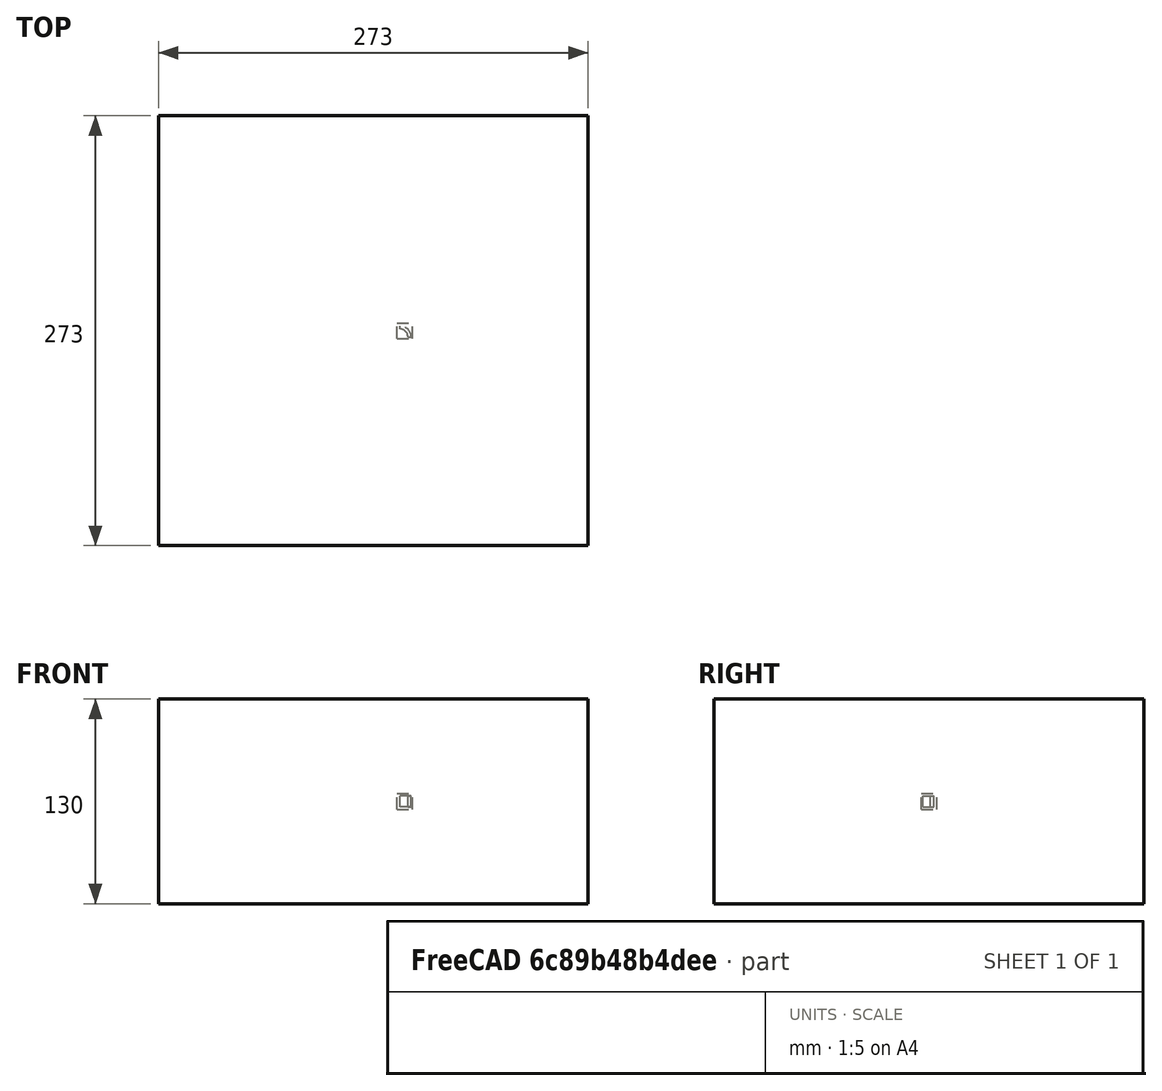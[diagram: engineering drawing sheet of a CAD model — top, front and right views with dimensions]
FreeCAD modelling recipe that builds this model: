
FCSTD DOCUMENT  (FreeCAD 0.20RUnknown)
Label: array-of-array-b
License: All rights reserved
LicenseURL: http://en.wikipedia.org/wiki/All_rights_reserved
objects: App::DocumentObjectGroupPython×1251, Part::FeaturePython×5, App::Part×5
note: 3 computed .brp shape members not serialized (recipe doc carries the construction recipe); baked Part::Feature solids carry a one-line shape summary decoded from their .brp

FEATURE [App::DocumentObjectGroupPython] HALFPI  # scripted group (container) (typed FeaturePython)
  name = HALFPI
  value = pi/2.
FEATURE [App::DocumentObjectGroupPython] PI  # scripted group (container) (typed FeaturePython)
  name = PI
  value = 1.*pi
FEATURE [App::DocumentObjectGroupPython] TWOPI  # scripted group (container) (typed FeaturePython)
  name = TWOPI
  value = 2.*pi
FEATURE [App::DocumentObjectGroupPython] Constants  # scripted group (container) (typed FeaturePython)
  Group = -> [HALFPI,PI,TWOPI]
FEATURE [App::DocumentObjectGroupPython] Variables  # scripted group (container) (typed FeaturePython)
FEATURE [App::DocumentObjectGroupPython] Quantities  # scripted group (container) (typed FeaturePython)
FEATURE [App::DocumentObjectGroupPython] Isotopes  # scripted group (container) (typed FeaturePython)
FEATURE [App::DocumentObjectGroupPython] Elements  # scripted group (container) (typed FeaturePython)
FEATURE [App::DocumentObjectGroupPython] Matrix  # scripted group (container) (typed FeaturePython)
FEATURE [App::DocumentObjectGroupPython] Surfaces  # scripted group (container) (typed FeaturePython)
FEATURE [App::DocumentObjectGroupPython] Opticals  # scripted group (container) (typed FeaturePython)
  Group = -> [Matrix,Surfaces]
FEATURE [App::DocumentObjectGroupPython] G4Isotopes  # scripted group (container) (typed FeaturePython)
FEATURE [App::DocumentObjectGroupPython] H_element  # scripted group (container) (typed FeaturePython)
  Z = 1
  atom_value = 1.008
  formula = H
  name = H_element
FEATURE [App::DocumentObjectGroupPython] He_element  # scripted group (container) (typed FeaturePython)
  Z = 2
  atom_value = 4.0026
  formula = He
  name = He_element
FEATURE [App::DocumentObjectGroupPython] Li_element  # scripted group (container) (typed FeaturePython)
  Z = 3
  atom_value = 6.94
  formula = Li
  name = Li_element
FEATURE [App::DocumentObjectGroupPython] Be_element  # scripted group (container) (typed FeaturePython)
  Z = 4
  atom_value = 9.01218
  formula = Be
  name = Be_element
FEATURE [App::DocumentObjectGroupPython] B_element  # scripted group (container) (typed FeaturePython)
  Z = 5
  atom_value = 10.81
  formula = B
  name = B_element
FEATURE [App::DocumentObjectGroupPython] C_element  # scripted group (container) (typed FeaturePython)
  Z = 6
  atom_value = 12.011
  formula = C
  name = C_element
FEATURE [App::DocumentObjectGroupPython] N_element  # scripted group (container) (typed FeaturePython)
  Z = 7
  atom_value = 14.007
  formula = N
  name = N_element
FEATURE [App::DocumentObjectGroupPython] O_element  # scripted group (container) (typed FeaturePython)
  Z = 8
  atom_value = 15.999
  formula = O
  name = O_element
FEATURE [App::DocumentObjectGroupPython] F_element  # scripted group (container) (typed FeaturePython)
  Z = 9
  atom_value = 18.9984
  formula = F
  name = F_element
FEATURE [App::DocumentObjectGroupPython] Ne_element  # scripted group (container) (typed FeaturePython)
  Z = 10
  atom_value = 20.1797
  formula = Ne
  name = Ne_element
FEATURE [App::DocumentObjectGroupPython] Na_element  # scripted group (container) (typed FeaturePython)
  Z = 11
  atom_value = 22.9898
  formula = Na
  name = Na_element
FEATURE [App::DocumentObjectGroupPython] Mg_element  # scripted group (container) (typed FeaturePython)
  Z = 12
  atom_value = 24.305
  formula = Mg
  name = Mg_element
FEATURE [App::DocumentObjectGroupPython] Al_element  # scripted group (container) (typed FeaturePython)
  Z = 13
  atom_value = 26.9815
  formula = Al
  name = Al_element
FEATURE [App::DocumentObjectGroupPython] Si_element  # scripted group (container) (typed FeaturePython)
  Z = 14
  atom_value = 28.085
  formula = Si
  name = Si_element
FEATURE [App::DocumentObjectGroupPython] P_element  # scripted group (container) (typed FeaturePython)
  Z = 15
  atom_value = 30.9738
  formula = P
  name = P_element
FEATURE [App::DocumentObjectGroupPython] S_element  # scripted group (container) (typed FeaturePython)
  Z = 16
  atom_value = 32.06
  formula = S
  name = S_element
FEATURE [App::DocumentObjectGroupPython] Cl_element  # scripted group (container) (typed FeaturePython)
  Z = 17
  atom_value = 35.45
  formula = Cl
  name = Cl_element
FEATURE [App::DocumentObjectGroupPython] Ar_element  # scripted group (container) (typed FeaturePython)
  Z = 18
  atom_value = 39.95
  formula = Ar
  name = Ar_element
FEATURE [App::DocumentObjectGroupPython] K_element  # scripted group (container) (typed FeaturePython)
  Z = 19
  atom_value = 39.0983
  formula = K
  name = K_element
FEATURE [App::DocumentObjectGroupPython] Ca_element  # scripted group (container) (typed FeaturePython)
  Z = 20
  atom_value = 40.078
  formula = Ca
  name = Ca_element
FEATURE [App::DocumentObjectGroupPython] Sc_element  # scripted group (container) (typed FeaturePython)
  Z = 21
  atom_value = 44.9559
  formula = Sc
  name = Sc_element
FEATURE [App::DocumentObjectGroupPython] Ti_element  # scripted group (container) (typed FeaturePython)
  Z = 22
  atom_value = 47.867
  formula = Ti
  name = Ti_element
FEATURE [App::DocumentObjectGroupPython] V_element  # scripted group (container) (typed FeaturePython)
  Z = 23
  atom_value = 50.9415
  formula = V
  name = V_element
FEATURE [App::DocumentObjectGroupPython] Cr_element  # scripted group (container) (typed FeaturePython)
  Z = 24
  atom_value = 51.9961
  formula = Cr
  name = Cr_element
FEATURE [App::DocumentObjectGroupPython] Mn_element  # scripted group (container) (typed FeaturePython)
  Z = 25
  atom_value = 54.938
  formula = Mn
  name = Mn_element
FEATURE [App::DocumentObjectGroupPython] Fe_element  # scripted group (container) (typed FeaturePython)
  Z = 26
  atom_value = 55.845
  formula = Fe
  name = Fe_element
FEATURE [App::DocumentObjectGroupPython] Co_element  # scripted group (container) (typed FeaturePython)
  Z = 27
  atom_value = 58.9332
  formula = Co
  name = Co_element
FEATURE [App::DocumentObjectGroupPython] Ni_element  # scripted group (container) (typed FeaturePython)
  Z = 28
  atom_value = 58.6934
  formula = Ni
  name = Ni_element
FEATURE [App::DocumentObjectGroupPython] Cu_element  # scripted group (container) (typed FeaturePython)
  Z = 29
  atom_value = 63.546
  formula = Cu
  name = Cu_element
FEATURE [App::DocumentObjectGroupPython] Zn_element  # scripted group (container) (typed FeaturePython)
  Z = 30
  atom_value = 65.38
  formula = Zn
  name = Zn_element
FEATURE [App::DocumentObjectGroupPython] Ga_element  # scripted group (container) (typed FeaturePython)
  Z = 31
  atom_value = 69.723
  formula = Ga
  name = Ga_element
FEATURE [App::DocumentObjectGroupPython] Ge_element  # scripted group (container) (typed FeaturePython)
  Z = 32
  atom_value = 72.63
  formula = Ge
  name = Ge_element
FEATURE [App::DocumentObjectGroupPython] As_element  # scripted group (container) (typed FeaturePython)
  Z = 33
  atom_value = 74.9216
  formula = As
  name = As_element
FEATURE [App::DocumentObjectGroupPython] Se_element  # scripted group (container) (typed FeaturePython)
  Z = 34
  atom_value = 78.971
  formula = Se
  name = Se_element
FEATURE [App::DocumentObjectGroupPython] Br_element  # scripted group (container) (typed FeaturePython)
  Z = 35
  atom_value = 79.904
  formula = Br
  name = Br_element
FEATURE [App::DocumentObjectGroupPython] Kr_element  # scripted group (container) (typed FeaturePython)
  Z = 36
  atom_value = 83.798
  formula = Kr
  name = Kr_element
FEATURE [App::DocumentObjectGroupPython] Rb_element  # scripted group (container) (typed FeaturePython)
  Z = 37
  atom_value = 85.4678
  formula = Rb
  name = Rb_element
FEATURE [App::DocumentObjectGroupPython] Sr_element  # scripted group (container) (typed FeaturePython)
  Z = 38
  atom_value = 87.62
  formula = Sr
  name = Sr_element
FEATURE [App::DocumentObjectGroupPython] Y_element  # scripted group (container) (typed FeaturePython)
  Z = 39
  atom_value = 88.9058
  formula = Y
  name = Y_element
FEATURE [App::DocumentObjectGroupPython] Zr_element  # scripted group (container) (typed FeaturePython)
  Z = 40
  atom_value = 91.224
  formula = Zr
  name = Zr_element
FEATURE [App::DocumentObjectGroupPython] Nb_element  # scripted group (container) (typed FeaturePython)
  Z = 41
  atom_value = 92.9064
  formula = Nb
  name = Nb_element
FEATURE [App::DocumentObjectGroupPython] Mo_element  # scripted group (container) (typed FeaturePython)
  Z = 42
  atom_value = 95.95
  formula = Mo
  name = Mo_element
FEATURE [App::DocumentObjectGroupPython] Tc_element  # scripted group (container) (typed FeaturePython)
  Z = 43
  atom_value = 97
  formula = Tc
  name = Tc_element
FEATURE [App::DocumentObjectGroupPython] Ru_element  # scripted group (container) (typed FeaturePython)
  Z = 44
  atom_value = 101.07
  formula = Ru
  name = Ru_element
FEATURE [App::DocumentObjectGroupPython] Rh_element  # scripted group (container) (typed FeaturePython)
  Z = 45
  atom_value = 102.905
  formula = Rh
  name = Rh_element
FEATURE [App::DocumentObjectGroupPython] Pd_element  # scripted group (container) (typed FeaturePython)
  Z = 46
  atom_value = 106.42
  formula = Pd
  name = Pd_element
FEATURE [App::DocumentObjectGroupPython] Ag_element  # scripted group (container) (typed FeaturePython)
  Z = 47
  atom_value = 107.868
  formula = Ag
  name = Ag_element
FEATURE [App::DocumentObjectGroupPython] Cd_element  # scripted group (container) (typed FeaturePython)
  Z = 48
  atom_value = 112.414
  formula = Cd
  name = Cd_element
FEATURE [App::DocumentObjectGroupPython] In_element  # scripted group (container) (typed FeaturePython)
  Z = 49
  atom_value = 114.818
  formula = In
  name = In_element
FEATURE [App::DocumentObjectGroupPython] Sn_element  # scripted group (container) (typed FeaturePython)
  Z = 50
  atom_value = 118.71
  formula = Sn
  name = Sn_element
FEATURE [App::DocumentObjectGroupPython] Sb_element  # scripted group (container) (typed FeaturePython)
  Z = 51
  atom_value = 121.76
  formula = Sb
  name = Sb_element
FEATURE [App::DocumentObjectGroupPython] Te_element  # scripted group (container) (typed FeaturePython)
  Z = 52
  atom_value = 127.6
  formula = Te
  name = Te_element
FEATURE [App::DocumentObjectGroupPython] I_element  # scripted group (container) (typed FeaturePython)
  Z = 53
  atom_value = 126.904
  formula = I
  name = I_element
FEATURE [App::DocumentObjectGroupPython] Xe_element  # scripted group (container) (typed FeaturePython)
  Z = 54
  atom_value = 131.293
  formula = Xe
  name = Xe_element
FEATURE [App::DocumentObjectGroupPython] Cs_element  # scripted group (container) (typed FeaturePython)
  Z = 55
  atom_value = 132.905
  formula = Cs
  name = Cs_element
FEATURE [App::DocumentObjectGroupPython] Ba_element  # scripted group (container) (typed FeaturePython)
  Z = 56
  atom_value = 137.327
  formula = Ba
  name = Ba_element
FEATURE [App::DocumentObjectGroupPython] La_element  # scripted group (container) (typed FeaturePython)
  Z = 57
  atom_value = 138.905
  formula = La
  name = La_element
FEATURE [App::DocumentObjectGroupPython] Ce_element  # scripted group (container) (typed FeaturePython)
  Z = 58
  atom_value = 140.116
  formula = Ce
  name = Ce_element
FEATURE [App::DocumentObjectGroupPython] Pr_element  # scripted group (container) (typed FeaturePython)
  Z = 59
  atom_value = 140.908
  formula = Pr
  name = Pr_element
FEATURE [App::DocumentObjectGroupPython] Nd_element  # scripted group (container) (typed FeaturePython)
  Z = 60
  atom_value = 144.242
  formula = Nd
  name = Nd_element
FEATURE [App::DocumentObjectGroupPython] Pm_element  # scripted group (container) (typed FeaturePython)
  Z = 61
  atom_value = 145
  formula = Pm
  name = Pm_element
FEATURE [App::DocumentObjectGroupPython] Sm_element  # scripted group (container) (typed FeaturePython)
  Z = 62
  atom_value = 150.36
  formula = Sm
  name = Sm_element
FEATURE [App::DocumentObjectGroupPython] Eu_element  # scripted group (container) (typed FeaturePython)
  Z = 63
  atom_value = 151.964
  formula = Eu
  name = Eu_element
FEATURE [App::DocumentObjectGroupPython] Gd_element  # scripted group (container) (typed FeaturePython)
  Z = 64
  atom_value = 157.25
  formula = Gd
  name = Gd_element
FEATURE [App::DocumentObjectGroupPython] Tb_element  # scripted group (container) (typed FeaturePython)
  Z = 65
  atom_value = 158.925
  formula = Tb
  name = Tb_element
FEATURE [App::DocumentObjectGroupPython] Dy_element  # scripted group (container) (typed FeaturePython)
  Z = 66
  atom_value = 162.5
  formula = Dy
  name = Dy_element
FEATURE [App::DocumentObjectGroupPython] Ho_element  # scripted group (container) (typed FeaturePython)
  Z = 67
  atom_value = 164.93
  formula = Ho
  name = Ho_element
FEATURE [App::DocumentObjectGroupPython] Er_element  # scripted group (container) (typed FeaturePython)
  Z = 68
  atom_value = 167.259
  formula = Er
  name = Er_element
FEATURE [App::DocumentObjectGroupPython] Tm_element  # scripted group (container) (typed FeaturePython)
  Z = 69
  atom_value = 168.934
  formula = Tm
  name = Tm_element
FEATURE [App::DocumentObjectGroupPython] Yb_element  # scripted group (container) (typed FeaturePython)
  Z = 70
  atom_value = 173.045
  formula = Yb
  name = Yb_element
FEATURE [App::DocumentObjectGroupPython] Lu_element  # scripted group (container) (typed FeaturePython)
  Z = 71
  atom_value = 174.967
  formula = Lu
  name = Lu_element
FEATURE [App::DocumentObjectGroupPython] Hf_element  # scripted group (container) (typed FeaturePython)
  Z = 72
  atom_value = 178.49
  formula = Hf
  name = Hf_element
FEATURE [App::DocumentObjectGroupPython] Ta_element  # scripted group (container) (typed FeaturePython)
  Z = 73
  atom_value = 180.948
  formula = Ta
  name = Ta_element
FEATURE [App::DocumentObjectGroupPython] W_element  # scripted group (container) (typed FeaturePython)
  Z = 74
  atom_value = 183.84
  formula = W
  name = W_element
FEATURE [App::DocumentObjectGroupPython] Re_element  # scripted group (container) (typed FeaturePython)
  Z = 75
  atom_value = 186.207
  formula = Re
  name = Re_element
FEATURE [App::DocumentObjectGroupPython] Os_element  # scripted group (container) (typed FeaturePython)
  Z = 76
  atom_value = 190.23
  formula = Os
  name = Os_element
FEATURE [App::DocumentObjectGroupPython] Ir_element  # scripted group (container) (typed FeaturePython)
  Z = 77
  atom_value = 192.217
  formula = Ir
  name = Ir_element
FEATURE [App::DocumentObjectGroupPython] Pt_element  # scripted group (container) (typed FeaturePython)
  Z = 78
  atom_value = 195.084
  formula = Pt
  name = Pt_element
FEATURE [App::DocumentObjectGroupPython] Au_element  # scripted group (container) (typed FeaturePython)
  Z = 79
  atom_value = 196.967
  formula = Au
  name = Au_element
FEATURE [App::DocumentObjectGroupPython] Hg_element  # scripted group (container) (typed FeaturePython)
  Z = 80
  atom_value = 200.592
  formula = Hg
  name = Hg_element
FEATURE [App::DocumentObjectGroupPython] Tl_element  # scripted group (container) (typed FeaturePython)
  Z = 81
  atom_value = 204.38
  formula = Tl
  name = Tl_element
FEATURE [App::DocumentObjectGroupPython] Pb_element  # scripted group (container) (typed FeaturePython)
  Z = 82
  atom_value = 207.2
  formula = Pb
  name = Pb_element
FEATURE [App::DocumentObjectGroupPython] Bi_element  # scripted group (container) (typed FeaturePython)
  Z = 83
  atom_value = 208.98
  formula = Bi
  name = Bi_element
FEATURE [App::DocumentObjectGroupPython] Po_element  # scripted group (container) (typed FeaturePython)
  Z = 84
  atom_value = 209
  formula = Po
  name = Po_element
FEATURE [App::DocumentObjectGroupPython] At_element  # scripted group (container) (typed FeaturePython)
  Z = 85
  atom_value = 210
  formula = At
  name = At_element
FEATURE [App::DocumentObjectGroupPython] Rn_element  # scripted group (container) (typed FeaturePython)
  Z = 86
  atom_value = 222
  formula = Rn
  name = Rn_element
FEATURE [App::DocumentObjectGroupPython] Fr_element  # scripted group (container) (typed FeaturePython)
  Z = 87
  atom_value = 223
  formula = Fr
  name = Fr_element
FEATURE [App::DocumentObjectGroupPython] Ra_element  # scripted group (container) (typed FeaturePython)
  Z = 88
  atom_value = 226
  formula = Ra
  name = Ra_element
FEATURE [App::DocumentObjectGroupPython] Ac_element  # scripted group (container) (typed FeaturePython)
  Z = 89
  atom_value = 227
  formula = Ac
  name = Ac_element
FEATURE [App::DocumentObjectGroupPython] Th_element  # scripted group (container) (typed FeaturePython)
  Z = 90
  atom_value = 232.038
  formula = Th
  name = Th_element
FEATURE [App::DocumentObjectGroupPython] Pa_element  # scripted group (container) (typed FeaturePython)
  Z = 91
  atom_value = 231.036
  formula = Pa
  name = Pa_element
FEATURE [App::DocumentObjectGroupPython] U_element  # scripted group (container) (typed FeaturePython)
  Z = 92
  atom_value = 238.029
  formula = U
  name = U_element
FEATURE [App::DocumentObjectGroupPython] Np_element  # scripted group (container) (typed FeaturePython)
  Z = 93
  atom_value = 237
  formula = Np
  name = Np_element
FEATURE [App::DocumentObjectGroupPython] Pu_element  # scripted group (container) (typed FeaturePython)
  Z = 94
  atom_value = 244
  formula = Pu
  name = Pu_element
FEATURE [App::DocumentObjectGroupPython] Am_element  # scripted group (container) (typed FeaturePython)
  Z = 95
  atom_value = 243
  formula = Am
  name = Am_element
FEATURE [App::DocumentObjectGroupPython] Cm_element  # scripted group (container) (typed FeaturePython)
  Z = 96
  atom_value = 247
  formula = Cm
  name = Cm_element
FEATURE [App::DocumentObjectGroupPython] Bk_element  # scripted group (container) (typed FeaturePython)
  Z = 97
  atom_value = 247
  formula = Bk
  name = Bk_element
FEATURE [App::DocumentObjectGroupPython] Cf_element  # scripted group (container) (typed FeaturePython)
  Z = 98
  atom_value = 251
  formula = Cf
  name = Cf_element
FEATURE [App::DocumentObjectGroupPython] G4Elements  # scripted group (container) (typed FeaturePython)
  Group = -> [H_element,He_element,Li_element,Be_element,B_element,C_element,N_element,O_element,F_element,Ne_element,Na_element,Mg_element,Al_element,Si_element,P_element,S_element,Cl_element,Ar_element,K_element,Ca_element,Sc_element,Ti_element,V_element,Cr_element,Mn_element,Fe_element,Co_element,Ni_element,Cu_element,Zn_element,Ga_element,Ge_element,As_element,Se_element,Br_element,Kr_element,Rb_element,+61 more]
FEATURE [App::DocumentObjectGroupPython] H_element001  label="H_element : 0.101"  # scripted group (container) (typed FeaturePython)
  n = 0.101327
FEATURE [App::DocumentObjectGroupPython] C_element001  label="C_element : 0.775"  # scripted group (container) (typed FeaturePython)
  n = 0.7755
FEATURE [App::DocumentObjectGroupPython] N_element001  label="N_element : 0.035"  # scripted group (container) (typed FeaturePython)
  n = 0.035057
FEATURE [App::DocumentObjectGroupPython] O_element001  label="O_element : 0.052"  # scripted group (container) (typed FeaturePython)
  n = 0.0523159
FEATURE [App::DocumentObjectGroupPython] F_element001  label="F_element : 0.017"  # scripted group (container) (typed FeaturePython)
  n = 0.017422
FEATURE [App::DocumentObjectGroupPython] Ca_element001  label="Ca_element : 0.018"  # scripted group (container) (typed FeaturePython)
  n = 0.018378
FEATURE [App::DocumentObjectGroupPython] G4_A_150_TISSUE  label="G4_A-150_TISSUE"  # scripted group (container) (typed FeaturePython)
  Dunit = g/cm3
  Dvalue = 1.127
  Group = -> [H_element001,C_element001,N_element001,O_element001,F_element001,Ca_element001]
  conduct = 2
  density = 1
  expand = 3
  formula = G4_A-150_TISSUE
  name = G4_A-150_TISSUE
  specific = 4
FEATURE [App::DocumentObjectGroupPython] C_element002  label="C_element : 3"  # scripted group (container) (typed FeaturePython)
  n = 3
  ref = C_element
FEATURE [App::DocumentObjectGroupPython] H_element002  label="H_element : 6"  # scripted group (container) (typed FeaturePython)
  n = 6
  ref = H_element
FEATURE [App::DocumentObjectGroupPython] O_element002  label="O_element : 1"  # scripted group (container) (typed FeaturePython)
  n = 1
  ref = O_element
FEATURE [App::DocumentObjectGroupPython] G4_ACETONE  # scripted group (container) (typed FeaturePython)
  Dunit = g/cm3
  Dvalue = 0.7899
  Group = -> [C_element002,H_element002,O_element002]
  conduct = 2
  density = 1
  expand = 3
  formula = G4_ACETONE
  name = G4_ACETONE
  specific = 4
FEATURE [App::DocumentObjectGroupPython] C_element003  label="C_element : 2"  # scripted group (container) (typed FeaturePython)
  n = 2
  ref = C_element
FEATURE [App::DocumentObjectGroupPython] H_element003  label="H_element : 2"  # scripted group (container) (typed FeaturePython)
  n = 2
  ref = H_element
FEATURE [App::DocumentObjectGroupPython] G4_ACETYLENE  # scripted group (container) (typed FeaturePython)
  Dunit = g/cm3
  Dvalue = 0.0010967
  Group = -> [C_element003,H_element003]
  conduct = 2
  density = 1
  expand = 3
  formula = G4_ACETYLENE
  name = G4_ACETYLENE
  specific = 4
FEATURE [App::DocumentObjectGroupPython] C_element004  label="C_element : 5"  # scripted group (container) (typed FeaturePython)
  n = 5
  ref = C_element
FEATURE [App::DocumentObjectGroupPython] H_element004  label="H_element : 5"  # scripted group (container) (typed FeaturePython)
  n = 5
  ref = H_element
FEATURE [App::DocumentObjectGroupPython] N_element002  label="N_element : 5"  # scripted group (container) (typed FeaturePython)
  n = 5
  ref = N_element
FEATURE [App::DocumentObjectGroupPython] G4_ADENINE  # scripted group (container) (typed FeaturePython)
  Dunit = g/cm3
  Dvalue = 1.6
  Group = -> [C_element004,H_element004,N_element002]
  conduct = 2
  density = 1
  expand = 3
  formula = G4_ADENINE
  name = G4_ADENINE
  specific = 4
FEATURE [App::DocumentObjectGroupPython] H_element005  label="H_element : 0.114"  # scripted group (container) (typed FeaturePython)
  n = 0.114
FEATURE [App::DocumentObjectGroupPython] C_element005  label="C_element : 0.598"  # scripted group (container) (typed FeaturePython)
  n = 0.598
FEATURE [App::DocumentObjectGroupPython] N_element003  label="N_element : 0.007"  # scripted group (container) (typed FeaturePython)
  n = 0.007
FEATURE [App::DocumentObjectGroupPython] O_element003  label="O_element : 0.278"  # scripted group (container) (typed FeaturePython)
  n = 0.278
FEATURE [App::DocumentObjectGroupPython] Na_element001  label="Na_element : 0.001"  # scripted group (container) (typed FeaturePython)
  n = 0.001
FEATURE [App::DocumentObjectGroupPython] S_element001  label="S_element : 0.001"  # scripted group (container) (typed FeaturePython)
  n = 0.001
FEATURE [App::DocumentObjectGroupPython] Cl_element001  label="Cl_element : 0.001"  # scripted group (container) (typed FeaturePython)
  n = 0.001
FEATURE [App::DocumentObjectGroupPython] G4_ADIPOSE_TISSUE_ICRP  # scripted group (container) (typed FeaturePython)
  Dunit = g/cm3
  Dvalue = 0.95
  Group = -> [H_element005,C_element005,N_element003,O_element003,Na_element001,S_element001,Cl_element001]
  conduct = 2
  density = 1
  expand = 3
  formula = G4_ADIPOSE_TISSUE_ICRP
  name = G4_ADIPOSE_TISSUE_ICRP
  specific = 4
FEATURE [App::DocumentObjectGroupPython] C_element006  label="C_element : 0.000"  # scripted group (container) (typed FeaturePython)
  n = 0.000124
FEATURE [App::DocumentObjectGroupPython] N_element004  label="N_element : 0.755"  # scripted group (container) (typed FeaturePython)
  n = 0.755268
FEATURE [App::DocumentObjectGroupPython] O_element004  label="O_element : 0.232"  # scripted group (container) (typed FeaturePython)
  n = 0.231781
FEATURE [App::DocumentObjectGroupPython] Ar_element001  label="Ar_element : 0.013"  # scripted group (container) (typed FeaturePython)
  n = 0.012827
FEATURE [App::DocumentObjectGroupPython] G4_AIR  # scripted group (container) (typed FeaturePython)
  Dunit = g/cm3
  Dvalue = 0.00120479
  Group = -> [C_element006,N_element004,O_element004,Ar_element001]
  conduct = 2
  density = 1
  expand = 3
  formula = G4_AIR
  name = G4_AIR
  specific = 4
FEATURE [App::DocumentObjectGroupPython] C_element007  label="C_element : 006"  # scripted group (container) (typed FeaturePython)
  n = 3
  ref = C_element
FEATURE [App::DocumentObjectGroupPython] H_element006  label="H_element : 7"  # scripted group (container) (typed FeaturePython)
  n = 7
  ref = H_element
FEATURE [App::DocumentObjectGroupPython] N_element005  label="N_element : 1"  # scripted group (container) (typed FeaturePython)
  n = 1
  ref = N_element
FEATURE [App::DocumentObjectGroupPython] O_element005  label="O_element : 2"  # scripted group (container) (typed FeaturePython)
  n = 2
  ref = O_element
FEATURE [App::DocumentObjectGroupPython] G4_ALANINE  # scripted group (container) (typed FeaturePython)
  Dunit = g/cm3
  Dvalue = 1.42
  Group = -> [C_element007,H_element006,N_element005,O_element005]
  conduct = 2
  density = 1
  expand = 3
  formula = G4_ALANINE
  name = G4_ALANINE
  specific = 4
FEATURE [App::DocumentObjectGroupPython] Al_element001  label="Al_element : 2"  # scripted group (container) (typed FeaturePython)
  n = 2
  ref = Al_element
FEATURE [App::DocumentObjectGroupPython] O_element006  label="O_element : 3"  # scripted group (container) (typed FeaturePython)
  n = 3
  ref = O_element
FEATURE [App::DocumentObjectGroupPython] G4_ALUMINUM_OXIDE  # scripted group (container) (typed FeaturePython)
  Dunit = g/cm3
  Dvalue = 3.97
  Group = -> [Al_element001,O_element006]
  conduct = 2
  density = 1
  expand = 3
  formula = G4_ALUMINUM_OXIDE
  name = G4_ALUMINUM_OXIDE
  specific = 4
FEATURE [App::DocumentObjectGroupPython] H_element007  label="H_element : 0.106"  # scripted group (container) (typed FeaturePython)
  n = 0.10593
FEATURE [App::DocumentObjectGroupPython] C_element008  label="C_element : 0.789"  # scripted group (container) (typed FeaturePython)
  n = 0.788974
FEATURE [App::DocumentObjectGroupPython] O_element007  label="O_element : 0.105"  # scripted group (container) (typed FeaturePython)
  n = 0.105096
FEATURE [App::DocumentObjectGroupPython] G4_AMBER  # scripted group (container) (typed FeaturePython)
  Dunit = g/cm3
  Dvalue = 1.1
  Group = -> [H_element007,C_element008,O_element007]
  conduct = 2
  density = 1
  expand = 3
  formula = G4_AMBER
  name = G4_AMBER
  specific = 4
FEATURE [App::DocumentObjectGroupPython] N_element006  label="N_element : 006"  # scripted group (container) (typed FeaturePython)
  n = 1
  ref = N_element
FEATURE [App::DocumentObjectGroupPython] H_element008  label="H_element : 3"  # scripted group (container) (typed FeaturePython)
  n = 3
  ref = H_element
FEATURE [App::DocumentObjectGroupPython] G4_AMMONIA  # scripted group (container) (typed FeaturePython)
  Dunit = g/cm3
  Dvalue = 0.000826019
  Group = -> [N_element006,H_element008]
  conduct = 2
  density = 1
  expand = 3
  formula = G4_AMMONIA
  name = G4_AMMONIA
  specific = 4
FEATURE [App::DocumentObjectGroupPython] C_element009  label="C_element : 6"  # scripted group (container) (typed FeaturePython)
  n = 6
  ref = C_element
FEATURE [App::DocumentObjectGroupPython] H_element009  label="H_element : 008"  # scripted group (container) (typed FeaturePython)
  n = 7
  ref = H_element
FEATURE [App::DocumentObjectGroupPython] N_element007  label="N_element : 007"  # scripted group (container) (typed FeaturePython)
  n = 1
  ref = N_element
FEATURE [App::DocumentObjectGroupPython] G4_ANILINE  # scripted group (container) (typed FeaturePython)
  Dunit = g/cm3
  Dvalue = 1.0235
  Group = -> [C_element009,H_element009,N_element007]
  conduct = 2
  density = 1
  expand = 3
  formula = G4_ANILINE
  name = G4_ANILINE
  specific = 4
FEATURE [App::DocumentObjectGroupPython] C_element010  label="C_element : 14"  # scripted group (container) (typed FeaturePython)
  n = 14
  ref = C_element
FEATURE [App::DocumentObjectGroupPython] H_element010  label="H_element : 10"  # scripted group (container) (typed FeaturePython)
  n = 10
  ref = H_element
FEATURE [App::DocumentObjectGroupPython] G4_ANTHRACENE  # scripted group (container) (typed FeaturePython)
  Dunit = g/cm3
  Dvalue = 1.283
  Group = -> [C_element010,H_element010]
  conduct = 2
  density = 1
  expand = 3
  formula = G4_ANTHRACENE
  name = G4_ANTHRACENE
  specific = 4
FEATURE [App::DocumentObjectGroupPython] H_element011  label="H_element : 0.065"  # scripted group (container) (typed FeaturePython)
  n = 0.0654709
FEATURE [App::DocumentObjectGroupPython] C_element011  label="C_element : 0.537"  # scripted group (container) (typed FeaturePython)
  n = 0.536944
FEATURE [App::DocumentObjectGroupPython] N_element008  label="N_element : 0.021"  # scripted group (container) (typed FeaturePython)
  n = 0.0215
FEATURE [App::DocumentObjectGroupPython] O_element008  label="O_element : 0.032"  # scripted group (container) (typed FeaturePython)
  n = 0.032085
FEATURE [App::DocumentObjectGroupPython] F_element002  label="F_element : 0.167"  # scripted group (container) (typed FeaturePython)
  n = 0.167411
FEATURE [App::DocumentObjectGroupPython] Ca_element002  label="Ca_element : 0.177"  # scripted group (container) (typed FeaturePython)
  n = 0.176589
FEATURE [App::DocumentObjectGroupPython] G4_B_100_BONE  label="G4_B-100_BONE"  # scripted group (container) (typed FeaturePython)
  Dunit = g/cm3
  Dvalue = 1.45
  Group = -> [H_element011,C_element011,N_element008,O_element008,F_element002,Ca_element002]
  conduct = 2
  density = 1
  expand = 3
  formula = G4_B-100_BONE
  name = G4_B-100_BONE
  specific = 4
FEATURE [App::DocumentObjectGroupPython] H_element012  label="H_element : 0.057"  # scripted group (container) (typed FeaturePython)
  n = 0.057441
FEATURE [App::DocumentObjectGroupPython] C_element012  label="C_element : 0.790"  # scripted group (container) (typed FeaturePython)
  n = 0.774591
FEATURE [App::DocumentObjectGroupPython] O_element009  label="O_element : 0.168"  # scripted group (container) (typed FeaturePython)
  n = 0.167968
FEATURE [App::DocumentObjectGroupPython] G4_BAKELITE  # scripted group (container) (typed FeaturePython)
  Dunit = g/cm3
  Dvalue = 1.25
  Group = -> [H_element012,C_element012,O_element009]
  conduct = 2
  density = 1
  expand = 3
  formula = G4_BAKELITE
  name = G4_BAKELITE
  specific = 4
FEATURE [App::DocumentObjectGroupPython] Ba_element001  label="Ba_element : 1"  # scripted group (container) (typed FeaturePython)
  n = 1
  ref = Ba_element
FEATURE [App::DocumentObjectGroupPython] F_element003  label="F_element : 2"  # scripted group (container) (typed FeaturePython)
  n = 2
  ref = F_element
FEATURE [App::DocumentObjectGroupPython] G4_BARIUM_FLUORIDE  # scripted group (container) (typed FeaturePython)
  Dunit = g/cm3
  Dvalue = 4.89
  Group = -> [Ba_element001,F_element003]
  conduct = 2
  density = 1
  expand = 3
  formula = G4_BARIUM_FLUORIDE
  name = G4_BARIUM_FLUORIDE
  specific = 4
FEATURE [App::DocumentObjectGroupPython] Ba_element002  label="Ba_element : 002"  # scripted group (container) (typed FeaturePython)
  n = 1
  ref = Ba_element
FEATURE [App::DocumentObjectGroupPython] S_element002  label="S_element : 1"  # scripted group (container) (typed FeaturePython)
  n = 1
  ref = S_element
FEATURE [App::DocumentObjectGroupPython] O_element010  label="O_element : 4"  # scripted group (container) (typed FeaturePython)
  n = 4
  ref = O_element
FEATURE [App::DocumentObjectGroupPython] G4_BARIUM_SULFATE  # scripted group (container) (typed FeaturePython)
  Dunit = g/cm3
  Dvalue = 4.5
  Group = -> [Ba_element002,S_element002,O_element010]
  conduct = 2
  density = 1
  expand = 3
  formula = G4_BARIUM_SULFATE
  name = G4_BARIUM_SULFATE
  specific = 4
FEATURE [App::DocumentObjectGroupPython] C_element013  label="C_element : 007"  # scripted group (container) (typed FeaturePython)
  n = 6
  ref = C_element
FEATURE [App::DocumentObjectGroupPython] H_element013  label="H_element : 009"  # scripted group (container) (typed FeaturePython)
  n = 6
  ref = H_element
FEATURE [App::DocumentObjectGroupPython] G4_BENZENE  # scripted group (container) (typed FeaturePython)
  Dunit = g/cm3
  Dvalue = 0.87865
  Group = -> [C_element013,H_element013]
  conduct = 2
  density = 1
  expand = 3
  formula = G4_BENZENE
  name = G4_BENZENE
  specific = 4
FEATURE [App::DocumentObjectGroupPython] Be_element001  label="Be_element : 1"  # scripted group (container) (typed FeaturePython)
  n = 1
  ref = Be_element
FEATURE [App::DocumentObjectGroupPython] O_element011  label="O_element : 005"  # scripted group (container) (typed FeaturePython)
  n = 1
  ref = O_element
FEATURE [App::DocumentObjectGroupPython] G4_BERYLLIUM_OXIDE  # scripted group (container) (typed FeaturePython)
  Dunit = g/cm3
  Dvalue = 3.01
  Group = -> [Be_element001,O_element011]
  conduct = 2
  density = 1
  expand = 3
  formula = G4_BERYLLIUM_OXIDE
  name = G4_BERYLLIUM_OXIDE
  specific = 4
FEATURE [App::DocumentObjectGroupPython] Bi_element001  label="Bi_element : 4"  # scripted group (container) (typed FeaturePython)
  n = 4
  ref = Bi_element
FEATURE [App::DocumentObjectGroupPython] Ge_element001  label="Ge_element : 3"  # scripted group (container) (typed FeaturePython)
  n = 3
  ref = Ge_element
FEATURE [App::DocumentObjectGroupPython] O_element012  label="O_element : 12"  # scripted group (container) (typed FeaturePython)
  n = 12
  ref = O_element
FEATURE [App::DocumentObjectGroupPython] G4_BGO  # scripted group (container) (typed FeaturePython)
  Dunit = g/cm3
  Dvalue = 7.13
  Group = -> [Bi_element001,Ge_element001,O_element012]
  conduct = 2
  density = 1
  expand = 3
  formula = G4_BGO
  name = G4_BGO
  specific = 4
FEATURE [App::DocumentObjectGroupPython] H_element014  label="H_element : 0.102"  # scripted group (container) (typed FeaturePython)
  n = 0.102
FEATURE [App::DocumentObjectGroupPython] C_element014  label="C_element : 0.110"  # scripted group (container) (typed FeaturePython)
  n = 0.11
FEATURE [App::DocumentObjectGroupPython] N_element009  label="N_element : 0.033"  # scripted group (container) (typed FeaturePython)
  n = 0.033
FEATURE [App::DocumentObjectGroupPython] O_element013  label="O_element : 0.745"  # scripted group (container) (typed FeaturePython)
  n = 0.745
FEATURE [App::DocumentObjectGroupPython] Na_element002  label="Na_element : 0.002"  # scripted group (container) (typed FeaturePython)
  n = 0.001
FEATURE [App::DocumentObjectGroupPython] P_element001  label="P_element : 0.001"  # scripted group (container) (typed FeaturePython)
  n = 0.001
FEATURE [App::DocumentObjectGroupPython] S_element003  label="S_element : 0.002"  # scripted group (container) (typed FeaturePython)
  n = 0.002
FEATURE [App::DocumentObjectGroupPython] Cl_element002  label="Cl_element : 0.003"  # scripted group (container) (typed FeaturePython)
  n = 0.003
FEATURE [App::DocumentObjectGroupPython] K_element001  label="K_element : 0.002"  # scripted group (container) (typed FeaturePython)
  n = 0.002
FEATURE [App::DocumentObjectGroupPython] Fe_element001  label="Fe_element : 0.001"  # scripted group (container) (typed FeaturePython)
  n = 0.001
FEATURE [App::DocumentObjectGroupPython] G4_BLOOD_ICRP  # scripted group (container) (typed FeaturePython)
  Dunit = g/cm3
  Dvalue = 1.06
  Group = -> [H_element014,C_element014,N_element009,O_element013,Na_element002,P_element001,S_element003,Cl_element002,K_element001,Fe_element001]
  conduct = 2
  density = 1
  expand = 3
  formula = G4_BLOOD_ICRP
  name = G4_BLOOD_ICRP
  specific = 4
FEATURE [App::DocumentObjectGroupPython] H_element015  label="H_element : 0.064"  # scripted group (container) (typed FeaturePython)
  n = 0.064
FEATURE [App::DocumentObjectGroupPython] C_element015  label="C_element : 0.278"  # scripted group (container) (typed FeaturePython)
  n = 0.278
FEATURE [App::DocumentObjectGroupPython] N_element010  label="N_element : 0.027"  # scripted group (container) (typed FeaturePython)
  n = 0.027
FEATURE [App::DocumentObjectGroupPython] O_element014  label="O_element : 0.410"  # scripted group (container) (typed FeaturePython)
  n = 0.41
FEATURE [App::DocumentObjectGroupPython] Mg_element001  label="Mg_element : 0.002"  # scripted group (container) (typed FeaturePython)
  n = 0.002
FEATURE [App::DocumentObjectGroupPython] P_element002  label="P_element : 0.070"  # scripted group (container) (typed FeaturePython)
  n = 0.07
FEATURE [App::DocumentObjectGroupPython] S_element004  label="S_element : 0.003"  # scripted group (container) (typed FeaturePython)
  n = 0.002
FEATURE [App::DocumentObjectGroupPython] Ca_element003  label="Ca_element : 0.147"  # scripted group (container) (typed FeaturePython)
  n = 0.147
FEATURE [App::DocumentObjectGroupPython] G4_BONE_COMPACT_ICRU  # scripted group (container) (typed FeaturePython)
  Dunit = g/cm3
  Dvalue = 1.85
  Group = -> [H_element015,C_element015,N_element010,O_element014,Mg_element001,P_element002,S_element004,Ca_element003]
  conduct = 2
  density = 1
  expand = 3
  formula = G4_BONE_COMPACT_ICRU
  name = G4_BONE_COMPACT_ICRU
  specific = 4
FEATURE [App::DocumentObjectGroupPython] H_element016  label="H_element : 0.034"  # scripted group (container) (typed FeaturePython)
  n = 0.034
FEATURE [App::DocumentObjectGroupPython] C_element016  label="C_element : 0.155"  # scripted group (container) (typed FeaturePython)
  n = 0.155
FEATURE [App::DocumentObjectGroupPython] N_element011  label="N_element : 0.042"  # scripted group (container) (typed FeaturePython)
  n = 0.042
FEATURE [App::DocumentObjectGroupPython] O_element015  label="O_element : 0.435"  # scripted group (container) (typed FeaturePython)
  n = 0.435
FEATURE [App::DocumentObjectGroupPython] Na_element003  label="Na_element : 0.003"  # scripted group (container) (typed FeaturePython)
  n = 0.001
FEATURE [App::DocumentObjectGroupPython] Mg_element002  label="Mg_element : 0.003"  # scripted group (container) (typed FeaturePython)
  n = 0.002
FEATURE [App::DocumentObjectGroupPython] P_element003  label="P_element : 0.103"  # scripted group (container) (typed FeaturePython)
  n = 0.103
FEATURE [App::DocumentObjectGroupPython] S_element005  label="S_element : 0.004"  # scripted group (container) (typed FeaturePython)
  n = 0.003
FEATURE [App::DocumentObjectGroupPython] Ca_element004  label="Ca_element : 0.225"  # scripted group (container) (typed FeaturePython)
  n = 0.225
FEATURE [App::DocumentObjectGroupPython] G4_BONE_CORTICAL_ICRP  # scripted group (container) (typed FeaturePython)
  Dunit = g/cm3
  Dvalue = 1.92
  Group = -> [H_element016,C_element016,N_element011,O_element015,Na_element003,Mg_element002,P_element003,S_element005,Ca_element004]
  conduct = 2
  density = 1
  expand = 3
  formula = G4_BONE_CORTICAL_ICRP
  name = G4_BONE_CORTICAL_ICRP
  specific = 4
FEATURE [App::DocumentObjectGroupPython] B_element001  label="B_element : 4"  # scripted group (container) (typed FeaturePython)
  n = 4
  ref = B_element
FEATURE [App::DocumentObjectGroupPython] C_element017  label="C_element : 1"  # scripted group (container) (typed FeaturePython)
  n = 1
  ref = C_element
FEATURE [App::DocumentObjectGroupPython] G4_BORON_CARBIDE  # scripted group (container) (typed FeaturePython)
  Dunit = g/cm3
  Dvalue = 2.52
  Group = -> [B_element001,C_element017]
  conduct = 2
  density = 1
  expand = 3
  formula = G4_BORON_CARBIDE
  name = G4_BORON_CARBIDE
  specific = 4
FEATURE [App::DocumentObjectGroupPython] B_element002  label="B_element : 2"  # scripted group (container) (typed FeaturePython)
  n = 2
  ref = B_element
FEATURE [App::DocumentObjectGroupPython] O_element016  label="O_element : 006"  # scripted group (container) (typed FeaturePython)
  n = 3
  ref = O_element
FEATURE [App::DocumentObjectGroupPython] G4_BORON_OXIDE  # scripted group (container) (typed FeaturePython)
  Dunit = g/cm3
  Dvalue = 1.812
  Group = -> [B_element002,O_element016]
  conduct = 2
  density = 1
  expand = 3
  formula = G4_BORON_OXIDE
  name = G4_BORON_OXIDE
  specific = 4
FEATURE [App::DocumentObjectGroupPython] H_element017  label="H_element : 0.107"  # scripted group (container) (typed FeaturePython)
  n = 0.107
FEATURE [App::DocumentObjectGroupPython] C_element018  label="C_element : 0.145"  # scripted group (container) (typed FeaturePython)
  n = 0.145
FEATURE [App::DocumentObjectGroupPython] N_element012  label="N_element : 0.022"  # scripted group (container) (typed FeaturePython)
  n = 0.022
FEATURE [App::DocumentObjectGroupPython] O_element017  label="O_element : 0.712"  # scripted group (container) (typed FeaturePython)
  n = 0.712
FEATURE [App::DocumentObjectGroupPython] Na_element004  label="Na_element : 0.004"  # scripted group (container) (typed FeaturePython)
  n = 0.002
FEATURE [App::DocumentObjectGroupPython] P_element004  label="P_element : 0.004"  # scripted group (container) (typed FeaturePython)
  n = 0.004
FEATURE [App::DocumentObjectGroupPython] S_element006  label="S_element : 0.005"  # scripted group (container) (typed FeaturePython)
  n = 0.002
FEATURE [App::DocumentObjectGroupPython] Cl_element003  label="Cl_element : 0.004"  # scripted group (container) (typed FeaturePython)
  n = 0.003
FEATURE [App::DocumentObjectGroupPython] K_element002  label="K_element : 0.003"  # scripted group (container) (typed FeaturePython)
  n = 0.003
FEATURE [App::DocumentObjectGroupPython] G4_BRAIN_ICRP  # scripted group (container) (typed FeaturePython)
  Dunit = g/cm3
  Dvalue = 1.04
  Group = -> [H_element017,C_element018,N_element012,O_element017,Na_element004,P_element004,S_element006,Cl_element003,K_element002]
  conduct = 2
  density = 1
  expand = 3
  formula = G4_BRAIN_ICRP
  name = G4_BRAIN_ICRP
  specific = 4
FEATURE [App::DocumentObjectGroupPython] C_element019  label="C_element : 4"  # scripted group (container) (typed FeaturePython)
  n = 4
  ref = C_element
FEATURE [App::DocumentObjectGroupPython] H_element018  label="H_element : 010"  # scripted group (container) (typed FeaturePython)
  n = 10
  ref = H_element
FEATURE [App::DocumentObjectGroupPython] G4_BUTANE  # scripted group (container) (typed FeaturePython)
  Dunit = g/cm3
  Dvalue = 0.00249343
  Group = -> [C_element019,H_element018]
  conduct = 2
  density = 1
  expand = 3
  formula = G4_BUTANE
  name = G4_BUTANE
  specific = 4
FEATURE [App::DocumentObjectGroupPython] C_element020  label="C_element : 008"  # scripted group (container) (typed FeaturePython)
  n = 4
  ref = C_element
FEATURE [App::DocumentObjectGroupPython] H_element019  label="H_element : 011"  # scripted group (container) (typed FeaturePython)
  n = 10
  ref = H_element
FEATURE [App::DocumentObjectGroupPython] O_element018  label="O_element : 007"  # scripted group (container) (typed FeaturePython)
  n = 1
  ref = O_element
FEATURE [App::DocumentObjectGroupPython] G4_N_BUTYL_ALCOHOL  label="G4_N-BUTYL_ALCOHOL"  # scripted group (container) (typed FeaturePython)
  Dunit = g/cm3
  Dvalue = 0.8098
  Group = -> [C_element020,H_element019,O_element018]
  conduct = 2
  density = 1
  expand = 3
  formula = G4_N-BUTYL_ALCOHOL
  name = G4_N-BUTYL_ALCOHOL
  specific = 4
FEATURE [App::DocumentObjectGroupPython] H_element020  label="H_element : 0.025"  # scripted group (container) (typed FeaturePython)
  n = 0.02468
FEATURE [App::DocumentObjectGroupPython] C_element021  label="C_element : 0.502"  # scripted group (container) (typed FeaturePython)
  n = 0.501611
FEATURE [App::DocumentObjectGroupPython] O_element019  label="O_element : 0.005"  # scripted group (container) (typed FeaturePython)
  n = 0.004527
FEATURE [App::DocumentObjectGroupPython] F_element004  label="F_element : 0.465"  # scripted group (container) (typed FeaturePython)
  n = 0.465209
FEATURE [App::DocumentObjectGroupPython] Si_element001  label="Si_element : 0.004"  # scripted group (container) (typed FeaturePython)
  n = 0.003973
FEATURE [App::DocumentObjectGroupPython] G4_C_552  label="G4_C-552"  # scripted group (container) (typed FeaturePython)
  Dunit = g/cm3
  Dvalue = 1.76
  Group = -> [H_element020,C_element021,O_element019,F_element004,Si_element001]
  conduct = 2
  density = 1
  expand = 3
  formula = G4_C-552
  name = G4_C-552
  specific = 4
FEATURE [App::DocumentObjectGroupPython] Cd_element001  label="Cd_element : 1"  # scripted group (container) (typed FeaturePython)
  n = 1
  ref = Cd_element
FEATURE [App::DocumentObjectGroupPython] Te_element001  label="Te_element : 1"  # scripted group (container) (typed FeaturePython)
  n = 1
  ref = Te_element
FEATURE [App::DocumentObjectGroupPython] G4_CADMIUM_TELLURIDE  # scripted group (container) (typed FeaturePython)
  Dunit = g/cm3
  Dvalue = 6.2
  Group = -> [Cd_element001,Te_element001]
  conduct = 2
  density = 1
  expand = 3
  formula = G4_CADMIUM_TELLURIDE
  name = G4_CADMIUM_TELLURIDE
  specific = 4
FEATURE [App::DocumentObjectGroupPython] Cd_element002  label="Cd_element : 002"  # scripted group (container) (typed FeaturePython)
  n = 1
  ref = Cd_element
FEATURE [App::DocumentObjectGroupPython] W_element001  label="W_element : 1"  # scripted group (container) (typed FeaturePython)
  n = 1
  ref = W_element
FEATURE [App::DocumentObjectGroupPython] O_element020  label="O_element : 008"  # scripted group (container) (typed FeaturePython)
  n = 4
  ref = O_element
FEATURE [App::DocumentObjectGroupPython] G4_CADMIUM_TUNGSTATE  # scripted group (container) (typed FeaturePython)
  Dunit = g/cm3
  Dvalue = 7.9
  Group = -> [Cd_element002,W_element001,O_element020]
  conduct = 2
  density = 1
  expand = 3
  formula = G4_CADMIUM_TUNGSTATE
  name = G4_CADMIUM_TUNGSTATE
  specific = 4
FEATURE [App::DocumentObjectGroupPython] Ca_element005  label="Ca_element : 1"  # scripted group (container) (typed FeaturePython)
  n = 1
  ref = Ca_element
FEATURE [App::DocumentObjectGroupPython] C_element022  label="C_element : 009"  # scripted group (container) (typed FeaturePython)
  n = 1
  ref = C_element
FEATURE [App::DocumentObjectGroupPython] O_element021  label="O_element : 009"  # scripted group (container) (typed FeaturePython)
  n = 3
  ref = O_element
FEATURE [App::DocumentObjectGroupPython] G4_CALCIUM_CARBONATE  # scripted group (container) (typed FeaturePython)
  Dunit = g/cm3
  Dvalue = 2.8
  Group = -> [Ca_element005,C_element022,O_element021]
  conduct = 2
  density = 1
  expand = 3
  formula = G4_CALCIUM_CARBONATE
  name = G4_CALCIUM_CARBONATE
  specific = 4
FEATURE [App::DocumentObjectGroupPython] Ca_element006  label="Ca_element : 002"  # scripted group (container) (typed FeaturePython)
  n = 1
  ref = Ca_element
FEATURE [App::DocumentObjectGroupPython] F_element005  label="F_element : 003"  # scripted group (container) (typed FeaturePython)
  n = 2
  ref = F_element
FEATURE [App::DocumentObjectGroupPython] G4_CALCIUM_FLUORIDE  # scripted group (container) (typed FeaturePython)
  Dunit = g/cm3
  Dvalue = 3.18
  Group = -> [Ca_element006,F_element005]
  conduct = 2
  density = 1
  expand = 3
  formula = G4_CALCIUM_FLUORIDE
  name = G4_CALCIUM_FLUORIDE
  specific = 4
FEATURE [App::DocumentObjectGroupPython] Ca_element007  label="Ca_element : 003"  # scripted group (container) (typed FeaturePython)
  n = 1
  ref = Ca_element
FEATURE [App::DocumentObjectGroupPython] O_element022  label="O_element : 010"  # scripted group (container) (typed FeaturePython)
  n = 1
  ref = O_element
FEATURE [App::DocumentObjectGroupPython] G4_CALCIUM_OXIDE  # scripted group (container) (typed FeaturePython)
  Dunit = g/cm3
  Dvalue = 3.3
  Group = -> [Ca_element007,O_element022]
  conduct = 2
  density = 1
  expand = 3
  formula = G4_CALCIUM_OXIDE
  name = G4_CALCIUM_OXIDE
  specific = 4
FEATURE [App::DocumentObjectGroupPython] Ca_element008  label="Ca_element : 004"  # scripted group (container) (typed FeaturePython)
  n = 1
  ref = Ca_element
FEATURE [App::DocumentObjectGroupPython] S_element007  label="S_element : 002"  # scripted group (container) (typed FeaturePython)
  n = 1
  ref = S_element
FEATURE [App::DocumentObjectGroupPython] O_element023  label="O_element : 011"  # scripted group (container) (typed FeaturePython)
  n = 4
  ref = O_element
FEATURE [App::DocumentObjectGroupPython] G4_CALCIUM_SULFATE  # scripted group (container) (typed FeaturePython)
  Dunit = g/cm3
  Dvalue = 2.96
  Group = -> [Ca_element008,S_element007,O_element023]
  conduct = 2
  density = 1
  expand = 3
  formula = G4_CALCIUM_SULFATE
  name = G4_CALCIUM_SULFATE
  specific = 4
FEATURE [App::DocumentObjectGroupPython] Ca_element009  label="Ca_element : 005"  # scripted group (container) (typed FeaturePython)
  n = 1
  ref = Ca_element
FEATURE [App::DocumentObjectGroupPython] W_element002  label="W_element : 002"  # scripted group (container) (typed FeaturePython)
  n = 1
  ref = W_element
FEATURE [App::DocumentObjectGroupPython] O_element024  label="O_element : 012"  # scripted group (container) (typed FeaturePython)
  n = 4
  ref = O_element
FEATURE [App::DocumentObjectGroupPython] G4_CALCIUM_TUNGSTATE  # scripted group (container) (typed FeaturePython)
  Dunit = g/cm3
  Dvalue = 6.062
  Group = -> [Ca_element009,W_element002,O_element024]
  conduct = 2
  density = 1
  expand = 3
  formula = G4_CALCIUM_TUNGSTATE
  name = G4_CALCIUM_TUNGSTATE
  specific = 4
FEATURE [App::DocumentObjectGroupPython] C_element023  label="C_element : 010"  # scripted group (container) (typed FeaturePython)
  n = 1
  ref = C_element
FEATURE [App::DocumentObjectGroupPython] O_element025  label="O_element : 013"  # scripted group (container) (typed FeaturePython)
  n = 2
  ref = O_element
FEATURE [App::DocumentObjectGroupPython] G4_CARBON_DIOXIDE  # scripted group (container) (typed FeaturePython)
  Dunit = g/cm3
  Dvalue = 0.00184212
  Group = -> [C_element023,O_element025]
  conduct = 2
  density = 1
  expand = 3
  formula = G4_CARBON_DIOXIDE
  name = G4_CARBON_DIOXIDE
  specific = 4
FEATURE [App::DocumentObjectGroupPython] C_element024  label="C_element : 011"  # scripted group (container) (typed FeaturePython)
  n = 1
  ref = C_element
FEATURE [App::DocumentObjectGroupPython] Cl_element004  label="Cl_element : 4"  # scripted group (container) (typed FeaturePython)
  n = 4
  ref = Cl_element
FEATURE [App::DocumentObjectGroupPython] G4_CARBON_TETRACHLORIDE  # scripted group (container) (typed FeaturePython)
  Dunit = g/cm3
  Dvalue = 1.594
  Group = -> [C_element024,Cl_element004]
  conduct = 2
  density = 1
  expand = 3
  formula = G4_CARBON_TETRACHLORIDE
  name = G4_CARBON_TETRACHLORIDE
  specific = 4
FEATURE [App::DocumentObjectGroupPython] C_element025  label="C_element : 012"  # scripted group (container) (typed FeaturePython)
  n = 6
  ref = C_element
FEATURE [App::DocumentObjectGroupPython] H_element021  label="H_element : 012"  # scripted group (container) (typed FeaturePython)
  n = 10
  ref = H_element
FEATURE [App::DocumentObjectGroupPython] O_element026  label="O_element : 5"  # scripted group (container) (typed FeaturePython)
  n = 5
  ref = O_element
FEATURE [App::DocumentObjectGroupPython] G4_CELLULOSE_CELLOPHANE  # scripted group (container) (typed FeaturePython)
  Dunit = g/cm3
  Dvalue = 1.42
  Group = -> [C_element025,H_element021,O_element026]
  conduct = 2
  density = 1
  expand = 3
  formula = G4_CELLULOSE_CELLOPHANE
  name = G4_CELLULOSE_CELLOPHANE
  specific = 4
FEATURE [App::DocumentObjectGroupPython] H_element022  label="H_element : 0.067"  # scripted group (container) (typed FeaturePython)
  n = 0.067125
FEATURE [App::DocumentObjectGroupPython] C_element026  label="C_element : 0.545"  # scripted group (container) (typed FeaturePython)
  n = 0.545403
FEATURE [App::DocumentObjectGroupPython] O_element027  label="O_element : 0.387"  # scripted group (container) (typed FeaturePython)
  n = 0.387472
FEATURE [App::DocumentObjectGroupPython] G4_CELLULOSE_BUTYRATE  # scripted group (container) (typed FeaturePython)
  Dunit = g/cm3
  Dvalue = 1.2
  Group = -> [H_element022,C_element026,O_element027]
  conduct = 2
  density = 1
  expand = 3
  formula = G4_CELLULOSE_BUTYRATE
  name = G4_CELLULOSE_BUTYRATE
  specific = 4
FEATURE [App::DocumentObjectGroupPython] H_element023  label="H_element : 0.029"  # scripted group (container) (typed FeaturePython)
  n = 0.029216
FEATURE [App::DocumentObjectGroupPython] C_element027  label="C_element : 0.271"  # scripted group (container) (typed FeaturePython)
  n = 0.271296
FEATURE [App::DocumentObjectGroupPython] N_element013  label="N_element : 0.121"  # scripted group (container) (typed FeaturePython)
  n = 0.121276
FEATURE [App::DocumentObjectGroupPython] O_element028  label="O_element : 0.578"  # scripted group (container) (typed FeaturePython)
  n = 0.578212
FEATURE [App::DocumentObjectGroupPython] G4_CELLULOSE_NITRATE  # scripted group (container) (typed FeaturePython)
  Dunit = g/cm3
  Dvalue = 1.49
  Group = -> [H_element023,C_element027,N_element013,O_element028]
  conduct = 2
  density = 1
  expand = 3
  formula = G4_CELLULOSE_NITRATE
  name = G4_CELLULOSE_NITRATE
  specific = 4
FEATURE [App::DocumentObjectGroupPython] H_element024  label="H_element : 0.108"  # scripted group (container) (typed FeaturePython)
  n = 0.107596
FEATURE [App::DocumentObjectGroupPython] N_element014  label="N_element : 0.001"  # scripted group (container) (typed FeaturePython)
  n = 0.0008
FEATURE [App::DocumentObjectGroupPython] O_element029  label="O_element : 0.875"  # scripted group (container) (typed FeaturePython)
  n = 0.874976
FEATURE [App::DocumentObjectGroupPython] S_element008  label="S_element : 0.015"  # scripted group (container) (typed FeaturePython)
  n = 0.014627
FEATURE [App::DocumentObjectGroupPython] Ce_element001  label="Ce_element : 0.002"  # scripted group (container) (typed FeaturePython)
  n = 0.002001
FEATURE [App::DocumentObjectGroupPython] G4_CERIC_SULFATE  # scripted group (container) (typed FeaturePython)
  Dunit = g/cm3
  Dvalue = 1.03
  Group = -> [H_element024,N_element014,O_element029,S_element008,Ce_element001]
  conduct = 2
  density = 1
  expand = 3
  formula = G4_CERIC_SULFATE
  name = G4_CERIC_SULFATE
  specific = 4
FEATURE [App::DocumentObjectGroupPython] Cs_element001  label="Cs_element : 1"  # scripted group (container) (typed FeaturePython)
  n = 1
  ref = Cs_element
FEATURE [App::DocumentObjectGroupPython] F_element006  label="F_element : 1"  # scripted group (container) (typed FeaturePython)
  n = 1
  ref = F_element
FEATURE [App::DocumentObjectGroupPython] G4_CESIUM_FLUORIDE  # scripted group (container) (typed FeaturePython)
  Dunit = g/cm3
  Dvalue = 4.115
  Group = -> [Cs_element001,F_element006]
  conduct = 2
  density = 1
  expand = 3
  formula = G4_CESIUM_FLUORIDE
  name = G4_CESIUM_FLUORIDE
  specific = 4
FEATURE [App::DocumentObjectGroupPython] Cs_element002  label="Cs_element : 002"  # scripted group (container) (typed FeaturePython)
  n = 1
  ref = Cs_element
FEATURE [App::DocumentObjectGroupPython] I_element001  label="I_element : 1"  # scripted group (container) (typed FeaturePython)
  n = 1
  ref = I_element
FEATURE [App::DocumentObjectGroupPython] G4_CESIUM_IODIDE  # scripted group (container) (typed FeaturePython)
  Dunit = g/cm3
  Dvalue = 4.51
  Group = -> [Cs_element002,I_element001]
  conduct = 2
  density = 1
  expand = 3
  formula = G4_CESIUM_IODIDE
  name = G4_CESIUM_IODIDE
  specific = 4
FEATURE [App::DocumentObjectGroupPython] C_element028  label="C_element : 013"  # scripted group (container) (typed FeaturePython)
  n = 6
  ref = C_element
FEATURE [App::DocumentObjectGroupPython] H_element025  label="H_element : 013"  # scripted group (container) (typed FeaturePython)
  n = 5
  ref = H_element
FEATURE [App::DocumentObjectGroupPython] Cl_element005  label="Cl_element : 1"  # scripted group (container) (typed FeaturePython)
  n = 1
  ref = Cl_element
FEATURE [App::DocumentObjectGroupPython] G4_CHLOROBENZENE  # scripted group (container) (typed FeaturePython)
  Dunit = g/cm3
  Dvalue = 1.1058
  Group = -> [C_element028,H_element025,Cl_element005]
  conduct = 2
  density = 1
  expand = 3
  formula = G4_CHLOROBENZENE
  name = G4_CHLOROBENZENE
  specific = 4
FEATURE [App::DocumentObjectGroupPython] C_element029  label="C_element : 014"  # scripted group (container) (typed FeaturePython)
  n = 1
  ref = C_element
FEATURE [App::DocumentObjectGroupPython] H_element026  label="H_element : 1"  # scripted group (container) (typed FeaturePython)
  n = 1
  ref = H_element
FEATURE [App::DocumentObjectGroupPython] Cl_element006  label="Cl_element : 3"  # scripted group (container) (typed FeaturePython)
  n = 3
  ref = Cl_element
FEATURE [App::DocumentObjectGroupPython] G4_CHLOROFORM  # scripted group (container) (typed FeaturePython)
  Dunit = g/cm3
  Dvalue = 1.4832
  Group = -> [C_element029,H_element026,Cl_element006]
  conduct = 2
  density = 1
  expand = 3
  formula = G4_CHLOROFORM
  name = G4_CHLOROFORM
  specific = 4
FEATURE [App::DocumentObjectGroupPython] H_element027  label="H_element : 0.010"  # scripted group (container) (typed FeaturePython)
  n = 0.01
FEATURE [App::DocumentObjectGroupPython] C_element030  label="C_element : 0.001"  # scripted group (container) (typed FeaturePython)
  n = 0.001
FEATURE [App::DocumentObjectGroupPython] O_element030  label="O_element : 0.529"  # scripted group (container) (typed FeaturePython)
  n = 0.529107
FEATURE [App::DocumentObjectGroupPython] Na_element005  label="Na_element : 0.016"  # scripted group (container) (typed FeaturePython)
  n = 0.016
FEATURE [App::DocumentObjectGroupPython] Mg_element003  label="Mg_element : 0.004"  # scripted group (container) (typed FeaturePython)
  n = 0.002
FEATURE [App::DocumentObjectGroupPython] Al_element002  label="Al_element : 0.034"  # scripted group (container) (typed FeaturePython)
  n = 0.033872
FEATURE [App::DocumentObjectGroupPython] Si_element002  label="Si_element : 0.337"  # scripted group (container) (typed FeaturePython)
  n = 0.337021
FEATURE [App::DocumentObjectGroupPython] K_element003  label="K_element : 0.013"  # scripted group (container) (typed FeaturePython)
  n = 0.013
FEATURE [App::DocumentObjectGroupPython] Ca_element010  label="Ca_element : 0.044"  # scripted group (container) (typed FeaturePython)
  n = 0.044
FEATURE [App::DocumentObjectGroupPython] Fe_element002  label="Fe_element : 0.014"  # scripted group (container) (typed FeaturePython)
  n = 0.014
FEATURE [App::DocumentObjectGroupPython] G4_CONCRETE  # scripted group (container) (typed FeaturePython)
  Dunit = g/cm3
  Dvalue = 2.3
  Group = -> [H_element027,C_element030,O_element030,Na_element005,Mg_element003,Al_element002,Si_element002,K_element003,Ca_element010,Fe_element002]
  conduct = 2
  density = 1
  expand = 3
  formula = G4_CONCRETE
  name = G4_CONCRETE
  specific = 4
FEATURE [App::DocumentObjectGroupPython] C_element031  label="C_element : 015"  # scripted group (container) (typed FeaturePython)
  n = 6
  ref = C_element
FEATURE [App::DocumentObjectGroupPython] H_element028  label="H_element : 12"  # scripted group (container) (typed FeaturePython)
  n = 12
  ref = H_element
FEATURE [App::DocumentObjectGroupPython] G4_CYCLOHEXANE  # scripted group (container) (typed FeaturePython)
  Dunit = g/cm3
  Dvalue = 0.779
  Group = -> [C_element031,H_element028]
  conduct = 2
  density = 1
  expand = 3
  formula = G4_CYCLOHEXANE
  name = G4_CYCLOHEXANE
  specific = 4
FEATURE [App::DocumentObjectGroupPython] C_element032  label="C_element : 016"  # scripted group (container) (typed FeaturePython)
  n = 6
  ref = C_element
FEATURE [App::DocumentObjectGroupPython] H_element029  label="H_element : 4"  # scripted group (container) (typed FeaturePython)
  n = 4
  ref = H_element
FEATURE [App::DocumentObjectGroupPython] Cl_element007  label="Cl_element : 2"  # scripted group (container) (typed FeaturePython)
  n = 2
  ref = Cl_element
FEATURE [App::DocumentObjectGroupPython] G4_1_2_DICHLOROBENZENE  label="G4_1.2-DICHLOROBENZENE"  # scripted group (container) (typed FeaturePython)
  Dunit = g/cm3
  Dvalue = 1.3048
  Group = -> [C_element032,H_element029,Cl_element007]
  conduct = 2
  density = 1
  expand = 3
  formula = G4_1.2-DICHLOROBENZENE
  name = G4_1.2-DICHLOROBENZENE
  specific = 4
FEATURE [App::DocumentObjectGroupPython] C_element033  label="C_element : 017"  # scripted group (container) (typed FeaturePython)
  n = 4
  ref = C_element
FEATURE [App::DocumentObjectGroupPython] H_element030  label="H_element : 8"  # scripted group (container) (typed FeaturePython)
  n = 8
  ref = H_element
FEATURE [App::DocumentObjectGroupPython] O_element031  label="O_element : 014"  # scripted group (container) (typed FeaturePython)
  n = 1
  ref = O_element
FEATURE [App::DocumentObjectGroupPython] Cl_element008  label="Cl_element : 005"  # scripted group (container) (typed FeaturePython)
  n = 2
  ref = Cl_element
FEATURE [App::DocumentObjectGroupPython] G4_DICHLORODIETHYL_ETHER  # scripted group (container) (typed FeaturePython)
  Dunit = g/cm3
  Dvalue = 1.2199
  Group = -> [C_element033,H_element030,O_element031,Cl_element008]
  conduct = 2
  density = 1
  expand = 3
  formula = G4_DICHLORODIETHYL_ETHER
  name = G4_DICHLORODIETHYL_ETHER
  specific = 4
FEATURE [App::DocumentObjectGroupPython] C_element034  label="C_element : 018"  # scripted group (container) (typed FeaturePython)
  n = 2
  ref = C_element
FEATURE [App::DocumentObjectGroupPython] H_element031  label="H_element : 014"  # scripted group (container) (typed FeaturePython)
  n = 4
  ref = H_element
FEATURE [App::DocumentObjectGroupPython] Cl_element009  label="Cl_element : 006"  # scripted group (container) (typed FeaturePython)
  n = 2
  ref = Cl_element
FEATURE [App::DocumentObjectGroupPython] G4_1_2_DICHLOROETHANE  label="G4_1.2-DICHLOROETHANE"  # scripted group (container) (typed FeaturePython)
  Dunit = g/cm3
  Dvalue = 1.2351
  Group = -> [C_element034,H_element031,Cl_element009]
  conduct = 2
  density = 1
  expand = 3
  formula = G4_1.2-DICHLOROETHANE
  name = G4_1.2-DICHLOROETHANE
  specific = 4
FEATURE [App::DocumentObjectGroupPython] C_element035  label="C_element : 019"  # scripted group (container) (typed FeaturePython)
  n = 4
  ref = C_element
FEATURE [App::DocumentObjectGroupPython] H_element032  label="H_element : 015"  # scripted group (container) (typed FeaturePython)
  n = 10
  ref = H_element
FEATURE [App::DocumentObjectGroupPython] O_element032  label="O_element : 015"  # scripted group (container) (typed FeaturePython)
  n = 1
  ref = O_element
FEATURE [App::DocumentObjectGroupPython] G4_DIETHYL_ETHER  # scripted group (container) (typed FeaturePython)
  Dunit = g/cm3
  Dvalue = 0.71378
  Group = -> [C_element035,H_element032,O_element032]
  conduct = 2
  density = 1
  expand = 3
  formula = G4_DIETHYL_ETHER
  name = G4_DIETHYL_ETHER
  specific = 4
FEATURE [App::DocumentObjectGroupPython] C_element036  label="C_element : 020"  # scripted group (container) (typed FeaturePython)
  n = 3
  ref = C_element
FEATURE [App::DocumentObjectGroupPython] H_element033  label="H_element : 016"  # scripted group (container) (typed FeaturePython)
  n = 7
  ref = H_element
FEATURE [App::DocumentObjectGroupPython] N_element015  label="N_element : 008"  # scripted group (container) (typed FeaturePython)
  n = 1
  ref = N_element
FEATURE [App::DocumentObjectGroupPython] O_element033  label="O_element : 016"  # scripted group (container) (typed FeaturePython)
  n = 1
  ref = O_element
FEATURE [App::DocumentObjectGroupPython] G4_N_N_DIMETHYL_FORMAMIDE  label="G4_N.N-DIMETHYL_FORMAMIDE"  # scripted group (container) (typed FeaturePython)
  Dunit = g/cm3
  Dvalue = 0.9487
  Group = -> [C_element036,H_element033,N_element015,O_element033]
  conduct = 2
  density = 1
  expand = 3
  formula = G4_N.N-DIMETHYL_FORMAMIDE
  name = G4_N.N-DIMETHYL_FORMAMIDE
  specific = 4
FEATURE [App::DocumentObjectGroupPython] C_element037  label="C_element : 021"  # scripted group (container) (typed FeaturePython)
  n = 2
  ref = C_element
FEATURE [App::DocumentObjectGroupPython] H_element034  label="H_element : 017"  # scripted group (container) (typed FeaturePython)
  n = 6
  ref = H_element
FEATURE [App::DocumentObjectGroupPython] O_element034  label="O_element : 017"  # scripted group (container) (typed FeaturePython)
  n = 1
  ref = O_element
FEATURE [App::DocumentObjectGroupPython] S_element009  label="S_element : 003"  # scripted group (container) (typed FeaturePython)
  n = 1
  ref = S_element
FEATURE [App::DocumentObjectGroupPython] G4_DIMETHYL_SULFOXIDE  # scripted group (container) (typed FeaturePython)
  Dunit = g/cm3
  Dvalue = 1.1014
  Group = -> [C_element037,H_element034,O_element034,S_element009]
  conduct = 2
  density = 1
  expand = 3
  formula = G4_DIMETHYL_SULFOXIDE
  name = G4_DIMETHYL_SULFOXIDE
  specific = 4
FEATURE [App::DocumentObjectGroupPython] C_element038  label="C_element : 022"  # scripted group (container) (typed FeaturePython)
  n = 2
  ref = C_element
FEATURE [App::DocumentObjectGroupPython] H_element035  label="H_element : 018"  # scripted group (container) (typed FeaturePython)
  n = 6
  ref = H_element
FEATURE [App::DocumentObjectGroupPython] G4_ETHANE  # scripted group (container) (typed FeaturePython)
  Dunit = g/cm3
  Dvalue = 0.00125324
  Group = -> [C_element038,H_element035]
  conduct = 2
  density = 1
  expand = 3
  formula = G4_ETHANE
  name = G4_ETHANE
  specific = 4
FEATURE [App::DocumentObjectGroupPython] C_element039  label="C_element : 023"  # scripted group (container) (typed FeaturePython)
  n = 2
  ref = C_element
FEATURE [App::DocumentObjectGroupPython] H_element036  label="H_element : 019"  # scripted group (container) (typed FeaturePython)
  n = 6
  ref = H_element
FEATURE [App::DocumentObjectGroupPython] O_element035  label="O_element : 018"  # scripted group (container) (typed FeaturePython)
  n = 1
  ref = O_element
FEATURE [App::DocumentObjectGroupPython] G4_ETHYL_ALCOHOL  # scripted group (container) (typed FeaturePython)
  Dunit = g/cm3
  Dvalue = 0.7893
  Group = -> [C_element039,H_element036,O_element035]
  conduct = 2
  density = 1
  expand = 3
  formula = G4_ETHYL_ALCOHOL
  name = G4_ETHYL_ALCOHOL
  specific = 4
FEATURE [App::DocumentObjectGroupPython] H_element037  label="H_element : 0.090"  # scripted group (container) (typed FeaturePython)
  n = 0.090027
FEATURE [App::DocumentObjectGroupPython] C_element040  label="C_element : 0.585"  # scripted group (container) (typed FeaturePython)
  n = 0.585182
FEATURE [App::DocumentObjectGroupPython] O_element036  label="O_element : 0.325"  # scripted group (container) (typed FeaturePython)
  n = 0.324791
FEATURE [App::DocumentObjectGroupPython] G4_ETHYL_CELLULOSE  # scripted group (container) (typed FeaturePython)
  Dunit = g/cm3
  Dvalue = 1.13
  Group = -> [H_element037,C_element040,O_element036]
  conduct = 2
  density = 1
  expand = 3
  formula = G4_ETHYL_CELLULOSE
  name = G4_ETHYL_CELLULOSE
  specific = 4
FEATURE [App::DocumentObjectGroupPython] C_element041  label="C_element : 024"  # scripted group (container) (typed FeaturePython)
  n = 2
  ref = C_element
FEATURE [App::DocumentObjectGroupPython] H_element038  label="H_element : 020"  # scripted group (container) (typed FeaturePython)
  n = 4
  ref = H_element
FEATURE [App::DocumentObjectGroupPython] G4_ETHYLENE  # scripted group (container) (typed FeaturePython)
  Dunit = g/cm3
  Dvalue = 0.00117497
  Group = -> [C_element041,H_element038]
  conduct = 2
  density = 1
  expand = 3
  formula = G4_ETHYLENE
  name = G4_ETHYLENE
  specific = 4
FEATURE [App::DocumentObjectGroupPython] H_element039  label="H_element : 0.096"  # scripted group (container) (typed FeaturePython)
  n = 0.096
FEATURE [App::DocumentObjectGroupPython] C_element042  label="C_element : 0.195"  # scripted group (container) (typed FeaturePython)
  n = 0.195
FEATURE [App::DocumentObjectGroupPython] N_element016  label="N_element : 0.057"  # scripted group (container) (typed FeaturePython)
  n = 0.057
FEATURE [App::DocumentObjectGroupPython] O_element037  label="O_element : 0.646"  # scripted group (container) (typed FeaturePython)
  n = 0.646
FEATURE [App::DocumentObjectGroupPython] Na_element006  label="Na_element : 0.017"  # scripted group (container) (typed FeaturePython)
  n = 0.001
FEATURE [App::DocumentObjectGroupPython] P_element005  label="P_element : 0.104"  # scripted group (container) (typed FeaturePython)
  n = 0.001
FEATURE [App::DocumentObjectGroupPython] S_element010  label="S_element : 0.016"  # scripted group (container) (typed FeaturePython)
  n = 0.003
FEATURE [App::DocumentObjectGroupPython] Cl_element010  label="Cl_element : 0.005"  # scripted group (container) (typed FeaturePython)
  n = 0.001
FEATURE [App::DocumentObjectGroupPython] G4_EYE_LENS_ICRP  # scripted group (container) (typed FeaturePython)
  Dunit = g/cm3
  Dvalue = 1.07
  Group = -> [H_element039,C_element042,N_element016,O_element037,Na_element006,P_element005,S_element010,Cl_element010]
  conduct = 2
  density = 1
  expand = 3
  formula = G4_EYE_LENS_ICRP
  name = G4_EYE_LENS_ICRP
  specific = 4
FEATURE [App::DocumentObjectGroupPython] Fe_element003  label="Fe_element : 2"  # scripted group (container) (typed FeaturePython)
  n = 2
  ref = Fe_element
FEATURE [App::DocumentObjectGroupPython] O_element038  label="O_element : 019"  # scripted group (container) (typed FeaturePython)
  n = 3
  ref = O_element
FEATURE [App::DocumentObjectGroupPython] G4_FERRIC_OXIDE  # scripted group (container) (typed FeaturePython)
  Dunit = g/cm3
  Dvalue = 5.2
  Group = -> [Fe_element003,O_element038]
  conduct = 2
  density = 1
  expand = 3
  formula = G4_FERRIC_OXIDE
  name = G4_FERRIC_OXIDE
  specific = 4
FEATURE [App::DocumentObjectGroupPython] Fe_element004  label="Fe_element : 1"  # scripted group (container) (typed FeaturePython)
  n = 1
  ref = Fe_element
FEATURE [App::DocumentObjectGroupPython] B_element003  label="B_element : 1"  # scripted group (container) (typed FeaturePython)
  n = 1
  ref = B_element
FEATURE [App::DocumentObjectGroupPython] G4_FERROBORIDE  # scripted group (container) (typed FeaturePython)
  Dunit = g/cm3
  Dvalue = 7.15
  Group = -> [Fe_element004,B_element003]
  conduct = 2
  density = 1
  expand = 3
  formula = G4_FERROBORIDE
  name = G4_FERROBORIDE
  specific = 4
FEATURE [App::DocumentObjectGroupPython] Fe_element005  label="Fe_element : 003"  # scripted group (container) (typed FeaturePython)
  n = 1
  ref = Fe_element
FEATURE [App::DocumentObjectGroupPython] O_element039  label="O_element : 020"  # scripted group (container) (typed FeaturePython)
  n = 1
  ref = O_element
FEATURE [App::DocumentObjectGroupPython] G4_FERROUS_OXIDE  # scripted group (container) (typed FeaturePython)
  Dunit = g/cm3
  Dvalue = 5.7
  Group = -> [Fe_element005,O_element039]
  conduct = 2
  density = 1
  expand = 3
  formula = G4_FERROUS_OXIDE
  name = G4_FERROUS_OXIDE
  specific = 4
FEATURE [App::DocumentObjectGroupPython] H_element040  label="H_element : 0.115"  # scripted group (container) (typed FeaturePython)
  n = 0.108259
FEATURE [App::DocumentObjectGroupPython] N_element017  label="N_element : 0.000"  # scripted group (container) (typed FeaturePython)
  n = 2.7e-05
FEATURE [App::DocumentObjectGroupPython] O_element040  label="O_element : 0.879"  # scripted group (container) (typed FeaturePython)
  n = 0.878636
FEATURE [App::DocumentObjectGroupPython] Na_element007  label="Na_element : 0.000"  # scripted group (container) (typed FeaturePython)
  n = 2.2e-05
FEATURE [App::DocumentObjectGroupPython] S_element011  label="S_element : 0.013"  # scripted group (container) (typed FeaturePython)
  n = 0.012968
FEATURE [App::DocumentObjectGroupPython] Cl_element011  label="Cl_element : 0.000"  # scripted group (container) (typed FeaturePython)
  n = 3.4e-05
FEATURE [App::DocumentObjectGroupPython] Fe_element006  label="Fe_element : 0.000"  # scripted group (container) (typed FeaturePython)
  n = 5.4e-05
FEATURE [App::DocumentObjectGroupPython] G4_FERROUS_SULFATE  # scripted group (container) (typed FeaturePython)
  Dunit = g/cm3
  Dvalue = 1.024
  Group = -> [H_element040,N_element017,O_element040,Na_element007,S_element011,Cl_element011,Fe_element006]
  conduct = 2
  density = 1
  expand = 3
  formula = G4_FERROUS_SULFATE
  name = G4_FERROUS_SULFATE
  specific = 4
FEATURE [App::DocumentObjectGroupPython] C_element043  label="C_element : 0.099"  # scripted group (container) (typed FeaturePython)
  n = 0.099335
FEATURE [App::DocumentObjectGroupPython] F_element007  label="F_element : 0.314"  # scripted group (container) (typed FeaturePython)
  n = 0.314247
FEATURE [App::DocumentObjectGroupPython] Cl_element012  label="Cl_element : 0.586"  # scripted group (container) (typed FeaturePython)
  n = 0.586418
FEATURE [App::DocumentObjectGroupPython] G4_FREON_12  label="G4_FREON-12"  # scripted group (container) (typed FeaturePython)
  Dunit = g/cm3
  Dvalue = 1.12
  Group = -> [C_element043,F_element007,Cl_element012]
  conduct = 2
  density = 1
  expand = 3
  formula = G4_FREON-12
  name = G4_FREON-12
  specific = 4
FEATURE [App::DocumentObjectGroupPython] C_element044  label="C_element : 0.057"  # scripted group (container) (typed FeaturePython)
  n = 0.057245
FEATURE [App::DocumentObjectGroupPython] F_element008  label="F_element : 0.181"  # scripted group (container) (typed FeaturePython)
  n = 0.181096
FEATURE [App::DocumentObjectGroupPython] Br_element001  label="Br_element : 0.762"  # scripted group (container) (typed FeaturePython)
  n = 0.761659
FEATURE [App::DocumentObjectGroupPython] G4_FREON_12B2  label="G4_FREON-12B2"  # scripted group (container) (typed FeaturePython)
  Dunit = g/cm3
  Dvalue = 1.8
  Group = -> [C_element044,F_element008,Br_element001]
  conduct = 2
  density = 1
  expand = 3
  formula = G4_FREON-12B2
  name = G4_FREON-12B2
  specific = 4
FEATURE [App::DocumentObjectGroupPython] C_element045  label="C_element : 0.115"  # scripted group (container) (typed FeaturePython)
  n = 0.114983
FEATURE [App::DocumentObjectGroupPython] F_element009  label="F_element : 0.546"  # scripted group (container) (typed FeaturePython)
  n = 0.545621
FEATURE [App::DocumentObjectGroupPython] Cl_element013  label="Cl_element : 0.339"  # scripted group (container) (typed FeaturePython)
  n = 0.339396
FEATURE [App::DocumentObjectGroupPython] G4_FREON_13  label="G4_FREON-13"  # scripted group (container) (typed FeaturePython)
  Dunit = g/cm3
  Dvalue = 0.95
  Group = -> [C_element045,F_element009,Cl_element013]
  conduct = 2
  density = 1
  expand = 3
  formula = G4_FREON-13
  name = G4_FREON-13
  specific = 4
FEATURE [App::DocumentObjectGroupPython] C_element046  label="C_element : 025"  # scripted group (container) (typed FeaturePython)
  n = 1
  ref = C_element
FEATURE [App::DocumentObjectGroupPython] F_element010  label="F_element : 3"  # scripted group (container) (typed FeaturePython)
  n = 3
  ref = F_element
FEATURE [App::DocumentObjectGroupPython] Br_element002  label="Br_element : 1"  # scripted group (container) (typed FeaturePython)
  n = 1
  ref = Br_element
FEATURE [App::DocumentObjectGroupPython] G4_FREON_13B1  label="G4_FREON-13B1"  # scripted group (container) (typed FeaturePython)
  Dunit = g/cm3
  Dvalue = 1.5
  Group = -> [C_element046,F_element010,Br_element002]
  conduct = 2
  density = 1
  expand = 3
  formula = G4_FREON-13B1
  name = G4_FREON-13B1
  specific = 4
FEATURE [App::DocumentObjectGroupPython] C_element047  label="C_element : 0.061"  # scripted group (container) (typed FeaturePython)
  n = 0.061309
FEATURE [App::DocumentObjectGroupPython] F_element011  label="F_element : 0.291"  # scripted group (container) (typed FeaturePython)
  n = 0.290924
FEATURE [App::DocumentObjectGroupPython] I_element002  label="I_element : 0.648"  # scripted group (container) (typed FeaturePython)
  n = 0.647767
FEATURE [App::DocumentObjectGroupPython] G4_FREON_13I1  label="G4_FREON-13I1"  # scripted group (container) (typed FeaturePython)
  Dunit = g/cm3
  Dvalue = 1.8
  Group = -> [C_element047,F_element011,I_element002]
  conduct = 2
  density = 1
  expand = 3
  formula = G4_FREON-13I1
  name = G4_FREON-13I1
  specific = 4
FEATURE [App::DocumentObjectGroupPython] Gd_element001  label="Gd_element : 2"  # scripted group (container) (typed FeaturePython)
  n = 2
  ref = Gd_element
FEATURE [App::DocumentObjectGroupPython] O_element041  label="O_element : 021"  # scripted group (container) (typed FeaturePython)
  n = 2
  ref = O_element
FEATURE [App::DocumentObjectGroupPython] S_element012  label="S_element : 004"  # scripted group (container) (typed FeaturePython)
  n = 1
  ref = S_element
FEATURE [App::DocumentObjectGroupPython] G4_GADOLINIUM_OXYSULFIDE  # scripted group (container) (typed FeaturePython)
  Dunit = g/cm3
  Dvalue = 7.44
  Group = -> [Gd_element001,O_element041,S_element012]
  conduct = 2
  density = 1
  expand = 3
  formula = G4_GADOLINIUM_OXYSULFIDE
  name = G4_GADOLINIUM_OXYSULFIDE
  specific = 4
FEATURE [App::DocumentObjectGroupPython] Ga_element001  label="Ga_element : 1"  # scripted group (container) (typed FeaturePython)
  n = 1
  ref = Ga_element
FEATURE [App::DocumentObjectGroupPython] As_element001  label="As_element : 1"  # scripted group (container) (typed FeaturePython)
  n = 1
  ref = As_element
FEATURE [App::DocumentObjectGroupPython] G4_GALLIUM_ARSENIDE  # scripted group (container) (typed FeaturePython)
  Dunit = g/cm3
  Dvalue = 5.31
  Group = -> [Ga_element001,As_element001]
  conduct = 2
  density = 1
  expand = 3
  formula = G4_GALLIUM_ARSENIDE
  name = G4_GALLIUM_ARSENIDE
  specific = 4
FEATURE [App::DocumentObjectGroupPython] H_element041  label="H_element : 0.081"  # scripted group (container) (typed FeaturePython)
  n = 0.08118
FEATURE [App::DocumentObjectGroupPython] C_element048  label="C_element : 0.416"  # scripted group (container) (typed FeaturePython)
  n = 0.41606
FEATURE [App::DocumentObjectGroupPython] N_element018  label="N_element : 0.111"  # scripted group (container) (typed FeaturePython)
  n = 0.11124
FEATURE [App::DocumentObjectGroupPython] O_element042  label="O_element : 0.381"  # scripted group (container) (typed FeaturePython)
  n = 0.38064
FEATURE [App::DocumentObjectGroupPython] S_element013  label="S_element : 0.011"  # scripted group (container) (typed FeaturePython)
  n = 0.01088
FEATURE [App::DocumentObjectGroupPython] G4_GEL_PHOTO_EMULSION  # scripted group (container) (typed FeaturePython)
  Dunit = g/cm3
  Dvalue = 1.2914
  Group = -> [H_element041,C_element048,N_element018,O_element042,S_element013]
  conduct = 2
  density = 1
  expand = 3
  formula = G4_GEL_PHOTO_EMULSION
  name = G4_GEL_PHOTO_EMULSION
  specific = 4
FEATURE [App::DocumentObjectGroupPython] B_element004  label="B_element : 0.040"  # scripted group (container) (typed FeaturePython)
  n = 0.0400639
FEATURE [App::DocumentObjectGroupPython] O_element043  label="O_element : 0.540"  # scripted group (container) (typed FeaturePython)
  n = 0.539561
FEATURE [App::DocumentObjectGroupPython] Na_element008  label="Na_element : 0.028"  # scripted group (container) (typed FeaturePython)
  n = 0.0281909
FEATURE [App::DocumentObjectGroupPython] Al_element003  label="Al_element : 0.012"  # scripted group (container) (typed FeaturePython)
  n = 0.011644
FEATURE [App::DocumentObjectGroupPython] Si_element003  label="Si_element : 0.377"  # scripted group (container) (typed FeaturePython)
  n = 0.377219
FEATURE [App::DocumentObjectGroupPython] K_element004  label="K_element : 0.014"  # scripted group (container) (typed FeaturePython)
  n = 0.00332099
FEATURE [App::DocumentObjectGroupPython] G4_Pyrex_Glass  # scripted group (container) (typed FeaturePython)
  Dunit = g/cm3
  Dvalue = 2.23
  Group = -> [B_element004,O_element043,Na_element008,Al_element003,Si_element003,K_element004]
  conduct = 2
  density = 1
  expand = 3
  formula = G4_Pyrex_Glass
  name = G4_Pyrex_Glass
  specific = 4
FEATURE [App::DocumentObjectGroupPython] O_element044  label="O_element : 0.156"  # scripted group (container) (typed FeaturePython)
  n = 0.156453
FEATURE [App::DocumentObjectGroupPython] Si_element004  label="Si_element : 0.081"  # scripted group (container) (typed FeaturePython)
  n = 0.080866
FEATURE [App::DocumentObjectGroupPython] Ti_element001  label="Ti_element : 0.008"  # scripted group (container) (typed FeaturePython)
  n = 0.008092
FEATURE [App::DocumentObjectGroupPython] As_element002  label="As_element : 0.003"  # scripted group (container) (typed FeaturePython)
  n = 0.002651
FEATURE [App::DocumentObjectGroupPython] Pb_element001  label="Pb_element : 0.752"  # scripted group (container) (typed FeaturePython)
  n = 0.751938
FEATURE [App::DocumentObjectGroupPython] G4_GLASS_LEAD  # scripted group (container) (typed FeaturePython)
  Dunit = g/cm3
  Dvalue = 6.22
  Group = -> [O_element044,Si_element004,Ti_element001,As_element002,Pb_element001]
  conduct = 2
  density = 1
  expand = 3
  formula = G4_GLASS_LEAD
  name = G4_GLASS_LEAD
  specific = 4
FEATURE [App::DocumentObjectGroupPython] O_element045  label="O_element : 0.460"  # scripted group (container) (typed FeaturePython)
  n = 0.4598
FEATURE [App::DocumentObjectGroupPython] Na_element009  label="Na_element : 0.096"  # scripted group (container) (typed FeaturePython)
  n = 0.0964411
FEATURE [App::DocumentObjectGroupPython] Si_element005  label="Si_element : 0.378"  # scripted group (container) (typed FeaturePython)
  n = 0.336553
FEATURE [App::DocumentObjectGroupPython] Ca_element011  label="Ca_element : 0.107"  # scripted group (container) (typed FeaturePython)
  n = 0.107205
FEATURE [App::DocumentObjectGroupPython] G4_GLASS_PLATE  # scripted group (container) (typed FeaturePython)
  Dunit = g/cm3
  Dvalue = 2.4
  Group = -> [O_element045,Na_element009,Si_element005,Ca_element011]
  conduct = 2
  density = 1
  expand = 3
  formula = G4_GLASS_PLATE
  name = G4_GLASS_PLATE
  specific = 4
FEATURE [App::DocumentObjectGroupPython] C_element049  label="C_element : 026"  # scripted group (container) (typed FeaturePython)
  n = 5
  ref = C_element
FEATURE [App::DocumentObjectGroupPython] H_element042  label="H_element : 021"  # scripted group (container) (typed FeaturePython)
  n = 10
  ref = H_element
FEATURE [App::DocumentObjectGroupPython] N_element019  label="N_element : 2"  # scripted group (container) (typed FeaturePython)
  n = 2
  ref = N_element
FEATURE [App::DocumentObjectGroupPython] O_element046  label="O_element : 022"  # scripted group (container) (typed FeaturePython)
  n = 3
  ref = O_element
FEATURE [App::DocumentObjectGroupPython] G4_GLUTAMINE  # scripted group (container) (typed FeaturePython)
  Dunit = g/cm3
  Dvalue = 1.46
  Group = -> [C_element049,H_element042,N_element019,O_element046]
  conduct = 2
  density = 1
  expand = 3
  formula = G4_GLUTAMINE
  name = G4_GLUTAMINE
  specific = 4
FEATURE [App::DocumentObjectGroupPython] C_element050  label="C_element : 027"  # scripted group (container) (typed FeaturePython)
  n = 3
  ref = C_element
FEATURE [App::DocumentObjectGroupPython] H_element043  label="H_element : 022"  # scripted group (container) (typed FeaturePython)
  n = 8
  ref = H_element
FEATURE [App::DocumentObjectGroupPython] O_element047  label="O_element : 023"  # scripted group (container) (typed FeaturePython)
  n = 3
  ref = O_element
FEATURE [App::DocumentObjectGroupPython] G4_GLYCEROL  # scripted group (container) (typed FeaturePython)
  Dunit = g/cm3
  Dvalue = 1.2613
  Group = -> [C_element050,H_element043,O_element047]
  conduct = 2
  density = 1
  expand = 3
  formula = G4_GLYCEROL
  name = G4_GLYCEROL
  specific = 4
FEATURE [App::DocumentObjectGroupPython] C_element051  label="C_element : 028"  # scripted group (container) (typed FeaturePython)
  n = 5
  ref = C_element
FEATURE [App::DocumentObjectGroupPython] H_element044  label="H_element : 023"  # scripted group (container) (typed FeaturePython)
  n = 5
  ref = H_element
FEATURE [App::DocumentObjectGroupPython] N_element020  label="N_element : 009"  # scripted group (container) (typed FeaturePython)
  n = 5
  ref = N_element
FEATURE [App::DocumentObjectGroupPython] O_element048  label="O_element : 024"  # scripted group (container) (typed FeaturePython)
  n = 1
  ref = O_element
FEATURE [App::DocumentObjectGroupPython] G4_GUANINE  # scripted group (container) (typed FeaturePython)
  Dunit = g/cm3
  Dvalue = 2.2
  Group = -> [C_element051,H_element044,N_element020,O_element048]
  conduct = 2
  density = 1
  expand = 3
  formula = G4_GUANINE
  name = G4_GUANINE
  specific = 4
FEATURE [App::DocumentObjectGroupPython] Ca_element012  label="Ca_element : 006"  # scripted group (container) (typed FeaturePython)
  n = 1
  ref = Ca_element
FEATURE [App::DocumentObjectGroupPython] S_element014  label="S_element : 005"  # scripted group (container) (typed FeaturePython)
  n = 1
  ref = S_element
FEATURE [App::DocumentObjectGroupPython] O_element049  label="O_element : 6"  # scripted group (container) (typed FeaturePython)
  n = 6
  ref = O_element
FEATURE [App::DocumentObjectGroupPython] H_element045  label="H_element : 024"  # scripted group (container) (typed FeaturePython)
  n = 4
  ref = H_element
FEATURE [App::DocumentObjectGroupPython] G4_GYPSUM  # scripted group (container) (typed FeaturePython)
  Dunit = g/cm3
  Dvalue = 2.32
  Group = -> [Ca_element012,S_element014,O_element049,H_element045]
  conduct = 2
  density = 1
  expand = 3
  formula = G4_GYPSUM
  name = G4_GYPSUM
  specific = 4
FEATURE [App::DocumentObjectGroupPython] C_element052  label="C_element : 7"  # scripted group (container) (typed FeaturePython)
  n = 7
  ref = C_element
FEATURE [App::DocumentObjectGroupPython] H_element046  label="H_element : 16"  # scripted group (container) (typed FeaturePython)
  n = 16
  ref = H_element
FEATURE [App::DocumentObjectGroupPython] G4_N_HEPTANE  label="G4_N-HEPTANE"  # scripted group (container) (typed FeaturePython)
  Dunit = g/cm3
  Dvalue = 0.68376
  Group = -> [C_element052,H_element046]
  conduct = 2
  density = 1
  expand = 3
  formula = G4_N-HEPTANE
  name = G4_N-HEPTANE
  specific = 4
FEATURE [App::DocumentObjectGroupPython] C_element053  label="C_element : 029"  # scripted group (container) (typed FeaturePython)
  n = 6
  ref = C_element
FEATURE [App::DocumentObjectGroupPython] H_element047  label="H_element : 14"  # scripted group (container) (typed FeaturePython)
  n = 14
  ref = H_element
FEATURE [App::DocumentObjectGroupPython] G4_N_HEXANE  label="G4_N-HEXANE"  # scripted group (container) (typed FeaturePython)
  Dunit = g/cm3
  Dvalue = 0.6603
  Group = -> [C_element053,H_element047]
  conduct = 2
  density = 1
  expand = 3
  formula = G4_N-HEXANE
  name = G4_N-HEXANE
  specific = 4
FEATURE [App::DocumentObjectGroupPython] C_element054  label="C_element : 22"  # scripted group (container) (typed FeaturePython)
  n = 22
  ref = C_element
FEATURE [App::DocumentObjectGroupPython] H_element048  label="H_element : 025"  # scripted group (container) (typed FeaturePython)
  n = 10
  ref = H_element
FEATURE [App::DocumentObjectGroupPython] N_element021  label="N_element : 010"  # scripted group (container) (typed FeaturePython)
  n = 2
  ref = N_element
FEATURE [App::DocumentObjectGroupPython] O_element050  label="O_element : 025"  # scripted group (container) (typed FeaturePython)
  n = 5
  ref = O_element
FEATURE [App::DocumentObjectGroupPython] G4_KAPTON  # scripted group (container) (typed FeaturePython)
  Dunit = g/cm3
  Dvalue = 1.42
  Group = -> [C_element054,H_element048,N_element021,O_element050]
  conduct = 2
  density = 1
  expand = 3
  formula = G4_KAPTON
  name = G4_KAPTON
  specific = 4
FEATURE [App::DocumentObjectGroupPython] La_element001  label="La_element : 1"  # scripted group (container) (typed FeaturePython)
  n = 1
  ref = La_element
FEATURE [App::DocumentObjectGroupPython] Br_element003  label="Br_element : 002"  # scripted group (container) (typed FeaturePython)
  n = 1
  ref = Br_element
FEATURE [App::DocumentObjectGroupPython] O_element051  label="O_element : 026"  # scripted group (container) (typed FeaturePython)
  n = 1
  ref = O_element
FEATURE [App::DocumentObjectGroupPython] G4_LANTHANUM_OXYBROMIDE  # scripted group (container) (typed FeaturePython)
  Dunit = g/cm3
  Dvalue = 6.28
  Group = -> [La_element001,Br_element003,O_element051]
  conduct = 2
  density = 1
  expand = 3
  formula = G4_LANTHANUM_OXYBROMIDE
  name = G4_LANTHANUM_OXYBROMIDE
  specific = 4
FEATURE [App::DocumentObjectGroupPython] La_element002  label="La_element : 2"  # scripted group (container) (typed FeaturePython)
  n = 2
  ref = La_element
FEATURE [App::DocumentObjectGroupPython] O_element052  label="O_element : 027"  # scripted group (container) (typed FeaturePython)
  n = 2
  ref = O_element
FEATURE [App::DocumentObjectGroupPython] S_element015  label="S_element : 006"  # scripted group (container) (typed FeaturePython)
  n = 1
  ref = S_element
FEATURE [App::DocumentObjectGroupPython] G4_LANTHANUM_OXYSULFIDE  # scripted group (container) (typed FeaturePython)
  Dunit = g/cm3
  Dvalue = 5.86
  Group = -> [La_element002,O_element052,S_element015]
  conduct = 2
  density = 1
  expand = 3
  formula = G4_LANTHANUM_OXYSULFIDE
  name = G4_LANTHANUM_OXYSULFIDE
  specific = 4
FEATURE [App::DocumentObjectGroupPython] O_element053  label="O_element : 0.072"  # scripted group (container) (typed FeaturePython)
  n = 0.071682
FEATURE [App::DocumentObjectGroupPython] Pb_element002  label="Pb_element : 0.928"  # scripted group (container) (typed FeaturePython)
  n = 0.928318
FEATURE [App::DocumentObjectGroupPython] G4_LEAD_OXIDE  # scripted group (container) (typed FeaturePython)
  Dunit = g/cm3
  Dvalue = 9.53
  Group = -> [O_element053,Pb_element002]
  conduct = 2
  density = 1
  expand = 3
  formula = G4_LEAD_OXIDE
  name = G4_LEAD_OXIDE
  specific = 4
FEATURE [App::DocumentObjectGroupPython] Li_element001  label="Li_element : 1"  # scripted group (container) (typed FeaturePython)
  n = 1
  ref = Li_element
FEATURE [App::DocumentObjectGroupPython] N_element022  label="N_element : 011"  # scripted group (container) (typed FeaturePython)
  n = 1
  ref = N_element
FEATURE [App::DocumentObjectGroupPython] H_element049  label="H_element : 026"  # scripted group (container) (typed FeaturePython)
  n = 2
  ref = H_element
FEATURE [App::DocumentObjectGroupPython] G4_LITHIUM_AMIDE  # scripted group (container) (typed FeaturePython)
  Dunit = g/cm3
  Dvalue = 1.178
  Group = -> [Li_element001,N_element022,H_element049]
  conduct = 2
  density = 1
  expand = 3
  formula = G4_LITHIUM_AMIDE
  name = G4_LITHIUM_AMIDE
  specific = 4
FEATURE [App::DocumentObjectGroupPython] Li_element002  label="Li_element : 2"  # scripted group (container) (typed FeaturePython)
  n = 2
  ref = Li_element
FEATURE [App::DocumentObjectGroupPython] C_element055  label="C_element : 030"  # scripted group (container) (typed FeaturePython)
  n = 1
  ref = C_element
FEATURE [App::DocumentObjectGroupPython] O_element054  label="O_element : 028"  # scripted group (container) (typed FeaturePython)
  n = 3
  ref = O_element
FEATURE [App::DocumentObjectGroupPython] G4_LITHIUM_CARBONATE  # scripted group (container) (typed FeaturePython)
  Dunit = g/cm3
  Dvalue = 2.11
  Group = -> [Li_element002,C_element055,O_element054]
  conduct = 2
  density = 1
  expand = 3
  formula = G4_LITHIUM_CARBONATE
  name = G4_LITHIUM_CARBONATE
  specific = 4
FEATURE [App::DocumentObjectGroupPython] Li_element003  label="Li_element : 003"  # scripted group (container) (typed FeaturePython)
  n = 1
  ref = Li_element
FEATURE [App::DocumentObjectGroupPython] F_element012  label="F_element : 004"  # scripted group (container) (typed FeaturePython)
  n = 1
  ref = F_element
FEATURE [App::DocumentObjectGroupPython] G4_LITHIUM_FLUORIDE  # scripted group (container) (typed FeaturePython)
  Dunit = g/cm3
  Dvalue = 2.635
  Group = -> [Li_element003,F_element012]
  conduct = 2
  density = 1
  expand = 3
  formula = G4_LITHIUM_FLUORIDE
  name = G4_LITHIUM_FLUORIDE
  specific = 4
FEATURE [App::DocumentObjectGroupPython] Li_element004  label="Li_element : 004"  # scripted group (container) (typed FeaturePython)
  n = 1
  ref = Li_element
FEATURE [App::DocumentObjectGroupPython] H_element050  label="H_element : 027"  # scripted group (container) (typed FeaturePython)
  n = 1
  ref = H_element
FEATURE [App::DocumentObjectGroupPython] G4_LITHIUM_HYDRIDE  # scripted group (container) (typed FeaturePython)
  Dunit = g/cm3
  Dvalue = 0.82
  Group = -> [Li_element004,H_element050]
  conduct = 2
  density = 1
  expand = 3
  formula = G4_LITHIUM_HYDRIDE
  name = G4_LITHIUM_HYDRIDE
  specific = 4
FEATURE [App::DocumentObjectGroupPython] Li_element005  label="Li_element : 005"  # scripted group (container) (typed FeaturePython)
  n = 1
  ref = Li_element
FEATURE [App::DocumentObjectGroupPython] I_element003  label="I_element : 002"  # scripted group (container) (typed FeaturePython)
  n = 1
  ref = I_element
FEATURE [App::DocumentObjectGroupPython] G4_LITHIUM_IODIDE  # scripted group (container) (typed FeaturePython)
  Dunit = g/cm3
  Dvalue = 3.494
  Group = -> [Li_element005,I_element003]
  conduct = 2
  density = 1
  expand = 3
  formula = G4_LITHIUM_IODIDE
  name = G4_LITHIUM_IODIDE
  specific = 4
FEATURE [App::DocumentObjectGroupPython] Li_element006  label="Li_element : 006"  # scripted group (container) (typed FeaturePython)
  n = 2
  ref = Li_element
FEATURE [App::DocumentObjectGroupPython] O_element055  label="O_element : 029"  # scripted group (container) (typed FeaturePython)
  n = 1
  ref = O_element
FEATURE [App::DocumentObjectGroupPython] G4_LITHIUM_OXIDE  # scripted group (container) (typed FeaturePython)
  Dunit = g/cm3
  Dvalue = 2.013
  Group = -> [Li_element006,O_element055]
  conduct = 2
  density = 1
  expand = 3
  formula = G4_LITHIUM_OXIDE
  name = G4_LITHIUM_OXIDE
  specific = 4
FEATURE [App::DocumentObjectGroupPython] Li_element007  label="Li_element : 007"  # scripted group (container) (typed FeaturePython)
  n = 2
  ref = Li_element
FEATURE [App::DocumentObjectGroupPython] B_element005  label="B_element : 005"  # scripted group (container) (typed FeaturePython)
  n = 4
  ref = B_element
FEATURE [App::DocumentObjectGroupPython] O_element056  label="O_element : 7"  # scripted group (container) (typed FeaturePython)
  n = 7
  ref = O_element
FEATURE [App::DocumentObjectGroupPython] G4_LITHIUM_TETRABORATE  # scripted group (container) (typed FeaturePython)
  Dunit = g/cm3
  Dvalue = 2.44
  Group = -> [Li_element007,B_element005,O_element056]
  conduct = 2
  density = 1
  expand = 3
  formula = G4_LITHIUM_TETRABORATE
  name = G4_LITHIUM_TETRABORATE
  specific = 4
FEATURE [App::DocumentObjectGroupPython] H_element051  label="H_element : 0.105"  # scripted group (container) (typed FeaturePython)
  n = 0.105
FEATURE [App::DocumentObjectGroupPython] C_element056  label="C_element : 0.083"  # scripted group (container) (typed FeaturePython)
  n = 0.083
FEATURE [App::DocumentObjectGroupPython] N_element023  label="N_element : 0.023"  # scripted group (container) (typed FeaturePython)
  n = 0.023
FEATURE [App::DocumentObjectGroupPython] O_element057  label="O_element : 0.779"  # scripted group (container) (typed FeaturePython)
  n = 0.779
FEATURE [App::DocumentObjectGroupPython] Na_element010  label="Na_element : 0.097"  # scripted group (container) (typed FeaturePython)
  n = 0.002
FEATURE [App::DocumentObjectGroupPython] P_element006  label="P_element : 0.105"  # scripted group (container) (typed FeaturePython)
  n = 0.001
FEATURE [App::DocumentObjectGroupPython] S_element016  label="S_element : 0.017"  # scripted group (container) (typed FeaturePython)
  n = 0.002
FEATURE [App::DocumentObjectGroupPython] Cl_element014  label="Cl_element : 0.587"  # scripted group (container) (typed FeaturePython)
  n = 0.003
FEATURE [App::DocumentObjectGroupPython] K_element005  label="K_element : 0.015"  # scripted group (container) (typed FeaturePython)
  n = 0.002
FEATURE [App::DocumentObjectGroupPython] G4_LUNG_ICRP  # scripted group (container) (typed FeaturePython)
  Dunit = g/cm3
  Dvalue = 1.04
  Group = -> [H_element051,C_element056,N_element023,O_element057,Na_element010,P_element006,S_element016,Cl_element014,K_element005]
  conduct = 2
  density = 1
  expand = 3
  formula = G4_LUNG_ICRP
  name = G4_LUNG_ICRP
  specific = 4
FEATURE [App::DocumentObjectGroupPython] H_element052  label="H_element : 0.116"  # scripted group (container) (typed FeaturePython)
  n = 0.114318
FEATURE [App::DocumentObjectGroupPython] C_element057  label="C_element : 0.656"  # scripted group (container) (typed FeaturePython)
  n = 0.655824
FEATURE [App::DocumentObjectGroupPython] O_element058  label="O_element : 0.092"  # scripted group (container) (typed FeaturePython)
  n = 0.0921831
FEATURE [App::DocumentObjectGroupPython] Mg_element004  label="Mg_element : 0.135"  # scripted group (container) (typed FeaturePython)
  n = 0.134792
FEATURE [App::DocumentObjectGroupPython] Ca_element013  label="Ca_element : 0.003"  # scripted group (container) (typed FeaturePython)
  n = 0.002883
FEATURE [App::DocumentObjectGroupPython] G4_M3_WAX  # scripted group (container) (typed FeaturePython)
  Dunit = g/cm3
  Dvalue = 1.05
  Group = -> [H_element052,C_element057,O_element058,Mg_element004,Ca_element013]
  conduct = 2
  density = 1
  expand = 3
  formula = G4_M3_WAX
  name = G4_M3_WAX
  specific = 4
FEATURE [App::DocumentObjectGroupPython] Mg_element005  label="Mg_element : 1"  # scripted group (container) (typed FeaturePython)
  n = 1
  ref = Mg_element
FEATURE [App::DocumentObjectGroupPython] C_element058  label="C_element : 031"  # scripted group (container) (typed FeaturePython)
  n = 1
  ref = C_element
FEATURE [App::DocumentObjectGroupPython] O_element059  label="O_element : 030"  # scripted group (container) (typed FeaturePython)
  n = 3
  ref = O_element
FEATURE [App::DocumentObjectGroupPython] G4_MAGNESIUM_CARBONATE  # scripted group (container) (typed FeaturePython)
  Dunit = g/cm3
  Dvalue = 2.958
  Group = -> [Mg_element005,C_element058,O_element059]
  conduct = 2
  density = 1
  expand = 3
  formula = G4_MAGNESIUM_CARBONATE
  name = G4_MAGNESIUM_CARBONATE
  specific = 4
FEATURE [App::DocumentObjectGroupPython] Mg_element006  label="Mg_element : 002"  # scripted group (container) (typed FeaturePython)
  n = 1
  ref = Mg_element
FEATURE [App::DocumentObjectGroupPython] F_element013  label="F_element : 005"  # scripted group (container) (typed FeaturePython)
  n = 2
  ref = F_element
FEATURE [App::DocumentObjectGroupPython] G4_MAGNESIUM_FLUORIDE  # scripted group (container) (typed FeaturePython)
  Dunit = g/cm3
  Dvalue = 3
  Group = -> [Mg_element006,F_element013]
  conduct = 2
  density = 1
  expand = 3
  formula = G4_MAGNESIUM_FLUORIDE
  name = G4_MAGNESIUM_FLUORIDE
  specific = 4
FEATURE [App::DocumentObjectGroupPython] Mg_element007  label="Mg_element : 003"  # scripted group (container) (typed FeaturePython)
  n = 1
  ref = Mg_element
FEATURE [App::DocumentObjectGroupPython] O_element060  label="O_element : 031"  # scripted group (container) (typed FeaturePython)
  n = 1
  ref = O_element
FEATURE [App::DocumentObjectGroupPython] G4_MAGNESIUM_OXIDE  # scripted group (container) (typed FeaturePython)
  Dunit = g/cm3
  Dvalue = 3.58
  Group = -> [Mg_element007,O_element060]
  conduct = 2
  density = 1
  expand = 3
  formula = G4_MAGNESIUM_OXIDE
  name = G4_MAGNESIUM_OXIDE
  specific = 4
FEATURE [App::DocumentObjectGroupPython] Mg_element008  label="Mg_element : 004"  # scripted group (container) (typed FeaturePython)
  n = 1
  ref = Mg_element
FEATURE [App::DocumentObjectGroupPython] B_element006  label="B_element : 006"  # scripted group (container) (typed FeaturePython)
  n = 4
  ref = B_element
FEATURE [App::DocumentObjectGroupPython] O_element061  label="O_element : 032"  # scripted group (container) (typed FeaturePython)
  n = 7
  ref = O_element
FEATURE [App::DocumentObjectGroupPython] G4_MAGNESIUM_TETRABORATE  # scripted group (container) (typed FeaturePython)
  Dunit = g/cm3
  Dvalue = 2.53
  Group = -> [Mg_element008,B_element006,O_element061]
  conduct = 2
  density = 1
  expand = 3
  formula = G4_MAGNESIUM_TETRABORATE
  name = G4_MAGNESIUM_TETRABORATE
  specific = 4
FEATURE [App::DocumentObjectGroupPython] Hg_element001  label="Hg_element : 1"  # scripted group (container) (typed FeaturePython)
  n = 1
  ref = Hg_element
FEATURE [App::DocumentObjectGroupPython] I_element004  label="I_element : 2"  # scripted group (container) (typed FeaturePython)
  n = 2
  ref = I_element
FEATURE [App::DocumentObjectGroupPython] G4_MERCURIC_IODIDE  # scripted group (container) (typed FeaturePython)
  Dunit = g/cm3
  Dvalue = 6.36
  Group = -> [Hg_element001,I_element004]
  conduct = 2
  density = 1
  expand = 3
  formula = G4_MERCURIC_IODIDE
  name = G4_MERCURIC_IODIDE
  specific = 4
FEATURE [App::DocumentObjectGroupPython] C_element059  label="C_element : 032"  # scripted group (container) (typed FeaturePython)
  n = 1
  ref = C_element
FEATURE [App::DocumentObjectGroupPython] H_element053  label="H_element : 028"  # scripted group (container) (typed FeaturePython)
  n = 4
  ref = H_element
FEATURE [App::DocumentObjectGroupPython] G4_METHANE  # scripted group (container) (typed FeaturePython)
  Dunit = g/cm3
  Dvalue = 0.000667151
  Group = -> [C_element059,H_element053]
  conduct = 2
  density = 1
  expand = 3
  formula = G4_METHANE
  name = G4_METHANE
  specific = 4
FEATURE [App::DocumentObjectGroupPython] C_element060  label="C_element : 033"  # scripted group (container) (typed FeaturePython)
  n = 1
  ref = C_element
FEATURE [App::DocumentObjectGroupPython] H_element054  label="H_element : 029"  # scripted group (container) (typed FeaturePython)
  n = 4
  ref = H_element
FEATURE [App::DocumentObjectGroupPython] O_element062  label="O_element : 033"  # scripted group (container) (typed FeaturePython)
  n = 1
  ref = O_element
FEATURE [App::DocumentObjectGroupPython] G4_METHANOL  # scripted group (container) (typed FeaturePython)
  Dunit = g/cm3
  Dvalue = 0.7914
  Group = -> [C_element060,H_element054,O_element062]
  conduct = 2
  density = 1
  expand = 3
  formula = G4_METHANOL
  name = G4_METHANOL
  specific = 4
FEATURE [App::DocumentObjectGroupPython] H_element055  label="H_element : 0.134"  # scripted group (container) (typed FeaturePython)
  n = 0.13404
FEATURE [App::DocumentObjectGroupPython] C_element061  label="C_element : 0.778"  # scripted group (container) (typed FeaturePython)
  n = 0.77796
FEATURE [App::DocumentObjectGroupPython] O_element063  label="O_element : 0.035"  # scripted group (container) (typed FeaturePython)
  n = 0.03502
FEATURE [App::DocumentObjectGroupPython] Mg_element009  label="Mg_element : 0.039"  # scripted group (container) (typed FeaturePython)
  n = 0.038594
FEATURE [App::DocumentObjectGroupPython] Ti_element002  label="Ti_element : 0.014"  # scripted group (container) (typed FeaturePython)
  n = 0.014386
FEATURE [App::DocumentObjectGroupPython] G4_MIX_D_WAX  # scripted group (container) (typed FeaturePython)
  Dunit = g/cm3
  Dvalue = 0.99
  Group = -> [H_element055,C_element061,O_element063,Mg_element009,Ti_element002]
  conduct = 2
  density = 1
  expand = 3
  formula = G4_MIX_D_WAX
  name = G4_MIX_D_WAX
  specific = 4
FEATURE [App::DocumentObjectGroupPython] H_element056  label="H_element : 0.135"  # scripted group (container) (typed FeaturePython)
  n = 0.081192
FEATURE [App::DocumentObjectGroupPython] C_element062  label="C_element : 0.583"  # scripted group (container) (typed FeaturePython)
  n = 0.583442
FEATURE [App::DocumentObjectGroupPython] N_element024  label="N_element : 0.018"  # scripted group (container) (typed FeaturePython)
  n = 0.017798
FEATURE [App::DocumentObjectGroupPython] O_element064  label="O_element : 0.186"  # scripted group (container) (typed FeaturePython)
  n = 0.186381
FEATURE [App::DocumentObjectGroupPython] Mg_element010  label="Mg_element : 0.130"  # scripted group (container) (typed FeaturePython)
  n = 0.130287
FEATURE [App::DocumentObjectGroupPython] Cl_element015  label="Cl_element : 0.588"  # scripted group (container) (typed FeaturePython)
  n = 0.0009
FEATURE [App::DocumentObjectGroupPython] G4_MS20_TISSUE  # scripted group (container) (typed FeaturePython)
  Dunit = g/cm3
  Dvalue = 1
  Group = -> [H_element056,C_element062,N_element024,O_element064,Mg_element010,Cl_element015]
  conduct = 2
  density = 1
  expand = 3
  formula = G4_MS20_TISSUE
  name = G4_MS20_TISSUE
  specific = 4
FEATURE [App::DocumentObjectGroupPython] H_element057  label="H_element : 0.136"  # scripted group (container) (typed FeaturePython)
  n = 0.102
FEATURE [App::DocumentObjectGroupPython] C_element063  label="C_element : 0.143"  # scripted group (container) (typed FeaturePython)
  n = 0.143
FEATURE [App::DocumentObjectGroupPython] N_element025  label="N_element : 0.034"  # scripted group (container) (typed FeaturePython)
  n = 0.034
FEATURE [App::DocumentObjectGroupPython] O_element065  label="O_element : 0.710"  # scripted group (container) (typed FeaturePython)
  n = 0.71
FEATURE [App::DocumentObjectGroupPython] Na_element011  label="Na_element : 0.098"  # scripted group (container) (typed FeaturePython)
  n = 0.001
FEATURE [App::DocumentObjectGroupPython] P_element007  label="P_element : 0.002"  # scripted group (container) (typed FeaturePython)
  n = 0.002
FEATURE [App::DocumentObjectGroupPython] S_element017  label="S_element : 0.018"  # scripted group (container) (typed FeaturePython)
  n = 0.003
FEATURE [App::DocumentObjectGroupPython] Cl_element016  label="Cl_element : 0.589"  # scripted group (container) (typed FeaturePython)
  n = 0.001
FEATURE [App::DocumentObjectGroupPython] K_element006  label="K_element : 0.004"  # scripted group (container) (typed FeaturePython)
  n = 0.004
FEATURE [App::DocumentObjectGroupPython] G4_MUSCLE_SKELETAL_ICRP  # scripted group (container) (typed FeaturePython)
  Dunit = g/cm3
  Dvalue = 1.05
  Group = -> [H_element057,C_element063,N_element025,O_element065,Na_element011,P_element007,S_element017,Cl_element016,K_element006]
  conduct = 2
  density = 1
  expand = 3
  formula = G4_MUSCLE_SKELETAL_ICRP
  name = G4_MUSCLE_SKELETAL_ICRP
  specific = 4
FEATURE [App::DocumentObjectGroupPython] H_element058  label="H_element : 0.137"  # scripted group (container) (typed FeaturePython)
  n = 0.102102
FEATURE [App::DocumentObjectGroupPython] C_element064  label="C_element : 0.123"  # scripted group (container) (typed FeaturePython)
  n = 0.123123
FEATURE [App::DocumentObjectGroupPython] N_element026  label="N_element : 0.756"  # scripted group (container) (typed FeaturePython)
  n = 0.035035
FEATURE [App::DocumentObjectGroupPython] O_element066  label="O_element : 0.730"  # scripted group (container) (typed FeaturePython)
  n = 0.72973
FEATURE [App::DocumentObjectGroupPython] Na_element012  label="Na_element : 0.099"  # scripted group (container) (typed FeaturePython)
  n = 0.001001
FEATURE [App::DocumentObjectGroupPython] P_element008  label="P_element : 0.106"  # scripted group (container) (typed FeaturePython)
  n = 0.002002
FEATURE [App::DocumentObjectGroupPython] S_element018  label="S_element : 0.019"  # scripted group (container) (typed FeaturePython)
  n = 0.004004
FEATURE [App::DocumentObjectGroupPython] K_element007  label="K_element : 0.016"  # scripted group (container) (typed FeaturePython)
  n = 0.003003
FEATURE [App::DocumentObjectGroupPython] G4_MUSCLE_STRIATED_ICRU  # scripted group (container) (typed FeaturePython)
  Dunit = g/cm3
  Dvalue = 1.04
  Group = -> [H_element058,C_element064,N_element026,O_element066,Na_element012,P_element008,S_element018,K_element007]
  conduct = 2
  density = 1
  expand = 3
  formula = G4_MUSCLE_STRIATED_ICRU
  name = G4_MUSCLE_STRIATED_ICRU
  specific = 4
FEATURE [App::DocumentObjectGroupPython] H_element059  label="H_element : 0.098"  # scripted group (container) (typed FeaturePython)
  n = 0.0982341
FEATURE [App::DocumentObjectGroupPython] C_element065  label="C_element : 0.156"  # scripted group (container) (typed FeaturePython)
  n = 0.156214
FEATURE [App::DocumentObjectGroupPython] N_element027  label="N_element : 0.757"  # scripted group (container) (typed FeaturePython)
  n = 0.035451
FEATURE [App::DocumentObjectGroupPython] O_element067  label="O_element : 0.880"  # scripted group (container) (typed FeaturePython)
  n = 0.710101
FEATURE [App::DocumentObjectGroupPython] G4_MUSCLE_WITH_SUCROSE  # scripted group (container) (typed FeaturePython)
  Dunit = g/cm3
  Dvalue = 1.11
  Group = -> [H_element059,C_element065,N_element027,O_element067]
  conduct = 2
  density = 1
  expand = 3
  formula = G4_MUSCLE_WITH_SUCROSE
  name = G4_MUSCLE_WITH_SUCROSE
  specific = 4
FEATURE [App::DocumentObjectGroupPython] H_element060  label="H_element : 0.138"  # scripted group (container) (typed FeaturePython)
  n = 0.101969
FEATURE [App::DocumentObjectGroupPython] C_element066  label="C_element : 0.120"  # scripted group (container) (typed FeaturePython)
  n = 0.120058
FEATURE [App::DocumentObjectGroupPython] N_element028  label="N_element : 0.758"  # scripted group (container) (typed FeaturePython)
  n = 0.035451
FEATURE [App::DocumentObjectGroupPython] O_element068  label="O_element : 0.743"  # scripted group (container) (typed FeaturePython)
  n = 0.742522
FEATURE [App::DocumentObjectGroupPython] G4_MUSCLE_WITHOUT_SUCROSE  # scripted group (container) (typed FeaturePython)
  Dunit = g/cm3
  Dvalue = 1.07
  Group = -> [H_element060,C_element066,N_element028,O_element068]
  conduct = 2
  density = 1
  expand = 3
  formula = G4_MUSCLE_WITHOUT_SUCROSE
  name = G4_MUSCLE_WITHOUT_SUCROSE
  specific = 4
FEATURE [App::DocumentObjectGroupPython] C_element067  label="C_element : 10"  # scripted group (container) (typed FeaturePython)
  n = 10
  ref = C_element
FEATURE [App::DocumentObjectGroupPython] H_element061  label="H_element : 030"  # scripted group (container) (typed FeaturePython)
  n = 8
  ref = H_element
FEATURE [App::DocumentObjectGroupPython] G4_NAPHTHALENE  # scripted group (container) (typed FeaturePython)
  Dunit = g/cm3
  Dvalue = 1.145
  Group = -> [C_element067,H_element061]
  conduct = 2
  density = 1
  expand = 3
  formula = G4_NAPHTHALENE
  name = G4_NAPHTHALENE
  specific = 4
FEATURE [App::DocumentObjectGroupPython] C_element068  label="C_element : 034"  # scripted group (container) (typed FeaturePython)
  n = 6
  ref = C_element
FEATURE [App::DocumentObjectGroupPython] H_element062  label="H_element : 031"  # scripted group (container) (typed FeaturePython)
  n = 5
  ref = H_element
FEATURE [App::DocumentObjectGroupPython] N_element029  label="N_element : 012"  # scripted group (container) (typed FeaturePython)
  n = 1
  ref = N_element
FEATURE [App::DocumentObjectGroupPython] O_element069  label="O_element : 034"  # scripted group (container) (typed FeaturePython)
  n = 2
  ref = O_element
FEATURE [App::DocumentObjectGroupPython] G4_NITROBENZENE  # scripted group (container) (typed FeaturePython)
  Dunit = g/cm3
  Dvalue = 1.19867
  Group = -> [C_element068,H_element062,N_element029,O_element069]
  conduct = 2
  density = 1
  expand = 3
  formula = G4_NITROBENZENE
  name = G4_NITROBENZENE
  specific = 4
FEATURE [App::DocumentObjectGroupPython] N_element030  label="N_element : 013"  # scripted group (container) (typed FeaturePython)
  n = 2
  ref = N_element
FEATURE [App::DocumentObjectGroupPython] O_element070  label="O_element : 035"  # scripted group (container) (typed FeaturePython)
  n = 1
  ref = O_element
FEATURE [App::DocumentObjectGroupPython] G4_NITROUS_OXIDE  # scripted group (container) (typed FeaturePython)
  Dunit = g/cm3
  Dvalue = 0.00183094
  Group = -> [N_element030,O_element070]
  conduct = 2
  density = 1
  expand = 3
  formula = G4_NITROUS_OXIDE
  name = G4_NITROUS_OXIDE
  specific = 4
FEATURE [App::DocumentObjectGroupPython] H_element063  label="H_element : 0.104"  # scripted group (container) (typed FeaturePython)
  n = 0.103509
FEATURE [App::DocumentObjectGroupPython] C_element069  label="C_element : 0.648"  # scripted group (container) (typed FeaturePython)
  n = 0.648416
FEATURE [App::DocumentObjectGroupPython] N_element031  label="N_element : 0.100"  # scripted group (container) (typed FeaturePython)
  n = 0.0995361
FEATURE [App::DocumentObjectGroupPython] O_element071  label="O_element : 0.149"  # scripted group (container) (typed FeaturePython)
  n = 0.148539
FEATURE [App::DocumentObjectGroupPython] G4_NYLON_8062  label="G4_NYLON-8062"  # scripted group (container) (typed FeaturePython)
  Dunit = g/cm3
  Dvalue = 1.08
  Group = -> [H_element063,C_element069,N_element031,O_element071]
  conduct = 2
  density = 1
  expand = 3
  formula = G4_NYLON-8062
  name = G4_NYLON-8062
  specific = 4
FEATURE [App::DocumentObjectGroupPython] C_element070  label="C_element : 035"  # scripted group (container) (typed FeaturePython)
  n = 6
  ref = C_element
FEATURE [App::DocumentObjectGroupPython] H_element064  label="H_element : 11"  # scripted group (container) (typed FeaturePython)
  n = 11
  ref = H_element
FEATURE [App::DocumentObjectGroupPython] N_element032  label="N_element : 014"  # scripted group (container) (typed FeaturePython)
  n = 1
  ref = N_element
FEATURE [App::DocumentObjectGroupPython] O_element072  label="O_element : 036"  # scripted group (container) (typed FeaturePython)
  n = 1
  ref = O_element
FEATURE [App::DocumentObjectGroupPython] G4_NYLON_6_6  label="G4_NYLON-6-6"  # scripted group (container) (typed FeaturePython)
  Dunit = g/cm3
  Dvalue = 1.14
  Group = -> [C_element070,H_element064,N_element032,O_element072]
  conduct = 2
  density = 1
  expand = 3
  formula = G4_NYLON-6-6
  name = G4_NYLON-6-6
  specific = 4
FEATURE [App::DocumentObjectGroupPython] H_element065  label="H_element : 0.139"  # scripted group (container) (typed FeaturePython)
  n = 0.107062
FEATURE [App::DocumentObjectGroupPython] C_element071  label="C_element : 0.680"  # scripted group (container) (typed FeaturePython)
  n = 0.680449
FEATURE [App::DocumentObjectGroupPython] N_element033  label="N_element : 0.099"  # scripted group (container) (typed FeaturePython)
  n = 0.099189
FEATURE [App::DocumentObjectGroupPython] O_element073  label="O_element : 0.113"  # scripted group (container) (typed FeaturePython)
  n = 0.1133
FEATURE [App::DocumentObjectGroupPython] G4_NYLON_6_10  label="G4_NYLON-6-10"  # scripted group (container) (typed FeaturePython)
  Dunit = g/cm3
  Dvalue = 1.14
  Group = -> [H_element065,C_element071,N_element033,O_element073]
  conduct = 2
  density = 1
  expand = 3
  formula = G4_NYLON-6-10
  name = G4_NYLON-6-10
  specific = 4
FEATURE [App::DocumentObjectGroupPython] H_element066  label="H_element : 0.140"  # scripted group (container) (typed FeaturePython)
  n = 0.115476
FEATURE [App::DocumentObjectGroupPython] C_element072  label="C_element : 0.721"  # scripted group (container) (typed FeaturePython)
  n = 0.720818
FEATURE [App::DocumentObjectGroupPython] N_element034  label="N_element : 0.076"  # scripted group (container) (typed FeaturePython)
  n = 0.0764169
FEATURE [App::DocumentObjectGroupPython] O_element074  label="O_element : 0.087"  # scripted group (container) (typed FeaturePython)
  n = 0.0872889
FEATURE [App::DocumentObjectGroupPython] G4_NYLON_11_RILSAN  label="G4_NYLON-11_RILSAN"  # scripted group (container) (typed FeaturePython)
  Dunit = g/cm3
  Dvalue = 1.425
  Group = -> [H_element066,C_element072,N_element034,O_element074]
  conduct = 2
  density = 1
  expand = 3
  formula = G4_NYLON-11_RILSAN
  name = G4_NYLON-11_RILSAN
  specific = 4
FEATURE [App::DocumentObjectGroupPython] C_element073  label="C_element : 8"  # scripted group (container) (typed FeaturePython)
  n = 8
  ref = C_element
FEATURE [App::DocumentObjectGroupPython] H_element067  label="H_element : 18"  # scripted group (container) (typed FeaturePython)
  n = 18
  ref = H_element
FEATURE [App::DocumentObjectGroupPython] G4_OCTANE  # scripted group (container) (typed FeaturePython)
  Dunit = g/cm3
  Dvalue = 0.7026
  Group = -> [C_element073,H_element067]
  conduct = 2
  density = 1
  expand = 3
  formula = G4_OCTANE
  name = G4_OCTANE
  specific = 4
FEATURE [App::DocumentObjectGroupPython] C_element074  label="C_element : 25"  # scripted group (container) (typed FeaturePython)
  n = 25
  ref = C_element
FEATURE [App::DocumentObjectGroupPython] H_element068  label="H_element : 52"  # scripted group (container) (typed FeaturePython)
  n = 52
  ref = H_element
FEATURE [App::DocumentObjectGroupPython] G4_PARAFFIN  # scripted group (container) (typed FeaturePython)
  Dunit = g/cm3
  Dvalue = 0.93
  Group = -> [C_element074,H_element068]
  conduct = 2
  density = 1
  expand = 3
  formula = G4_PARAFFIN
  name = G4_PARAFFIN
  specific = 4
FEATURE [App::DocumentObjectGroupPython] C_element075  label="C_element : 036"  # scripted group (container) (typed FeaturePython)
  n = 5
  ref = C_element
FEATURE [App::DocumentObjectGroupPython] H_element069  label="H_element : 032"  # scripted group (container) (typed FeaturePython)
  n = 12
  ref = H_element
FEATURE [App::DocumentObjectGroupPython] G4_N_PENTANE  label="G4_N-PENTANE"  # scripted group (container) (typed FeaturePython)
  Dunit = g/cm3
  Dvalue = 0.6262
  Group = -> [C_element075,H_element069]
  conduct = 2
  density = 1
  expand = 3
  formula = G4_N-PENTANE
  name = G4_N-PENTANE
  specific = 4
FEATURE [App::DocumentObjectGroupPython] H_element070  label="H_element : 0.014"  # scripted group (container) (typed FeaturePython)
  n = 0.0141
FEATURE [App::DocumentObjectGroupPython] C_element076  label="C_element : 0.072"  # scripted group (container) (typed FeaturePython)
  n = 0.072261
FEATURE [App::DocumentObjectGroupPython] N_element035  label="N_element : 0.019"  # scripted group (container) (typed FeaturePython)
  n = 0.01932
FEATURE [App::DocumentObjectGroupPython] O_element075  label="O_element : 0.066"  # scripted group (container) (typed FeaturePython)
  n = 0.066101
FEATURE [App::DocumentObjectGroupPython] S_element019  label="S_element : 0.020"  # scripted group (container) (typed FeaturePython)
  n = 0.00189
FEATURE [App::DocumentObjectGroupPython] Br_element004  label="Br_element : 0.349"  # scripted group (container) (typed FeaturePython)
  n = 0.349103
FEATURE [App::DocumentObjectGroupPython] Ag_element001  label="Ag_element : 0.474"  # scripted group (container) (typed FeaturePython)
  n = 0.474105
FEATURE [App::DocumentObjectGroupPython] I_element005  label="I_element : 0.003"  # scripted group (container) (typed FeaturePython)
  n = 0.00312
FEATURE [App::DocumentObjectGroupPython] G4_PHOTO_EMULSION  # scripted group (container) (typed FeaturePython)
  Dunit = g/cm3
  Dvalue = 3.815
  Group = -> [H_element070,C_element076,N_element035,O_element075,S_element019,Br_element004,Ag_element001,I_element005]
  conduct = 2
  density = 1
  expand = 3
  formula = G4_PHOTO_EMULSION
  name = G4_PHOTO_EMULSION
  specific = 4
FEATURE [App::DocumentObjectGroupPython] C_element077  label="C_element : 9"  # scripted group (container) (typed FeaturePython)
  n = 9
  ref = C_element
FEATURE [App::DocumentObjectGroupPython] H_element071  label="H_element : 033"  # scripted group (container) (typed FeaturePython)
  n = 10
  ref = H_element
FEATURE [App::DocumentObjectGroupPython] G4_PLASTIC_SC_VINYLTOLUENE  # scripted group (container) (typed FeaturePython)
  Dunit = g/cm3
  Dvalue = 1.032
  Group = -> [C_element077,H_element071]
  conduct = 2
  density = 1
  expand = 3
  formula = G4_PLASTIC_SC_VINYLTOLUENE
  name = G4_PLASTIC_SC_VINYLTOLUENE
  specific = 4
FEATURE [App::DocumentObjectGroupPython] Pu_element001  label="Pu_element : 1"  # scripted group (container) (typed FeaturePython)
  n = 1
  ref = Pu_element
FEATURE [App::DocumentObjectGroupPython] O_element076  label="O_element : 037"  # scripted group (container) (typed FeaturePython)
  n = 2
  ref = O_element
FEATURE [App::DocumentObjectGroupPython] G4_PLUTONIUM_DIOXIDE  # scripted group (container) (typed FeaturePython)
  Dunit = g/cm3
  Dvalue = 11.46
  Group = -> [Pu_element001,O_element076]
  conduct = 2
  density = 1
  expand = 3
  formula = G4_PLUTONIUM_DIOXIDE
  name = G4_PLUTONIUM_DIOXIDE
  specific = 4
FEATURE [App::DocumentObjectGroupPython] C_element078  label="C_element : 037"  # scripted group (container) (typed FeaturePython)
  n = 3
  ref = C_element
FEATURE [App::DocumentObjectGroupPython] H_element072  label="H_element : 034"  # scripted group (container) (typed FeaturePython)
  n = 3
  ref = H_element
FEATURE [App::DocumentObjectGroupPython] N_element036  label="N_element : 015"  # scripted group (container) (typed FeaturePython)
  n = 1
  ref = N_element
FEATURE [App::DocumentObjectGroupPython] G4_POLYACRYLONITRILE  # scripted group (container) (typed FeaturePython)
  Dunit = g/cm3
  Dvalue = 1.17
  Group = -> [C_element078,H_element072,N_element036]
  conduct = 2
  density = 1
  expand = 3
  formula = G4_POLYACRYLONITRILE
  name = G4_POLYACRYLONITRILE
  specific = 4
FEATURE [App::DocumentObjectGroupPython] C_element079  label="C_element : 16"  # scripted group (container) (typed FeaturePython)
  n = 16
  ref = C_element
FEATURE [App::DocumentObjectGroupPython] H_element073  label="H_element : 035"  # scripted group (container) (typed FeaturePython)
  n = 14
  ref = H_element
FEATURE [App::DocumentObjectGroupPython] O_element077  label="O_element : 038"  # scripted group (container) (typed FeaturePython)
  n = 3
  ref = O_element
FEATURE [App::DocumentObjectGroupPython] G4_POLYCARBONATE  # scripted group (container) (typed FeaturePython)
  Dunit = g/cm3
  Dvalue = 1.2
  Group = -> [C_element079,H_element073,O_element077]
  conduct = 2
  density = 1
  expand = 3
  formula = G4_POLYCARBONATE
  name = G4_POLYCARBONATE
  specific = 4
FEATURE [App::DocumentObjectGroupPython] C_element080  label="C_element : 038"  # scripted group (container) (typed FeaturePython)
  n = 8
  ref = C_element
FEATURE [App::DocumentObjectGroupPython] H_element074  label="H_element : 036"  # scripted group (container) (typed FeaturePython)
  n = 7
  ref = H_element
FEATURE [App::DocumentObjectGroupPython] Cl_element017  label="Cl_element : 007"  # scripted group (container) (typed FeaturePython)
  n = 1
  ref = Cl_element
FEATURE [App::DocumentObjectGroupPython] G4_POLYCHLOROSTYRENE  # scripted group (container) (typed FeaturePython)
  Dunit = g/cm3
  Dvalue = 1.3
  Group = -> [C_element080,H_element074,Cl_element017]
  conduct = 2
  density = 1
  expand = 3
  formula = G4_POLYCHLOROSTYRENE
  name = G4_POLYCHLOROSTYRENE
  specific = 4
FEATURE [App::DocumentObjectGroupPython] C_element081  label="C_element : 039"  # scripted group (container) (typed FeaturePython)
  n = 1
  ref = C_element
FEATURE [App::DocumentObjectGroupPython] H_element075  label="H_element : 037"  # scripted group (container) (typed FeaturePython)
  n = 2
  ref = H_element
FEATURE [App::DocumentObjectGroupPython] G4_POLYETHYLENE  # scripted group (container) (typed FeaturePython)
  Dunit = g/cm3
  Dvalue = 0.94
  Group = -> [C_element081,H_element075]
  conduct = 2
  density = 1
  expand = 3
  formula = G4_POLYETHYLENE
  name = G4_POLYETHYLENE
  specific = 4
FEATURE [App::DocumentObjectGroupPython] C_element082  label="C_element : 040"  # scripted group (container) (typed FeaturePython)
  n = 10
  ref = C_element
FEATURE [App::DocumentObjectGroupPython] H_element076  label="H_element : 038"  # scripted group (container) (typed FeaturePython)
  n = 8
  ref = H_element
FEATURE [App::DocumentObjectGroupPython] O_element078  label="O_element : 039"  # scripted group (container) (typed FeaturePython)
  n = 4
  ref = O_element
FEATURE [App::DocumentObjectGroupPython] G4_MYLAR  # scripted group (container) (typed FeaturePython)
  Dunit = g/cm3
  Dvalue = 1.4
  Group = -> [C_element082,H_element076,O_element078]
  conduct = 2
  density = 1
  expand = 3
  formula = G4_MYLAR
  name = G4_MYLAR
  specific = 4
FEATURE [App::DocumentObjectGroupPython] C_element083  label="C_element : 041"  # scripted group (container) (typed FeaturePython)
  n = 5
  ref = C_element
FEATURE [App::DocumentObjectGroupPython] H_element077  label="H_element : 039"  # scripted group (container) (typed FeaturePython)
  n = 8
  ref = H_element
FEATURE [App::DocumentObjectGroupPython] O_element079  label="O_element : 040"  # scripted group (container) (typed FeaturePython)
  n = 2
  ref = O_element
FEATURE [App::DocumentObjectGroupPython] G4_PLEXIGLASS  # scripted group (container) (typed FeaturePython)
  Dunit = g/cm3
  Dvalue = 1.19
  Group = -> [C_element083,H_element077,O_element079]
  conduct = 2
  density = 1
  expand = 3
  formula = G4_PLEXIGLASS
  name = G4_PLEXIGLASS
  specific = 4
FEATURE [App::DocumentObjectGroupPython] C_element084  label="C_element : 042"  # scripted group (container) (typed FeaturePython)
  n = 1
  ref = C_element
FEATURE [App::DocumentObjectGroupPython] H_element078  label="H_element : 040"  # scripted group (container) (typed FeaturePython)
  n = 2
  ref = H_element
FEATURE [App::DocumentObjectGroupPython] O_element080  label="O_element : 041"  # scripted group (container) (typed FeaturePython)
  n = 1
  ref = O_element
FEATURE [App::DocumentObjectGroupPython] G4_POLYOXYMETHYLENE  # scripted group (container) (typed FeaturePython)
  Dunit = g/cm3
  Dvalue = 1.425
  Group = -> [C_element084,H_element078,O_element080]
  conduct = 2
  density = 1
  expand = 3
  formula = G4_POLYOXYMETHYLENE
  name = G4_POLYOXYMETHYLENE
  specific = 4
FEATURE [App::DocumentObjectGroupPython] C_element085  label="C_element : 043"  # scripted group (container) (typed FeaturePython)
  n = 2
  ref = C_element
FEATURE [App::DocumentObjectGroupPython] H_element079  label="H_element : 041"  # scripted group (container) (typed FeaturePython)
  n = 4
  ref = H_element
FEATURE [App::DocumentObjectGroupPython] G4_POLYPROPYLENE  # scripted group (container) (typed FeaturePython)
  Dunit = g/cm3
  Dvalue = 0.9
  Group = -> [C_element085,H_element079]
  conduct = 2
  density = 1
  expand = 3
  formula = G4_POLYPROPYLENE
  name = G4_POLYPROPYLENE
  specific = 4
FEATURE [App::DocumentObjectGroupPython] C_element086  label="C_element : 044"  # scripted group (container) (typed FeaturePython)
  n = 8
  ref = C_element
FEATURE [App::DocumentObjectGroupPython] H_element080  label="H_element : 042"  # scripted group (container) (typed FeaturePython)
  n = 8
  ref = H_element
FEATURE [App::DocumentObjectGroupPython] G4_POLYSTYRENE  # scripted group (container) (typed FeaturePython)
  Dunit = g/cm3
  Dvalue = 1.06
  Group = -> [C_element086,H_element080]
  conduct = 2
  density = 1
  expand = 3
  formula = G4_POLYSTYRENE
  name = G4_POLYSTYRENE
  specific = 4
FEATURE [App::DocumentObjectGroupPython] C_element087  label="C_element : 045"  # scripted group (container) (typed FeaturePython)
  n = 2
  ref = C_element
FEATURE [App::DocumentObjectGroupPython] F_element014  label="F_element : 4"  # scripted group (container) (typed FeaturePython)
  n = 4
  ref = F_element
FEATURE [App::DocumentObjectGroupPython] G4_TEFLON  # scripted group (container) (typed FeaturePython)
  Dunit = g/cm3
  Dvalue = 2.2
  Group = -> [C_element087,F_element014]
  conduct = 2
  density = 1
  expand = 3
  formula = G4_TEFLON
  name = G4_TEFLON
  specific = 4
FEATURE [App::DocumentObjectGroupPython] C_element088  label="C_element : 046"  # scripted group (container) (typed FeaturePython)
  n = 2
  ref = C_element
FEATURE [App::DocumentObjectGroupPython] F_element015  label="F_element : 006"  # scripted group (container) (typed FeaturePython)
  n = 3
  ref = F_element
FEATURE [App::DocumentObjectGroupPython] Cl_element018  label="Cl_element : 008"  # scripted group (container) (typed FeaturePython)
  n = 1
  ref = Cl_element
FEATURE [App::DocumentObjectGroupPython] G4_POLYTRIFLUOROCHLOROETHYLENE  # scripted group (container) (typed FeaturePython)
  Dunit = g/cm3
  Dvalue = 2.1
  Group = -> [C_element088,F_element015,Cl_element018]
  conduct = 2
  density = 1
  expand = 3
  formula = G4_POLYTRIFLUOROCHLOROETHYLENE
  name = G4_POLYTRIFLUOROCHLOROETHYLENE
  specific = 4
FEATURE [App::DocumentObjectGroupPython] C_element089  label="C_element : 047"  # scripted group (container) (typed FeaturePython)
  n = 4
  ref = C_element
FEATURE [App::DocumentObjectGroupPython] H_element081  label="H_element : 043"  # scripted group (container) (typed FeaturePython)
  n = 6
  ref = H_element
FEATURE [App::DocumentObjectGroupPython] O_element081  label="O_element : 042"  # scripted group (container) (typed FeaturePython)
  n = 2
  ref = O_element
FEATURE [App::DocumentObjectGroupPython] G4_POLYVINYL_ACETATE  # scripted group (container) (typed FeaturePython)
  Dunit = g/cm3
  Dvalue = 1.19
  Group = -> [C_element089,H_element081,O_element081]
  conduct = 2
  density = 1
  expand = 3
  formula = G4_POLYVINYL_ACETATE
  name = G4_POLYVINYL_ACETATE
  specific = 4
FEATURE [App::DocumentObjectGroupPython] C_element090  label="C_element : 048"  # scripted group (container) (typed FeaturePython)
  n = 2
  ref = C_element
FEATURE [App::DocumentObjectGroupPython] H_element082  label="H_element : 044"  # scripted group (container) (typed FeaturePython)
  n = 4
  ref = H_element
FEATURE [App::DocumentObjectGroupPython] O_element082  label="O_element : 043"  # scripted group (container) (typed FeaturePython)
  n = 1
  ref = O_element
FEATURE [App::DocumentObjectGroupPython] G4_POLYVINYL_ALCOHOL  # scripted group (container) (typed FeaturePython)
  Dunit = g/cm3
  Dvalue = 1.3
  Group = -> [C_element090,H_element082,O_element082]
  conduct = 2
  density = 1
  expand = 3
  formula = G4_POLYVINYL_ALCOHOL
  name = G4_POLYVINYL_ALCOHOL
  specific = 4
FEATURE [App::DocumentObjectGroupPython] C_element091  label="C_element : 049"  # scripted group (container) (typed FeaturePython)
  n = 8
  ref = C_element
FEATURE [App::DocumentObjectGroupPython] H_element083  label="H_element : 045"  # scripted group (container) (typed FeaturePython)
  n = 14
  ref = H_element
FEATURE [App::DocumentObjectGroupPython] O_element083  label="O_element : 044"  # scripted group (container) (typed FeaturePython)
  n = 2
  ref = O_element
FEATURE [App::DocumentObjectGroupPython] G4_POLYVINYL_BUTYRAL  # scripted group (container) (typed FeaturePython)
  Dunit = g/cm3
  Dvalue = 1.12
  Group = -> [C_element091,H_element083,O_element083]
  conduct = 2
  density = 1
  expand = 3
  formula = G4_POLYVINYL_BUTYRAL
  name = G4_POLYVINYL_BUTYRAL
  specific = 4
FEATURE [App::DocumentObjectGroupPython] C_element092  label="C_element : 050"  # scripted group (container) (typed FeaturePython)
  n = 2
  ref = C_element
FEATURE [App::DocumentObjectGroupPython] H_element084  label="H_element : 046"  # scripted group (container) (typed FeaturePython)
  n = 3
  ref = H_element
FEATURE [App::DocumentObjectGroupPython] Cl_element019  label="Cl_element : 009"  # scripted group (container) (typed FeaturePython)
  n = 1
  ref = Cl_element
FEATURE [App::DocumentObjectGroupPython] G4_POLYVINYL_CHLORIDE  # scripted group (container) (typed FeaturePython)
  Dunit = g/cm3
  Dvalue = 1.3
  Group = -> [C_element092,H_element084,Cl_element019]
  conduct = 2
  density = 1
  expand = 3
  formula = G4_POLYVINYL_CHLORIDE
  name = G4_POLYVINYL_CHLORIDE
  specific = 4
FEATURE [App::DocumentObjectGroupPython] C_element093  label="C_element : 051"  # scripted group (container) (typed FeaturePython)
  n = 2
  ref = C_element
FEATURE [App::DocumentObjectGroupPython] H_element085  label="H_element : 047"  # scripted group (container) (typed FeaturePython)
  n = 2
  ref = H_element
FEATURE [App::DocumentObjectGroupPython] Cl_element020  label="Cl_element : 010"  # scripted group (container) (typed FeaturePython)
  n = 2
  ref = Cl_element
FEATURE [App::DocumentObjectGroupPython] G4_POLYVINYLIDENE_CHLORIDE  # scripted group (container) (typed FeaturePython)
  Dunit = g/cm3
  Dvalue = 1.7
  Group = -> [C_element093,H_element085,Cl_element020]
  conduct = 2
  density = 1
  expand = 3
  formula = G4_POLYVINYLIDENE_CHLORIDE
  name = G4_POLYVINYLIDENE_CHLORIDE
  specific = 4
FEATURE [App::DocumentObjectGroupPython] C_element094  label="C_element : 052"  # scripted group (container) (typed FeaturePython)
  n = 2
  ref = C_element
FEATURE [App::DocumentObjectGroupPython] H_element086  label="H_element : 048"  # scripted group (container) (typed FeaturePython)
  n = 2
  ref = H_element
FEATURE [App::DocumentObjectGroupPython] F_element016  label="F_element : 007"  # scripted group (container) (typed FeaturePython)
  n = 2
  ref = F_element
FEATURE [App::DocumentObjectGroupPython] G4_POLYVINYLIDENE_FLUORIDE  # scripted group (container) (typed FeaturePython)
  Dunit = g/cm3
  Dvalue = 1.76
  Group = -> [C_element094,H_element086,F_element016]
  conduct = 2
  density = 1
  expand = 3
  formula = G4_POLYVINYLIDENE_FLUORIDE
  name = G4_POLYVINYLIDENE_FLUORIDE
  specific = 4
FEATURE [App::DocumentObjectGroupPython] C_element095  label="C_element : 053"  # scripted group (container) (typed FeaturePython)
  n = 6
  ref = C_element
FEATURE [App::DocumentObjectGroupPython] H_element087  label="H_element : 9"  # scripted group (container) (typed FeaturePython)
  n = 9
  ref = H_element
FEATURE [App::DocumentObjectGroupPython] N_element037  label="N_element : 016"  # scripted group (container) (typed FeaturePython)
  n = 1
  ref = N_element
FEATURE [App::DocumentObjectGroupPython] O_element084  label="O_element : 045"  # scripted group (container) (typed FeaturePython)
  n = 1
  ref = O_element
FEATURE [App::DocumentObjectGroupPython] G4_POLYVINYL_PYRROLIDONE  # scripted group (container) (typed FeaturePython)
  Dunit = g/cm3
  Dvalue = 1.25
  Group = -> [C_element095,H_element087,N_element037,O_element084]
  conduct = 2
  density = 1
  expand = 3
  formula = G4_POLYVINYL_PYRROLIDONE
  name = G4_POLYVINYL_PYRROLIDONE
  specific = 4
FEATURE [App::DocumentObjectGroupPython] K_element008  label="K_element : 1"  # scripted group (container) (typed FeaturePython)
  n = 1
  ref = K_element
FEATURE [App::DocumentObjectGroupPython] I_element006  label="I_element : 003"  # scripted group (container) (typed FeaturePython)
  n = 1
  ref = I_element
FEATURE [App::DocumentObjectGroupPython] G4_POTASSIUM_IODIDE  # scripted group (container) (typed FeaturePython)
  Dunit = g/cm3
  Dvalue = 3.13
  Group = -> [K_element008,I_element006]
  conduct = 2
  density = 1
  expand = 3
  formula = G4_POTASSIUM_IODIDE
  name = G4_POTASSIUM_IODIDE
  specific = 4
FEATURE [App::DocumentObjectGroupPython] K_element009  label="K_element : 2"  # scripted group (container) (typed FeaturePython)
  n = 2
  ref = K_element
FEATURE [App::DocumentObjectGroupPython] O_element085  label="O_element : 046"  # scripted group (container) (typed FeaturePython)
  n = 1
  ref = O_element
FEATURE [App::DocumentObjectGroupPython] G4_POTASSIUM_OXIDE  # scripted group (container) (typed FeaturePython)
  Dunit = g/cm3
  Dvalue = 2.32
  Group = -> [K_element009,O_element085]
  conduct = 2
  density = 1
  expand = 3
  formula = G4_POTASSIUM_OXIDE
  name = G4_POTASSIUM_OXIDE
  specific = 4
FEATURE [App::DocumentObjectGroupPython] C_element096  label="C_element : 054"  # scripted group (container) (typed FeaturePython)
  n = 3
  ref = C_element
FEATURE [App::DocumentObjectGroupPython] H_element088  label="H_element : 049"  # scripted group (container) (typed FeaturePython)
  n = 8
  ref = H_element
FEATURE [App::DocumentObjectGroupPython] G4_PROPANE  # scripted group (container) (typed FeaturePython)
  Dunit = g/cm3
  Dvalue = 0.00187939
  Group = -> [C_element096,H_element088]
  conduct = 2
  density = 1
  expand = 3
  formula = G4_PROPANE
  name = G4_PROPANE
  specific = 4
FEATURE [App::DocumentObjectGroupPython] C_element097  label="C_element : 055"  # scripted group (container) (typed FeaturePython)
  n = 3
  ref = C_element
FEATURE [App::DocumentObjectGroupPython] H_element089  label="H_element : 050"  # scripted group (container) (typed FeaturePython)
  n = 8
  ref = H_element
FEATURE [App::DocumentObjectGroupPython] G4_lPROPANE  # scripted group (container) (typed FeaturePython)
  Dunit = g/cm3
  Dvalue = 0.43
  Group = -> [C_element097,H_element089]
  conduct = 2
  density = 1
  expand = 3
  formula = G4_lPROPANE
  name = G4_lPROPANE
  specific = 4
FEATURE [App::DocumentObjectGroupPython] C_element098  label="C_element : 056"  # scripted group (container) (typed FeaturePython)
  n = 3
  ref = C_element
FEATURE [App::DocumentObjectGroupPython] H_element090  label="H_element : 051"  # scripted group (container) (typed FeaturePython)
  n = 8
  ref = H_element
FEATURE [App::DocumentObjectGroupPython] O_element086  label="O_element : 047"  # scripted group (container) (typed FeaturePython)
  n = 1
  ref = O_element
FEATURE [App::DocumentObjectGroupPython] G4_N_PROPYL_ALCOHOL  label="G4_N-PROPYL_ALCOHOL"  # scripted group (container) (typed FeaturePython)
  Dunit = g/cm3
  Dvalue = 0.8035
  Group = -> [C_element098,H_element090,O_element086]
  conduct = 2
  density = 1
  expand = 3
  formula = G4_N-PROPYL_ALCOHOL
  name = G4_N-PROPYL_ALCOHOL
  specific = 4
FEATURE [App::DocumentObjectGroupPython] C_element099  label="C_element : 057"  # scripted group (container) (typed FeaturePython)
  n = 5
  ref = C_element
FEATURE [App::DocumentObjectGroupPython] H_element091  label="H_element : 052"  # scripted group (container) (typed FeaturePython)
  n = 5
  ref = H_element
FEATURE [App::DocumentObjectGroupPython] N_element038  label="N_element : 017"  # scripted group (container) (typed FeaturePython)
  n = 1
  ref = N_element
FEATURE [App::DocumentObjectGroupPython] G4_PYRIDINE  # scripted group (container) (typed FeaturePython)
  Dunit = g/cm3
  Dvalue = 0.9819
  Group = -> [C_element099,H_element091,N_element038]
  conduct = 2
  density = 1
  expand = 3
  formula = G4_PYRIDINE
  name = G4_PYRIDINE
  specific = 4
FEATURE [App::DocumentObjectGroupPython] H_element092  label="H_element : 0.144"  # scripted group (container) (typed FeaturePython)
  n = 0.143711
FEATURE [App::DocumentObjectGroupPython] C_element100  label="C_element : 0.856"  # scripted group (container) (typed FeaturePython)
  n = 0.856289
FEATURE [App::DocumentObjectGroupPython] G4_RUBBER_BUTYL  # scripted group (container) (typed FeaturePython)
  Dunit = g/cm3
  Dvalue = 0.92
  Group = -> [H_element092,C_element100]
  conduct = 2
  density = 1
  expand = 3
  formula = G4_RUBBER_BUTYL
  name = G4_RUBBER_BUTYL
  specific = 4
FEATURE [App::DocumentObjectGroupPython] H_element093  label="H_element : 0.118"  # scripted group (container) (typed FeaturePython)
  n = 0.118371
FEATURE [App::DocumentObjectGroupPython] C_element101  label="C_element : 0.882"  # scripted group (container) (typed FeaturePython)
  n = 0.881629
FEATURE [App::DocumentObjectGroupPython] G4_RUBBER_NATURAL  # scripted group (container) (typed FeaturePython)
  Dunit = g/cm3
  Dvalue = 0.92
  Group = -> [H_element093,C_element101]
  conduct = 2
  density = 1
  expand = 3
  formula = G4_RUBBER_NATURAL
  name = G4_RUBBER_NATURAL
  specific = 4
FEATURE [App::DocumentObjectGroupPython] H_element094  label="H_element : 0.145"  # scripted group (container) (typed FeaturePython)
  n = 0.05692
FEATURE [App::DocumentObjectGroupPython] C_element102  label="C_element : 0.543"  # scripted group (container) (typed FeaturePython)
  n = 0.542646
FEATURE [App::DocumentObjectGroupPython] Cl_element021  label="Cl_element : 0.400"  # scripted group (container) (typed FeaturePython)
  n = 0.400434
FEATURE [App::DocumentObjectGroupPython] G4_RUBBER_NEOPRENE  # scripted group (container) (typed FeaturePython)
  Dunit = g/cm3
  Dvalue = 1.23
  Group = -> [H_element094,C_element102,Cl_element021]
  conduct = 2
  density = 1
  expand = 3
  formula = G4_RUBBER_NEOPRENE
  name = G4_RUBBER_NEOPRENE
  specific = 4
FEATURE [App::DocumentObjectGroupPython] Si_element006  label="Si_element : 1"  # scripted group (container) (typed FeaturePython)
  n = 1
  ref = Si_element
FEATURE [App::DocumentObjectGroupPython] O_element087  label="O_element : 048"  # scripted group (container) (typed FeaturePython)
  n = 2
  ref = O_element
FEATURE [App::DocumentObjectGroupPython] G4_SILICON_DIOXIDE  # scripted group (container) (typed FeaturePython)
  Dunit = g/cm3
  Dvalue = 2.32
  Group = -> [Si_element006,O_element087]
  conduct = 2
  density = 1
  expand = 3
  formula = G4_SILICON_DIOXIDE
  name = G4_SILICON_DIOXIDE
  specific = 4
FEATURE [App::DocumentObjectGroupPython] Ag_element002  label="Ag_element : 1"  # scripted group (container) (typed FeaturePython)
  n = 1
  ref = Ag_element
FEATURE [App::DocumentObjectGroupPython] Br_element005  label="Br_element : 003"  # scripted group (container) (typed FeaturePython)
  n = 1
  ref = Br_element
FEATURE [App::DocumentObjectGroupPython] G4_SILVER_BROMIDE  # scripted group (container) (typed FeaturePython)
  Dunit = g/cm3
  Dvalue = 6.473
  Group = -> [Ag_element002,Br_element005]
  conduct = 2
  density = 1
  expand = 3
  formula = G4_SILVER_BROMIDE
  name = G4_SILVER_BROMIDE
  specific = 4
FEATURE [App::DocumentObjectGroupPython] Ag_element003  label="Ag_element : 002"  # scripted group (container) (typed FeaturePython)
  n = 1
  ref = Ag_element
FEATURE [App::DocumentObjectGroupPython] Cl_element022  label="Cl_element : 011"  # scripted group (container) (typed FeaturePython)
  n = 1
  ref = Cl_element
FEATURE [App::DocumentObjectGroupPython] G4_SILVER_CHLORIDE  # scripted group (container) (typed FeaturePython)
  Dunit = g/cm3
  Dvalue = 5.56
  Group = -> [Ag_element003,Cl_element022]
  conduct = 2
  density = 1
  expand = 3
  formula = G4_SILVER_CHLORIDE
  name = G4_SILVER_CHLORIDE
  specific = 4
FEATURE [App::DocumentObjectGroupPython] Br_element006  label="Br_element : 0.423"  # scripted group (container) (typed FeaturePython)
  n = 0.422895
FEATURE [App::DocumentObjectGroupPython] Ag_element004  label="Ag_element : 0.574"  # scripted group (container) (typed FeaturePython)
  n = 0.573748
FEATURE [App::DocumentObjectGroupPython] I_element007  label="I_element : 0.649"  # scripted group (container) (typed FeaturePython)
  n = 0.003357
FEATURE [App::DocumentObjectGroupPython] G4_SILVER_HALIDES  # scripted group (container) (typed FeaturePython)
  Dunit = g/cm3
  Dvalue = 6.47
  Group = -> [Br_element006,Ag_element004,I_element007]
  conduct = 2
  density = 1
  expand = 3
  formula = G4_SILVER_HALIDES
  name = G4_SILVER_HALIDES
  specific = 4
FEATURE [App::DocumentObjectGroupPython] Ag_element005  label="Ag_element : 003"  # scripted group (container) (typed FeaturePython)
  n = 1
  ref = Ag_element
FEATURE [App::DocumentObjectGroupPython] I_element008  label="I_element : 004"  # scripted group (container) (typed FeaturePython)
  n = 1
  ref = I_element
FEATURE [App::DocumentObjectGroupPython] G4_SILVER_IODIDE  # scripted group (container) (typed FeaturePython)
  Dunit = g/cm3
  Dvalue = 6.01
  Group = -> [Ag_element005,I_element008]
  conduct = 2
  density = 1
  expand = 3
  formula = G4_SILVER_IODIDE
  name = G4_SILVER_IODIDE
  specific = 4
FEATURE [App::DocumentObjectGroupPython] H_element095  label="H_element : 0.100"  # scripted group (container) (typed FeaturePython)
  n = 0.1
FEATURE [App::DocumentObjectGroupPython] C_element103  label="C_element : 0.204"  # scripted group (container) (typed FeaturePython)
  n = 0.204
FEATURE [App::DocumentObjectGroupPython] N_element039  label="N_element : 0.759"  # scripted group (container) (typed FeaturePython)
  n = 0.042
FEATURE [App::DocumentObjectGroupPython] O_element088  label="O_element : 0.645"  # scripted group (container) (typed FeaturePython)
  n = 0.645
FEATURE [App::DocumentObjectGroupPython] Na_element013  label="Na_element : 0.100"  # scripted group (container) (typed FeaturePython)
  n = 0.002
FEATURE [App::DocumentObjectGroupPython] P_element009  label="P_element : 0.107"  # scripted group (container) (typed FeaturePython)
  n = 0.001
FEATURE [App::DocumentObjectGroupPython] S_element020  label="S_element : 0.021"  # scripted group (container) (typed FeaturePython)
  n = 0.002
FEATURE [App::DocumentObjectGroupPython] Cl_element023  label="Cl_element : 0.590"  # scripted group (container) (typed FeaturePython)
  n = 0.003
FEATURE [App::DocumentObjectGroupPython] K_element010  label="K_element : 0.001"  # scripted group (container) (typed FeaturePython)
  n = 0.001
FEATURE [App::DocumentObjectGroupPython] G4_SKIN_ICRP  # scripted group (container) (typed FeaturePython)
  Dunit = g/cm3
  Dvalue = 1.09
  Group = -> [H_element095,C_element103,N_element039,O_element088,Na_element013,P_element009,S_element020,Cl_element023,K_element010]
  conduct = 2
  density = 1
  expand = 3
  formula = G4_SKIN_ICRP
  name = G4_SKIN_ICRP
  specific = 4
FEATURE [App::DocumentObjectGroupPython] Na_element014  label="Na_element : 2"  # scripted group (container) (typed FeaturePython)
  n = 2
  ref = Na_element
FEATURE [App::DocumentObjectGroupPython] C_element104  label="C_element : 058"  # scripted group (container) (typed FeaturePython)
  n = 1
  ref = C_element
FEATURE [App::DocumentObjectGroupPython] O_element089  label="O_element : 049"  # scripted group (container) (typed FeaturePython)
  n = 3
  ref = O_element
FEATURE [App::DocumentObjectGroupPython] G4_SODIUM_CARBONATE  # scripted group (container) (typed FeaturePython)
  Dunit = g/cm3
  Dvalue = 2.532
  Group = -> [Na_element014,C_element104,O_element089]
  conduct = 2
  density = 1
  expand = 3
  formula = G4_SODIUM_CARBONATE
  name = G4_SODIUM_CARBONATE
  specific = 4
FEATURE [App::DocumentObjectGroupPython] Na_element015  label="Na_element : 1"  # scripted group (container) (typed FeaturePython)
  n = 1
  ref = Na_element
FEATURE [App::DocumentObjectGroupPython] I_element009  label="I_element : 005"  # scripted group (container) (typed FeaturePython)
  n = 1
  ref = I_element
FEATURE [App::DocumentObjectGroupPython] G4_SODIUM_IODIDE  # scripted group (container) (typed FeaturePython)
  Dunit = g/cm3
  Dvalue = 3.667
  Group = -> [Na_element015,I_element009]
  conduct = 2
  density = 1
  expand = 3
  formula = G4_SODIUM_IODIDE
  name = G4_SODIUM_IODIDE
  specific = 4
FEATURE [App::DocumentObjectGroupPython] Na_element016  label="Na_element : 003"  # scripted group (container) (typed FeaturePython)
  n = 2
  ref = Na_element
FEATURE [App::DocumentObjectGroupPython] O_element090  label="O_element : 050"  # scripted group (container) (typed FeaturePython)
  n = 1
  ref = O_element
FEATURE [App::DocumentObjectGroupPython] G4_SODIUM_MONOXIDE  # scripted group (container) (typed FeaturePython)
  Dunit = g/cm3
  Dvalue = 2.27
  Group = -> [Na_element016,O_element090]
  conduct = 2
  density = 1
  expand = 3
  formula = G4_SODIUM_MONOXIDE
  name = G4_SODIUM_MONOXIDE
  specific = 4
FEATURE [App::DocumentObjectGroupPython] Na_element017  label="Na_element : 004"  # scripted group (container) (typed FeaturePython)
  n = 1
  ref = Na_element
FEATURE [App::DocumentObjectGroupPython] N_element040  label="N_element : 018"  # scripted group (container) (typed FeaturePython)
  n = 1
  ref = N_element
FEATURE [App::DocumentObjectGroupPython] O_element091  label="O_element : 051"  # scripted group (container) (typed FeaturePython)
  n = 3
  ref = O_element
FEATURE [App::DocumentObjectGroupPython] G4_SODIUM_NITRATE  # scripted group (container) (typed FeaturePython)
  Dunit = g/cm3
  Dvalue = 2.261
  Group = -> [Na_element017,N_element040,O_element091]
  conduct = 2
  density = 1
  expand = 3
  formula = G4_SODIUM_NITRATE
  name = G4_SODIUM_NITRATE
  specific = 4
FEATURE [App::DocumentObjectGroupPython] C_element105  label="C_element : 059"  # scripted group (container) (typed FeaturePython)
  n = 14
  ref = C_element
FEATURE [App::DocumentObjectGroupPython] H_element096  label="H_element : 053"  # scripted group (container) (typed FeaturePython)
  n = 12
  ref = H_element
FEATURE [App::DocumentObjectGroupPython] G4_STILBENE  # scripted group (container) (typed FeaturePython)
  Dunit = g/cm3
  Dvalue = 0.9707
  Group = -> [C_element105,H_element096]
  conduct = 2
  density = 1
  expand = 3
  formula = G4_STILBENE
  name = G4_STILBENE
  specific = 4
FEATURE [App::DocumentObjectGroupPython] C_element106  label="C_element : 12"  # scripted group (container) (typed FeaturePython)
  n = 12
  ref = C_element
FEATURE [App::DocumentObjectGroupPython] H_element097  label="H_element : 22"  # scripted group (container) (typed FeaturePython)
  n = 22
  ref = H_element
FEATURE [App::DocumentObjectGroupPython] O_element092  label="O_element : 11"  # scripted group (container) (typed FeaturePython)
  n = 11
  ref = O_element
FEATURE [App::DocumentObjectGroupPython] G4_SUCROSE  # scripted group (container) (typed FeaturePython)
  Dunit = g/cm3
  Dvalue = 1.5805
  Group = -> [C_element106,H_element097,O_element092]
  conduct = 2
  density = 1
  expand = 3
  formula = G4_SUCROSE
  name = G4_SUCROSE
  specific = 4
FEATURE [App::DocumentObjectGroupPython] C_element107  label="C_element : 18"  # scripted group (container) (typed FeaturePython)
  n = 18
  ref = C_element
FEATURE [App::DocumentObjectGroupPython] H_element098  label="H_element : 054"  # scripted group (container) (typed FeaturePython)
  n = 14
  ref = H_element
FEATURE [App::DocumentObjectGroupPython] G4_TERPHENYL  # scripted group (container) (typed FeaturePython)
  Dunit = g/cm3
  Dvalue = 1.24
  Group = -> [C_element107,H_element098]
  conduct = 2
  density = 1
  expand = 3
  formula = G4_TERPHENYL
  name = G4_TERPHENYL
  specific = 4
FEATURE [App::DocumentObjectGroupPython] H_element099  label="H_element : 0.146"  # scripted group (container) (typed FeaturePython)
  n = 0.106
FEATURE [App::DocumentObjectGroupPython] C_element108  label="C_element : 0.883"  # scripted group (container) (typed FeaturePython)
  n = 0.099
FEATURE [App::DocumentObjectGroupPython] N_element041  label="N_element : 0.020"  # scripted group (container) (typed FeaturePython)
  n = 0.02
FEATURE [App::DocumentObjectGroupPython] O_element093  label="O_element : 0.766"  # scripted group (container) (typed FeaturePython)
  n = 0.766
FEATURE [App::DocumentObjectGroupPython] Na_element018  label="Na_element : 0.101"  # scripted group (container) (typed FeaturePython)
  n = 0.002
FEATURE [App::DocumentObjectGroupPython] P_element010  label="P_element : 0.108"  # scripted group (container) (typed FeaturePython)
  n = 0.001
FEATURE [App::DocumentObjectGroupPython] S_element021  label="S_element : 0.022"  # scripted group (container) (typed FeaturePython)
  n = 0.002
FEATURE [App::DocumentObjectGroupPython] Cl_element024  label="Cl_element : 0.002"  # scripted group (container) (typed FeaturePython)
  n = 0.002
FEATURE [App::DocumentObjectGroupPython] K_element011  label="K_element : 0.017"  # scripted group (container) (typed FeaturePython)
  n = 0.002
FEATURE [App::DocumentObjectGroupPython] G4_TESTIS_ICRP  # scripted group (container) (typed FeaturePython)
  Dunit = g/cm3
  Dvalue = 1.04
  Group = -> [H_element099,C_element108,N_element041,O_element093,Na_element018,P_element010,S_element021,Cl_element024,K_element011]
  conduct = 2
  density = 1
  expand = 3
  formula = G4_TESTIS_ICRP
  name = G4_TESTIS_ICRP
  specific = 4
FEATURE [App::DocumentObjectGroupPython] C_element109  label="C_element : 060"  # scripted group (container) (typed FeaturePython)
  n = 2
  ref = C_element
FEATURE [App::DocumentObjectGroupPython] Cl_element025  label="Cl_element : 012"  # scripted group (container) (typed FeaturePython)
  n = 4
  ref = Cl_element
FEATURE [App::DocumentObjectGroupPython] G4_TETRACHLOROETHYLENE  # scripted group (container) (typed FeaturePython)
  Dunit = g/cm3
  Dvalue = 1.625
  Group = -> [C_element109,Cl_element025]
  conduct = 2
  density = 1
  expand = 3
  formula = G4_TETRACHLOROETHYLENE
  name = G4_TETRACHLOROETHYLENE
  specific = 4
FEATURE [App::DocumentObjectGroupPython] Tl_element001  label="Tl_element : 1"  # scripted group (container) (typed FeaturePython)
  n = 1
  ref = Tl_element
FEATURE [App::DocumentObjectGroupPython] Cl_element026  label="Cl_element : 013"  # scripted group (container) (typed FeaturePython)
  n = 1
  ref = Cl_element
FEATURE [App::DocumentObjectGroupPython] G4_THALLIUM_CHLORIDE  # scripted group (container) (typed FeaturePython)
  Dunit = g/cm3
  Dvalue = 7.004
  Group = -> [Tl_element001,Cl_element026]
  conduct = 2
  density = 1
  expand = 3
  formula = G4_THALLIUM_CHLORIDE
  name = G4_THALLIUM_CHLORIDE
  specific = 4
FEATURE [App::DocumentObjectGroupPython] H_element100  label="H_element : 0.147"  # scripted group (container) (typed FeaturePython)
  n = 0.105
FEATURE [App::DocumentObjectGroupPython] C_element110  label="C_element : 0.256"  # scripted group (container) (typed FeaturePython)
  n = 0.256
FEATURE [App::DocumentObjectGroupPython] N_element042  label="N_element : 0.760"  # scripted group (container) (typed FeaturePython)
  n = 0.027
FEATURE [App::DocumentObjectGroupPython] O_element094  label="O_element : 0.602"  # scripted group (container) (typed FeaturePython)
  n = 0.602
FEATURE [App::DocumentObjectGroupPython] Na_element019  label="Na_element : 0.102"  # scripted group (container) (typed FeaturePython)
  n = 0.001
FEATURE [App::DocumentObjectGroupPython] P_element011  label="P_element : 0.109"  # scripted group (container) (typed FeaturePython)
  n = 0.002
FEATURE [App::DocumentObjectGroupPython] S_element022  label="S_element : 0.023"  # scripted group (container) (typed FeaturePython)
  n = 0.003
FEATURE [App::DocumentObjectGroupPython] Cl_element027  label="Cl_element : 0.591"  # scripted group (container) (typed FeaturePython)
  n = 0.002
FEATURE [App::DocumentObjectGroupPython] K_element012  label="K_element : 0.018"  # scripted group (container) (typed FeaturePython)
  n = 0.002
FEATURE [App::DocumentObjectGroupPython] G4_TISSUE_SOFT_ICRP  # scripted group (container) (typed FeaturePython)
  Dunit = g/cm3
  Dvalue = 1.03
  Group = -> [H_element100,C_element110,N_element042,O_element094,Na_element019,P_element011,S_element022,Cl_element027,K_element012]
  conduct = 2
  density = 1
  expand = 3
  formula = G4_TISSUE_SOFT_ICRP
  name = G4_TISSUE_SOFT_ICRP
  specific = 4
FEATURE [App::DocumentObjectGroupPython] H_element101  label="H_element : 0.148"  # scripted group (container) (typed FeaturePython)
  n = 0.101
FEATURE [App::DocumentObjectGroupPython] C_element111  label="C_element : 0.111"  # scripted group (container) (typed FeaturePython)
  n = 0.111
FEATURE [App::DocumentObjectGroupPython] N_element043  label="N_element : 0.026"  # scripted group (container) (typed FeaturePython)
  n = 0.026
FEATURE [App::DocumentObjectGroupPython] O_element095  label="O_element : 0.762"  # scripted group (container) (typed FeaturePython)
  n = 0.762
FEATURE [App::DocumentObjectGroupPython] G4_TISSUE_SOFT_ICRU_4  label="G4_TISSUE_SOFT_ICRU-4"  # scripted group (container) (typed FeaturePython)
  Dunit = g/cm3
  Dvalue = 1
  Group = -> [H_element101,C_element111,N_element043,O_element095]
  conduct = 2
  density = 1
  expand = 3
  formula = G4_TISSUE_SOFT_ICRU-4
  name = G4_TISSUE_SOFT_ICRU-4
  specific = 4
FEATURE [App::DocumentObjectGroupPython] H_element102  label="H_element : 0.149"  # scripted group (container) (typed FeaturePython)
  n = 0.101869
FEATURE [App::DocumentObjectGroupPython] C_element112  label="C_element : 0.456"  # scripted group (container) (typed FeaturePython)
  n = 0.456179
FEATURE [App::DocumentObjectGroupPython] N_element044  label="N_element : 0.761"  # scripted group (container) (typed FeaturePython)
  n = 0.035172
FEATURE [App::DocumentObjectGroupPython] O_element096  label="O_element : 0.407"  # scripted group (container) (typed FeaturePython)
  n = 0.40678
FEATURE [App::DocumentObjectGroupPython] G4_TISSUE_METHANE  label="G4_TISSUE-METHANE"  # scripted group (container) (typed FeaturePython)
  Dunit = g/cm3
  Dvalue = 0.00106409
  Group = -> [H_element102,C_element112,N_element044,O_element096]
  conduct = 2
  density = 1
  expand = 3
  formula = G4_TISSUE-METHANE
  name = G4_TISSUE-METHANE
  specific = 4
FEATURE [App::DocumentObjectGroupPython] H_element103  label="H_element : 0.103"  # scripted group (container) (typed FeaturePython)
  n = 0.102672
FEATURE [App::DocumentObjectGroupPython] C_element113  label="C_element : 0.569"  # scripted group (container) (typed FeaturePython)
  n = 0.56894
FEATURE [App::DocumentObjectGroupPython] N_element045  label="N_element : 0.762"  # scripted group (container) (typed FeaturePython)
  n = 0.035022
FEATURE [App::DocumentObjectGroupPython] O_element097  label="O_element : 0.293"  # scripted group (container) (typed FeaturePython)
  n = 0.293366
FEATURE [App::DocumentObjectGroupPython] G4_TISSUE_PROPANE  label="G4_TISSUE-PROPANE"  # scripted group (container) (typed FeaturePython)
  Dunit = g/cm3
  Dvalue = 0.00182628
  Group = -> [H_element103,C_element113,N_element045,O_element097]
  conduct = 2
  density = 1
  expand = 3
  formula = G4_TISSUE-PROPANE
  name = G4_TISSUE-PROPANE
  specific = 4
FEATURE [App::DocumentObjectGroupPython] Ti_element003  label="Ti_element : 1"  # scripted group (container) (typed FeaturePython)
  n = 1
  ref = Ti_element
FEATURE [App::DocumentObjectGroupPython] O_element098  label="O_element : 052"  # scripted group (container) (typed FeaturePython)
  n = 2
  ref = O_element
FEATURE [App::DocumentObjectGroupPython] G4_TITANIUM_DIOXIDE  # scripted group (container) (typed FeaturePython)
  Dunit = g/cm3
  Dvalue = 4.26
  Group = -> [Ti_element003,O_element098]
  conduct = 2
  density = 1
  expand = 3
  formula = G4_TITANIUM_DIOXIDE
  name = G4_TITANIUM_DIOXIDE
  specific = 4
FEATURE [App::DocumentObjectGroupPython] C_element114  label="C_element : 061"  # scripted group (container) (typed FeaturePython)
  n = 7
  ref = C_element
FEATURE [App::DocumentObjectGroupPython] H_element104  label="H_element : 055"  # scripted group (container) (typed FeaturePython)
  n = 8
  ref = H_element
FEATURE [App::DocumentObjectGroupPython] G4_TOLUENE  # scripted group (container) (typed FeaturePython)
  Dunit = g/cm3
  Dvalue = 0.8669
  Group = -> [C_element114,H_element104]
  conduct = 2
  density = 1
  expand = 3
  formula = G4_TOLUENE
  name = G4_TOLUENE
  specific = 4
FEATURE [App::DocumentObjectGroupPython] C_element115  label="C_element : 062"  # scripted group (container) (typed FeaturePython)
  n = 2
  ref = C_element
FEATURE [App::DocumentObjectGroupPython] H_element105  label="H_element : 056"  # scripted group (container) (typed FeaturePython)
  n = 1
  ref = H_element
FEATURE [App::DocumentObjectGroupPython] Cl_element028  label="Cl_element : 014"  # scripted group (container) (typed FeaturePython)
  n = 3
  ref = Cl_element
FEATURE [App::DocumentObjectGroupPython] G4_TRICHLOROETHYLENE  # scripted group (container) (typed FeaturePython)
  Dunit = g/cm3
  Dvalue = 1.46
  Group = -> [C_element115,H_element105,Cl_element028]
  conduct = 2
  density = 1
  expand = 3
  formula = G4_TRICHLOROETHYLENE
  name = G4_TRICHLOROETHYLENE
  specific = 4
FEATURE [App::DocumentObjectGroupPython] C_element116  label="C_element : 063"  # scripted group (container) (typed FeaturePython)
  n = 6
  ref = C_element
FEATURE [App::DocumentObjectGroupPython] H_element106  label="H_element : 15"  # scripted group (container) (typed FeaturePython)
  n = 15
  ref = H_element
FEATURE [App::DocumentObjectGroupPython] O_element099  label="O_element : 053"  # scripted group (container) (typed FeaturePython)
  n = 4
  ref = O_element
FEATURE [App::DocumentObjectGroupPython] P_element012  label="P_element : 1"  # scripted group (container) (typed FeaturePython)
  n = 1
  ref = P_element
FEATURE [App::DocumentObjectGroupPython] G4_TRIETHYL_PHOSPHATE  # scripted group (container) (typed FeaturePython)
  Dunit = g/cm3
  Dvalue = 1.07
  Group = -> [C_element116,H_element106,O_element099,P_element012]
  conduct = 2
  density = 1
  expand = 3
  formula = G4_TRIETHYL_PHOSPHATE
  name = G4_TRIETHYL_PHOSPHATE
  specific = 4
FEATURE [App::DocumentObjectGroupPython] W_element003  label="W_element : 003"  # scripted group (container) (typed FeaturePython)
  n = 1
  ref = W_element
FEATURE [App::DocumentObjectGroupPython] F_element017  label="F_element : 6"  # scripted group (container) (typed FeaturePython)
  n = 6
  ref = F_element
FEATURE [App::DocumentObjectGroupPython] G4_TUNGSTEN_HEXAFLUORIDE  # scripted group (container) (typed FeaturePython)
  Dunit = g/cm3
  Dvalue = 2.4
  Group = -> [W_element003,F_element017]
  conduct = 2
  density = 1
  expand = 3
  formula = G4_TUNGSTEN_HEXAFLUORIDE
  name = G4_TUNGSTEN_HEXAFLUORIDE
  specific = 4
FEATURE [App::DocumentObjectGroupPython] U_element001  label="U_element : 1"  # scripted group (container) (typed FeaturePython)
  n = 1
  ref = U_element
FEATURE [App::DocumentObjectGroupPython] C_element117  label="C_element : 064"  # scripted group (container) (typed FeaturePython)
  n = 2
  ref = C_element
FEATURE [App::DocumentObjectGroupPython] G4_URANIUM_DICARBIDE  # scripted group (container) (typed FeaturePython)
  Dunit = g/cm3
  Dvalue = 11.28
  Group = -> [U_element001,C_element117]
  conduct = 2
  density = 1
  expand = 3
  formula = G4_URANIUM_DICARBIDE
  name = G4_URANIUM_DICARBIDE
  specific = 4
FEATURE [App::DocumentObjectGroupPython] U_element002  label="U_element : 002"  # scripted group (container) (typed FeaturePython)
  n = 1
  ref = U_element
FEATURE [App::DocumentObjectGroupPython] C_element118  label="C_element : 065"  # scripted group (container) (typed FeaturePython)
  n = 1
  ref = C_element
FEATURE [App::DocumentObjectGroupPython] G4_URANIUM_MONOCARBIDE  # scripted group (container) (typed FeaturePython)
  Dunit = g/cm3
  Dvalue = 13.63
  Group = -> [U_element002,C_element118]
  conduct = 2
  density = 1
  expand = 3
  formula = G4_URANIUM_MONOCARBIDE
  name = G4_URANIUM_MONOCARBIDE
  specific = 4
FEATURE [App::DocumentObjectGroupPython] U_element003  label="U_element : 003"  # scripted group (container) (typed FeaturePython)
  n = 1
  ref = U_element
FEATURE [App::DocumentObjectGroupPython] O_element100  label="O_element : 054"  # scripted group (container) (typed FeaturePython)
  n = 2
  ref = O_element
FEATURE [App::DocumentObjectGroupPython] G4_URANIUM_OXIDE  # scripted group (container) (typed FeaturePython)
  Dunit = g/cm3
  Dvalue = 10.96
  Group = -> [U_element003,O_element100]
  conduct = 2
  density = 1
  expand = 3
  formula = G4_URANIUM_OXIDE
  name = G4_URANIUM_OXIDE
  specific = 4
FEATURE [App::DocumentObjectGroupPython] C_element119  label="C_element : 066"  # scripted group (container) (typed FeaturePython)
  n = 1
  ref = C_element
FEATURE [App::DocumentObjectGroupPython] H_element107  label="H_element : 057"  # scripted group (container) (typed FeaturePython)
  n = 4
  ref = H_element
FEATURE [App::DocumentObjectGroupPython] N_element046  label="N_element : 019"  # scripted group (container) (typed FeaturePython)
  n = 2
  ref = N_element
FEATURE [App::DocumentObjectGroupPython] O_element101  label="O_element : 055"  # scripted group (container) (typed FeaturePython)
  n = 1
  ref = O_element
FEATURE [App::DocumentObjectGroupPython] G4_UREA  # scripted group (container) (typed FeaturePython)
  Dunit = g/cm3
  Dvalue = 1.323
  Group = -> [C_element119,H_element107,N_element046,O_element101]
  conduct = 2
  density = 1
  expand = 3
  formula = G4_UREA
  name = G4_UREA
  specific = 4
FEATURE [App::DocumentObjectGroupPython] C_element120  label="C_element : 067"  # scripted group (container) (typed FeaturePython)
  n = 5
  ref = C_element
FEATURE [App::DocumentObjectGroupPython] H_element108  label="H_element : 058"  # scripted group (container) (typed FeaturePython)
  n = 11
  ref = H_element
FEATURE [App::DocumentObjectGroupPython] N_element047  label="N_element : 020"  # scripted group (container) (typed FeaturePython)
  n = 1
  ref = N_element
FEATURE [App::DocumentObjectGroupPython] O_element102  label="O_element : 056"  # scripted group (container) (typed FeaturePython)
  n = 2
  ref = O_element
FEATURE [App::DocumentObjectGroupPython] G4_VALINE  # scripted group (container) (typed FeaturePython)
  Dunit = g/cm3
  Dvalue = 1.23
  Group = -> [C_element120,H_element108,N_element047,O_element102]
  conduct = 2
  density = 1
  expand = 3
  formula = G4_VALINE
  name = G4_VALINE
  specific = 4
FEATURE [App::DocumentObjectGroupPython] H_element109  label="H_element : 0.009"  # scripted group (container) (typed FeaturePython)
  n = 0.009417
FEATURE [App::DocumentObjectGroupPython] C_element121  label="C_element : 0.281"  # scripted group (container) (typed FeaturePython)
  n = 0.280555
FEATURE [App::DocumentObjectGroupPython] F_element018  label="F_element : 0.710"  # scripted group (container) (typed FeaturePython)
  n = 0.710028
FEATURE [App::DocumentObjectGroupPython] G4_VITON  # scripted group (container) (typed FeaturePython)
  Dunit = g/cm3
  Dvalue = 1.8
  Group = -> [H_element109,C_element121,F_element018]
  conduct = 2
  density = 1
  expand = 3
  formula = G4_VITON
  name = G4_VITON
  specific = 4
FEATURE [App::DocumentObjectGroupPython] H_element110  label="H_element : 059"  # scripted group (container) (typed FeaturePython)
  n = 2
  ref = H_element
FEATURE [App::DocumentObjectGroupPython] O_element103  label="O_element : 057"  # scripted group (container) (typed FeaturePython)
  n = 1
  ref = O_element
FEATURE [App::DocumentObjectGroupPython] G4_WATER  # scripted group (container) (typed FeaturePython)
  Dunit = g/cm3
  Dvalue = 1
  Group = -> [H_element110,O_element103]
  conduct = 2
  density = 1
  expand = 3
  formula = G4_WATER
  name = G4_WATER
  specific = 4
FEATURE [App::DocumentObjectGroupPython] H_element111  label="H_element : 060"  # scripted group (container) (typed FeaturePython)
  n = 2
  ref = H_element
FEATURE [App::DocumentObjectGroupPython] O_element104  label="O_element : 058"  # scripted group (container) (typed FeaturePython)
  n = 1
  ref = O_element
FEATURE [App::DocumentObjectGroupPython] G4_WATER_VAPOR  # scripted group (container) (typed FeaturePython)
  Dunit = g/cm3
  Dvalue = 0.000756182
  Group = -> [H_element111,O_element104]
  conduct = 2
  density = 1
  expand = 3
  formula = G4_WATER_VAPOR
  name = G4_WATER_VAPOR
  specific = 4
FEATURE [App::DocumentObjectGroupPython] C_element122  label="C_element : 068"  # scripted group (container) (typed FeaturePython)
  n = 8
  ref = C_element
FEATURE [App::DocumentObjectGroupPython] H_element112  label="H_element : 061"  # scripted group (container) (typed FeaturePython)
  n = 10
  ref = H_element
FEATURE [App::DocumentObjectGroupPython] G4_XYLENE  # scripted group (container) (typed FeaturePython)
  Dunit = g/cm3
  Dvalue = 0.87
  Group = -> [C_element122,H_element112]
  conduct = 2
  density = 1
  expand = 3
  formula = G4_XYLENE
  name = G4_XYLENE
  specific = 4
FEATURE [App::DocumentObjectGroupPython] C_element123  label="C_element : 069"  # scripted group (container) (typed FeaturePython)
  n = 1
  ref = C_element
FEATURE [App::DocumentObjectGroupPython] G4_GRAPHITE  # scripted group (container) (typed FeaturePython)
  Dunit = g/cm3
  Dvalue = 2.21
  Group = -> [C_element123]
  conduct = 2
  density = 1
  expand = 3
  formula = G4_GRAPHITE
  name = G4_GRAPHITE
  specific = 4
FEATURE [App::DocumentObjectGroupPython] NIST  # scripted group (container) (typed FeaturePython)
  Group = -> [G4_A_150_TISSUE,G4_ACETONE,G4_ACETYLENE,G4_ADENINE,G4_ADIPOSE_TISSUE_ICRP,G4_AIR,G4_ALANINE,G4_ALUMINUM_OXIDE,G4_AMBER,G4_AMMONIA,G4_ANILINE,G4_ANTHRACENE,G4_B_100_BONE,G4_BAKELITE,G4_BARIUM_FLUORIDE,G4_BARIUM_SULFATE,G4_BENZENE,G4_BERYLLIUM_OXIDE,G4_BGO,G4_BLOOD_ICRP,G4_BONE_COMPACT_ICRU,G4_BONE_CORTICAL_ICRP,G4_BORON_CARBIDE,G4_BORON_OXIDE,G4_BRAIN_ICRP,G4_BUTANE,G4_N_BUTYL_ALCOHOL,G4_C_552,+152 more]
FEATURE [App::DocumentObjectGroupPython] H_element113  label="H_element : 062"  # scripted group (container) (typed FeaturePython)
  n = 1
  ref = H_element
FEATURE [App::DocumentObjectGroupPython] G4_H  # scripted group (container) (typed FeaturePython)
  Dunit = g/cm3
  Dvalue = 8.3748e-05
  Group = -> [H_element113]
  conduct = 2
  density = 1
  expand = 3
  formula = H
  name = G4_H
  specific = 4
FEATURE [App::DocumentObjectGroupPython] He_element001  label="He_element : 1"  # scripted group (container) (typed FeaturePython)
  n = 1
  ref = He_element
FEATURE [App::DocumentObjectGroupPython] G4_He  # scripted group (container) (typed FeaturePython)
  Dunit = g/cm3
  Dvalue = 0.000166322
  Group = -> [He_element001]
  conduct = 2
  density = 1
  expand = 3
  formula = He
  name = G4_He
  specific = 4
FEATURE [App::DocumentObjectGroupPython] Li_element008  label="Li_element : 008"  # scripted group (container) (typed FeaturePython)
  n = 1
  ref = Li_element
FEATURE [App::DocumentObjectGroupPython] G4_Li  # scripted group (container) (typed FeaturePython)
  Dunit = g/cm3
  Dvalue = 0.534
  Group = -> [Li_element008]
  conduct = 2
  density = 1
  expand = 3
  formula = Li
  name = G4_Li
  specific = 4
FEATURE [App::DocumentObjectGroupPython] Be_element002  label="Be_element : 002"  # scripted group (container) (typed FeaturePython)
  n = 1
  ref = Be_element
FEATURE [App::DocumentObjectGroupPython] G4_Be  # scripted group (container) (typed FeaturePython)
  Dunit = g/cm3
  Dvalue = 1.848
  Group = -> [Be_element002]
  conduct = 2
  density = 1
  expand = 3
  formula = Be
  name = G4_Be
  specific = 4
FEATURE [App::DocumentObjectGroupPython] B_element007  label="B_element : 007"  # scripted group (container) (typed FeaturePython)
  n = 1
  ref = B_element
FEATURE [App::DocumentObjectGroupPython] G4_B  # scripted group (container) (typed FeaturePython)
  Dunit = g/cm3
  Dvalue = 2.37
  Group = -> [B_element007]
  conduct = 2
  density = 1
  expand = 3
  formula = B
  name = G4_B
  specific = 4
FEATURE [App::DocumentObjectGroupPython] C_element124  label="C_element : 070"  # scripted group (container) (typed FeaturePython)
  n = 1
  ref = C_element
FEATURE [App::DocumentObjectGroupPython] G4_C  # scripted group (container) (typed FeaturePython)
  Dunit = g/cm3
  Dvalue = 2
  Group = -> [C_element124]
  conduct = 2
  density = 1
  expand = 3
  formula = C
  name = G4_C
  specific = 4
FEATURE [App::DocumentObjectGroupPython] N_element048  label="N_element : 021"  # scripted group (container) (typed FeaturePython)
  n = 1
  ref = N_element
FEATURE [App::DocumentObjectGroupPython] G4_N  # scripted group (container) (typed FeaturePython)
  Dunit = g/cm3
  Dvalue = 0.0011652
  Group = -> [N_element048]
  conduct = 2
  density = 1
  expand = 3
  formula = N
  name = G4_N
  specific = 4
FEATURE [App::DocumentObjectGroupPython] O_element105  label="O_element : 059"  # scripted group (container) (typed FeaturePython)
  n = 1
  ref = O_element
FEATURE [App::DocumentObjectGroupPython] G4_O  # scripted group (container) (typed FeaturePython)
  Dunit = g/cm3
  Dvalue = 0.00133151
  Group = -> [O_element105]
  conduct = 2
  density = 1
  expand = 3
  formula = O
  name = G4_O
  specific = 4
FEATURE [App::DocumentObjectGroupPython] F_element019  label="F_element : 008"  # scripted group (container) (typed FeaturePython)
  n = 1
  ref = F_element
FEATURE [App::DocumentObjectGroupPython] G4_F  # scripted group (container) (typed FeaturePython)
  Dunit = g/cm3
  Dvalue = 0.00158029
  Group = -> [F_element019]
  conduct = 2
  density = 1
  expand = 3
  formula = F
  name = G4_F
  specific = 4
FEATURE [App::DocumentObjectGroupPython] Ne_element001  label="Ne_element : 1"  # scripted group (container) (typed FeaturePython)
  n = 1
  ref = Ne_element
FEATURE [App::DocumentObjectGroupPython] G4_Ne  # scripted group (container) (typed FeaturePython)
  Dunit = g/cm3
  Dvalue = 0.000838505
  Group = -> [Ne_element001]
  conduct = 2
  density = 1
  expand = 3
  formula = Ne
  name = G4_Ne
  specific = 4
FEATURE [App::DocumentObjectGroupPython] Na_element020  label="Na_element : 005"  # scripted group (container) (typed FeaturePython)
  n = 1
  ref = Na_element
FEATURE [App::DocumentObjectGroupPython] G4_Na  # scripted group (container) (typed FeaturePython)
  Dunit = g/cm3
  Dvalue = 0.971
  Group = -> [Na_element020]
  conduct = 2
  density = 1
  expand = 3
  formula = Na
  name = G4_Na
  specific = 4
FEATURE [App::DocumentObjectGroupPython] Mg_element011  label="Mg_element : 005"  # scripted group (container) (typed FeaturePython)
  n = 1
  ref = Mg_element
FEATURE [App::DocumentObjectGroupPython] G4_Mg  # scripted group (container) (typed FeaturePython)
  Dunit = g/cm3
  Dvalue = 1.74
  Group = -> [Mg_element011]
  conduct = 2
  density = 1
  expand = 3
  formula = Mg
  name = G4_Mg
  specific = 4
FEATURE [App::DocumentObjectGroupPython] Al_element004  label="Al_element : 1"  # scripted group (container) (typed FeaturePython)
  n = 1
  ref = Al_element
FEATURE [App::DocumentObjectGroupPython] G4_Al  # scripted group (container) (typed FeaturePython)
  Dunit = g/cm3
  Dvalue = 2.699
  Group = -> [Al_element004]
  conduct = 2
  density = 1
  expand = 3
  formula = Al
  name = G4_Al
  specific = 4
FEATURE [App::DocumentObjectGroupPython] Si_element007  label="Si_element : 002"  # scripted group (container) (typed FeaturePython)
  n = 1
  ref = Si_element
FEATURE [App::DocumentObjectGroupPython] G4_Si  # scripted group (container) (typed FeaturePython)
  Dunit = g/cm3
  Dvalue = 2.33
  Group = -> [Si_element007]
  conduct = 2
  density = 1
  expand = 3
  formula = Si
  name = G4_Si
  specific = 4
FEATURE [App::DocumentObjectGroupPython] P_element013  label="P_element : 002"  # scripted group (container) (typed FeaturePython)
  n = 1
  ref = P_element
FEATURE [App::DocumentObjectGroupPython] G4_P  # scripted group (container) (typed FeaturePython)
  Dunit = g/cm3
  Dvalue = 2.2
  Group = -> [P_element013]
  conduct = 2
  density = 1
  expand = 3
  formula = P
  name = G4_P
  specific = 4
FEATURE [App::DocumentObjectGroupPython] S_element023  label="S_element : 007"  # scripted group (container) (typed FeaturePython)
  n = 1
  ref = S_element
FEATURE [App::DocumentObjectGroupPython] G4_S  # scripted group (container) (typed FeaturePython)
  Dunit = g/cm3
  Dvalue = 2
  Group = -> [S_element023]
  conduct = 2
  density = 1
  expand = 3
  formula = S
  name = G4_S
  specific = 4
FEATURE [App::DocumentObjectGroupPython] Cl_element029  label="Cl_element : 015"  # scripted group (container) (typed FeaturePython)
  n = 1
  ref = Cl_element
FEATURE [App::DocumentObjectGroupPython] G4_Cl  # scripted group (container) (typed FeaturePython)
  Dunit = g/cm3
  Dvalue = 0.00299473
  Group = -> [Cl_element029]
  conduct = 2
  density = 1
  expand = 3
  formula = Cl
  name = G4_Cl
  specific = 4
FEATURE [App::DocumentObjectGroupPython] Ar_element002  label="Ar_element : 1"  # scripted group (container) (typed FeaturePython)
  n = 1
  ref = Ar_element
FEATURE [App::DocumentObjectGroupPython] G4_Ar  # scripted group (container) (typed FeaturePython)
  Dunit = g/cm3
  Dvalue = 0.00166201
  Group = -> [Ar_element002]
  conduct = 2
  density = 1
  expand = 3
  formula = Ar
  name = G4_Ar
  specific = 4
FEATURE [App::DocumentObjectGroupPython] K_element013  label="K_element : 003"  # scripted group (container) (typed FeaturePython)
  n = 1
  ref = K_element
FEATURE [App::DocumentObjectGroupPython] G4_K  # scripted group (container) (typed FeaturePython)
  Dunit = g/cm3
  Dvalue = 0.862
  Group = -> [K_element013]
  conduct = 2
  density = 1
  expand = 3
  formula = K
  name = G4_K
  specific = 4
FEATURE [App::DocumentObjectGroupPython] Ca_element014  label="Ca_element : 007"  # scripted group (container) (typed FeaturePython)
  n = 1
  ref = Ca_element
FEATURE [App::DocumentObjectGroupPython] G4_Ca  # scripted group (container) (typed FeaturePython)
  Dunit = g/cm3
  Dvalue = 1.55
  Group = -> [Ca_element014]
  conduct = 2
  density = 1
  expand = 3
  formula = Ca
  name = G4_Ca
  specific = 4
FEATURE [App::DocumentObjectGroupPython] Sc_element001  label="Sc_element : 1"  # scripted group (container) (typed FeaturePython)
  n = 1
  ref = Sc_element
FEATURE [App::DocumentObjectGroupPython] G4_Sc  # scripted group (container) (typed FeaturePython)
  Dunit = g/cm3
  Dvalue = 2.989
  Group = -> [Sc_element001]
  conduct = 2
  density = 1
  expand = 3
  formula = Sc
  name = G4_Sc
  specific = 4
FEATURE [App::DocumentObjectGroupPython] Ti_element004  label="Ti_element : 002"  # scripted group (container) (typed FeaturePython)
  n = 1
  ref = Ti_element
FEATURE [App::DocumentObjectGroupPython] G4_Ti  # scripted group (container) (typed FeaturePython)
  Dunit = g/cm3
  Dvalue = 4.54
  Group = -> [Ti_element004]
  conduct = 2
  density = 1
  expand = 3
  formula = Ti
  name = G4_Ti
  specific = 4
FEATURE [App::DocumentObjectGroupPython] V_element001  label="V_element : 1"  # scripted group (container) (typed FeaturePython)
  n = 1
  ref = V_element
FEATURE [App::DocumentObjectGroupPython] G4_V  # scripted group (container) (typed FeaturePython)
  Dunit = g/cm3
  Dvalue = 6.11
  Group = -> [V_element001]
  conduct = 2
  density = 1
  expand = 3
  formula = V
  name = G4_V
  specific = 4
FEATURE [App::DocumentObjectGroupPython] Cr_element001  label="Cr_element : 1"  # scripted group (container) (typed FeaturePython)
  n = 1
  ref = Cr_element
FEATURE [App::DocumentObjectGroupPython] G4_Cr  # scripted group (container) (typed FeaturePython)
  Dunit = g/cm3
  Dvalue = 7.18
  Group = -> [Cr_element001]
  conduct = 2
  density = 1
  expand = 3
  formula = Cr
  name = G4_Cr
  specific = 4
FEATURE [App::DocumentObjectGroupPython] Mn_element001  label="Mn_element : 1"  # scripted group (container) (typed FeaturePython)
  n = 1
  ref = Mn_element
FEATURE [App::DocumentObjectGroupPython] G4_Mn  # scripted group (container) (typed FeaturePython)
  Dunit = g/cm3
  Dvalue = 7.44
  Group = -> [Mn_element001]
  conduct = 2
  density = 1
  expand = 3
  formula = Mn
  name = G4_Mn
  specific = 4
FEATURE [App::DocumentObjectGroupPython] Fe_element007  label="Fe_element : 004"  # scripted group (container) (typed FeaturePython)
  n = 1
  ref = Fe_element
FEATURE [App::DocumentObjectGroupPython] G4_Fe  # scripted group (container) (typed FeaturePython)
  Dunit = g/cm3
  Dvalue = 7.874
  Group = -> [Fe_element007]
  conduct = 2
  density = 1
  expand = 3
  formula = Fe
  name = G4_Fe
  specific = 4
FEATURE [App::DocumentObjectGroupPython] Co_element001  label="Co_element : 1"  # scripted group (container) (typed FeaturePython)
  n = 1
  ref = Co_element
FEATURE [App::DocumentObjectGroupPython] G4_Co  # scripted group (container) (typed FeaturePython)
  Dunit = g/cm3
  Dvalue = 8.9
  Group = -> [Co_element001]
  conduct = 2
  density = 1
  expand = 3
  formula = Co
  name = G4_Co
  specific = 4
FEATURE [App::DocumentObjectGroupPython] Ni_element001  label="Ni_element : 1"  # scripted group (container) (typed FeaturePython)
  n = 1
  ref = Ni_element
FEATURE [App::DocumentObjectGroupPython] G4_Ni  # scripted group (container) (typed FeaturePython)
  Dunit = g/cm3
  Dvalue = 8.902
  Group = -> [Ni_element001]
  conduct = 2
  density = 1
  expand = 3
  formula = Ni
  name = G4_Ni
  specific = 4
FEATURE [App::DocumentObjectGroupPython] Cu_element001  label="Cu_element : 1"  # scripted group (container) (typed FeaturePython)
  n = 1
  ref = Cu_element
FEATURE [App::DocumentObjectGroupPython] G4_Cu  # scripted group (container) (typed FeaturePython)
  Dunit = g/cm3
  Dvalue = 8.96
  Group = -> [Cu_element001]
  conduct = 2
  density = 1
  expand = 3
  formula = Cu
  name = G4_Cu
  specific = 4
FEATURE [App::DocumentObjectGroupPython] Zn_element001  label="Zn_element : 1"  # scripted group (container) (typed FeaturePython)
  n = 1
  ref = Zn_element
FEATURE [App::DocumentObjectGroupPython] G4_Zn  # scripted group (container) (typed FeaturePython)
  Dunit = g/cm3
  Dvalue = 7.133
  Group = -> [Zn_element001]
  conduct = 2
  density = 1
  expand = 3
  formula = Zn
  name = G4_Zn
  specific = 4
FEATURE [App::DocumentObjectGroupPython] Ga_element002  label="Ga_element : 002"  # scripted group (container) (typed FeaturePython)
  n = 1
  ref = Ga_element
FEATURE [App::DocumentObjectGroupPython] G4_Ga  # scripted group (container) (typed FeaturePython)
  Dunit = g/cm3
  Dvalue = 5.904
  Group = -> [Ga_element002]
  conduct = 2
  density = 1
  expand = 3
  formula = Ga
  name = G4_Ga
  specific = 4
FEATURE [App::DocumentObjectGroupPython] Ge_element002  label="Ge_element : 1"  # scripted group (container) (typed FeaturePython)
  n = 1
  ref = Ge_element
FEATURE [App::DocumentObjectGroupPython] G4_Ge  # scripted group (container) (typed FeaturePython)
  Dunit = g/cm3
  Dvalue = 5.323
  Group = -> [Ge_element002]
  conduct = 2
  density = 1
  expand = 3
  formula = Ge
  name = G4_Ge
  specific = 4
FEATURE [App::DocumentObjectGroupPython] As_element003  label="As_element : 002"  # scripted group (container) (typed FeaturePython)
  n = 1
  ref = As_element
FEATURE [App::DocumentObjectGroupPython] G4_As  # scripted group (container) (typed FeaturePython)
  Dunit = g/cm3
  Dvalue = 5.73
  Group = -> [As_element003]
  conduct = 2
  density = 1
  expand = 3
  formula = As
  name = G4_As
  specific = 4
FEATURE [App::DocumentObjectGroupPython] Se_element001  label="Se_element : 1"  # scripted group (container) (typed FeaturePython)
  n = 1
  ref = Se_element
FEATURE [App::DocumentObjectGroupPython] G4_Se  # scripted group (container) (typed FeaturePython)
  Dunit = g/cm3
  Dvalue = 4.5
  Group = -> [Se_element001]
  conduct = 2
  density = 1
  expand = 3
  formula = Se
  name = G4_Se
  specific = 4
FEATURE [App::DocumentObjectGroupPython] Br_element007  label="Br_element : 004"  # scripted group (container) (typed FeaturePython)
  n = 1
  ref = Br_element
FEATURE [App::DocumentObjectGroupPython] G4_Br  # scripted group (container) (typed FeaturePython)
  Dunit = g/cm3
  Dvalue = 0.0070721
  Group = -> [Br_element007]
  conduct = 2
  density = 1
  expand = 3
  formula = Br
  name = G4_Br
  specific = 4
FEATURE [App::DocumentObjectGroupPython] Kr_element001  label="Kr_element : 1"  # scripted group (container) (typed FeaturePython)
  n = 1
  ref = Kr_element
FEATURE [App::DocumentObjectGroupPython] G4_Kr  # scripted group (container) (typed FeaturePython)
  Dunit = g/cm3
  Dvalue = 0.00347832
  Group = -> [Kr_element001]
  conduct = 2
  density = 1
  expand = 3
  formula = Kr
  name = G4_Kr
  specific = 4
FEATURE [App::DocumentObjectGroupPython] Rb_element001  label="Rb_element : 1"  # scripted group (container) (typed FeaturePython)
  n = 1
  ref = Rb_element
FEATURE [App::DocumentObjectGroupPython] G4_Rb  # scripted group (container) (typed FeaturePython)
  Dunit = g/cm3
  Dvalue = 1.532
  Group = -> [Rb_element001]
  conduct = 2
  density = 1
  expand = 3
  formula = Rb
  name = G4_Rb
  specific = 4
FEATURE [App::DocumentObjectGroupPython] Sr_element001  label="Sr_element : 1"  # scripted group (container) (typed FeaturePython)
  n = 1
  ref = Sr_element
FEATURE [App::DocumentObjectGroupPython] G4_Sr  # scripted group (container) (typed FeaturePython)
  Dunit = g/cm3
  Dvalue = 2.54
  Group = -> [Sr_element001]
  conduct = 2
  density = 1
  expand = 3
  formula = Sr
  name = G4_Sr
  specific = 4
FEATURE [App::DocumentObjectGroupPython] Y_element001  label="Y_element : 1"  # scripted group (container) (typed FeaturePython)
  n = 1
  ref = Y_element
FEATURE [App::DocumentObjectGroupPython] G4_Y  # scripted group (container) (typed FeaturePython)
  Dunit = g/cm3
  Dvalue = 4.469
  Group = -> [Y_element001]
  conduct = 2
  density = 1
  expand = 3
  formula = Y
  name = G4_Y
  specific = 4
FEATURE [App::DocumentObjectGroupPython] Zr_element001  label="Zr_element : 1"  # scripted group (container) (typed FeaturePython)
  n = 1
  ref = Zr_element
FEATURE [App::DocumentObjectGroupPython] G4_Zr  # scripted group (container) (typed FeaturePython)
  Dunit = g/cm3
  Dvalue = 6.506
  Group = -> [Zr_element001]
  conduct = 2
  density = 1
  expand = 3
  formula = Zr
  name = G4_Zr
  specific = 4
FEATURE [App::DocumentObjectGroupPython] Nb_element001  label="Nb_element : 1"  # scripted group (container) (typed FeaturePython)
  n = 1
  ref = Nb_element
FEATURE [App::DocumentObjectGroupPython] G4_Nb  # scripted group (container) (typed FeaturePython)
  Dunit = g/cm3
  Dvalue = 8.57
  Group = -> [Nb_element001]
  conduct = 2
  density = 1
  expand = 3
  formula = Nb
  name = G4_Nb
  specific = 4
FEATURE [App::DocumentObjectGroupPython] Mo_element001  label="Mo_element : 1"  # scripted group (container) (typed FeaturePython)
  n = 1
  ref = Mo_element
FEATURE [App::DocumentObjectGroupPython] G4_Mo  # scripted group (container) (typed FeaturePython)
  Dunit = g/cm3
  Dvalue = 10.22
  Group = -> [Mo_element001]
  conduct = 2
  density = 1
  expand = 3
  formula = Mo
  name = G4_Mo
  specific = 4
FEATURE [App::DocumentObjectGroupPython] Tc_element001  label="Tc_element : 1"  # scripted group (container) (typed FeaturePython)
  n = 1
  ref = Tc_element
FEATURE [App::DocumentObjectGroupPython] G4_Tc  # scripted group (container) (typed FeaturePython)
  Dunit = g/cm3
  Dvalue = 11.5
  Group = -> [Tc_element001]
  conduct = 2
  density = 1
  expand = 3
  formula = Tc
  name = G4_Tc
  specific = 4
FEATURE [App::DocumentObjectGroupPython] Ru_element001  label="Ru_element : 1"  # scripted group (container) (typed FeaturePython)
  n = 1
  ref = Ru_element
FEATURE [App::DocumentObjectGroupPython] G4_Ru  # scripted group (container) (typed FeaturePython)
  Dunit = g/cm3
  Dvalue = 12.41
  Group = -> [Ru_element001]
  conduct = 2
  density = 1
  expand = 3
  formula = Ru
  name = G4_Ru
  specific = 4
FEATURE [App::DocumentObjectGroupPython] Rh_element001  label="Rh_element : 1"  # scripted group (container) (typed FeaturePython)
  n = 1
  ref = Rh_element
FEATURE [App::DocumentObjectGroupPython] G4_Rh  # scripted group (container) (typed FeaturePython)
  Dunit = g/cm3
  Dvalue = 12.41
  Group = -> [Rh_element001]
  conduct = 2
  density = 1
  expand = 3
  formula = Rh
  name = G4_Rh
  specific = 4
FEATURE [App::DocumentObjectGroupPython] Pd_element001  label="Pd_element : 1"  # scripted group (container) (typed FeaturePython)
  n = 1
  ref = Pd_element
FEATURE [App::DocumentObjectGroupPython] G4_Pd  # scripted group (container) (typed FeaturePython)
  Dunit = g/cm3
  Dvalue = 12.02
  Group = -> [Pd_element001]
  conduct = 2
  density = 1
  expand = 3
  formula = Pd
  name = G4_Pd
  specific = 4
FEATURE [App::DocumentObjectGroupPython] Ag_element006  label="Ag_element : 004"  # scripted group (container) (typed FeaturePython)
  n = 1
  ref = Ag_element
FEATURE [App::DocumentObjectGroupPython] G4_Ag  # scripted group (container) (typed FeaturePython)
  Dunit = g/cm3
  Dvalue = 10.5
  Group = -> [Ag_element006]
  conduct = 2
  density = 1
  expand = 3
  formula = Ag
  name = G4_Ag
  specific = 4
FEATURE [App::DocumentObjectGroupPython] Cd_element003  label="Cd_element : 003"  # scripted group (container) (typed FeaturePython)
  n = 1
  ref = Cd_element
FEATURE [App::DocumentObjectGroupPython] G4_Cd  # scripted group (container) (typed FeaturePython)
  Dunit = g/cm3
  Dvalue = 8.65
  Group = -> [Cd_element003]
  conduct = 2
  density = 1
  expand = 3
  formula = Cd
  name = G4_Cd
  specific = 4
FEATURE [App::DocumentObjectGroupPython] In_element001  label="In_element : 1"  # scripted group (container) (typed FeaturePython)
  n = 1
  ref = In_element
FEATURE [App::DocumentObjectGroupPython] G4_In  # scripted group (container) (typed FeaturePython)
  Dunit = g/cm3
  Dvalue = 7.31
  Group = -> [In_element001]
  conduct = 2
  density = 1
  expand = 3
  formula = In
  name = G4_In
  specific = 4
FEATURE [App::DocumentObjectGroupPython] Sn_element001  label="Sn_element : 1"  # scripted group (container) (typed FeaturePython)
  n = 1
  ref = Sn_element
FEATURE [App::DocumentObjectGroupPython] G4_Sn  # scripted group (container) (typed FeaturePython)
  Dunit = g/cm3
  Dvalue = 7.31
  Group = -> [Sn_element001]
  conduct = 2
  density = 1
  expand = 3
  formula = Sn
  name = G4_Sn
  specific = 4
FEATURE [App::DocumentObjectGroupPython] Sb_element001  label="Sb_element : 1"  # scripted group (container) (typed FeaturePython)
  n = 1
  ref = Sb_element
FEATURE [App::DocumentObjectGroupPython] G4_Sb  # scripted group (container) (typed FeaturePython)
  Dunit = g/cm3
  Dvalue = 6.691
  Group = -> [Sb_element001]
  conduct = 2
  density = 1
  expand = 3
  formula = Sb
  name = G4_Sb
  specific = 4
FEATURE [App::DocumentObjectGroupPython] Te_element002  label="Te_element : 002"  # scripted group (container) (typed FeaturePython)
  n = 1
  ref = Te_element
FEATURE [App::DocumentObjectGroupPython] G4_Te  # scripted group (container) (typed FeaturePython)
  Dunit = g/cm3
  Dvalue = 6.24
  Group = -> [Te_element002]
  conduct = 2
  density = 1
  expand = 3
  formula = Te
  name = G4_Te
  specific = 4
FEATURE [App::DocumentObjectGroupPython] I_element010  label="I_element : 006"  # scripted group (container) (typed FeaturePython)
  n = 1
  ref = I_element
FEATURE [App::DocumentObjectGroupPython] G4_I  # scripted group (container) (typed FeaturePython)
  Dunit = g/cm3
  Dvalue = 4.93
  Group = -> [I_element010]
  conduct = 2
  density = 1
  expand = 3
  formula = I
  name = G4_I
  specific = 4
FEATURE [App::DocumentObjectGroupPython] Xe_element001  label="Xe_element : 1"  # scripted group (container) (typed FeaturePython)
  n = 1
  ref = Xe_element
FEATURE [App::DocumentObjectGroupPython] G4_Xe  # scripted group (container) (typed FeaturePython)
  Dunit = g/cm3
  Dvalue = 0.00548536
  Group = -> [Xe_element001]
  conduct = 2
  density = 1
  expand = 3
  formula = Xe
  name = G4_Xe
  specific = 4
FEATURE [App::DocumentObjectGroupPython] Cs_element003  label="Cs_element : 003"  # scripted group (container) (typed FeaturePython)
  n = 1
  ref = Cs_element
FEATURE [App::DocumentObjectGroupPython] G4_Cs  # scripted group (container) (typed FeaturePython)
  Dunit = g/cm3
  Dvalue = 1.873
  Group = -> [Cs_element003]
  conduct = 2
  density = 1
  expand = 3
  formula = Cs
  name = G4_Cs
  specific = 4
FEATURE [App::DocumentObjectGroupPython] Ba_element003  label="Ba_element : 003"  # scripted group (container) (typed FeaturePython)
  n = 1
  ref = Ba_element
FEATURE [App::DocumentObjectGroupPython] G4_Ba  # scripted group (container) (typed FeaturePython)
  Dunit = g/cm3
  Dvalue = 3.5
  Group = -> [Ba_element003]
  conduct = 2
  density = 1
  expand = 3
  formula = Ba
  name = G4_Ba
  specific = 4
FEATURE [App::DocumentObjectGroupPython] La_element003  label="La_element : 003"  # scripted group (container) (typed FeaturePython)
  n = 1
  ref = La_element
FEATURE [App::DocumentObjectGroupPython] G4_La  # scripted group (container) (typed FeaturePython)
  Dunit = g/cm3
  Dvalue = 6.154
  Group = -> [La_element003]
  conduct = 2
  density = 1
  expand = 3
  formula = La
  name = G4_La
  specific = 4
FEATURE [App::DocumentObjectGroupPython] Ce_element002  label="Ce_element : 1"  # scripted group (container) (typed FeaturePython)
  n = 1
  ref = Ce_element
FEATURE [App::DocumentObjectGroupPython] G4_Ce  # scripted group (container) (typed FeaturePython)
  Dunit = g/cm3
  Dvalue = 6.657
  Group = -> [Ce_element002]
  conduct = 2
  density = 1
  expand = 3
  formula = Ce
  name = G4_Ce
  specific = 4
FEATURE [App::DocumentObjectGroupPython] Pr_element001  label="Pr_element : 1"  # scripted group (container) (typed FeaturePython)
  n = 1
  ref = Pr_element
FEATURE [App::DocumentObjectGroupPython] G4_Pr  # scripted group (container) (typed FeaturePython)
  Dunit = g/cm3
  Dvalue = 6.71
  Group = -> [Pr_element001]
  conduct = 2
  density = 1
  expand = 3
  formula = Pr
  name = G4_Pr
  specific = 4
FEATURE [App::DocumentObjectGroupPython] Nd_element001  label="Nd_element : 1"  # scripted group (container) (typed FeaturePython)
  n = 1
  ref = Nd_element
FEATURE [App::DocumentObjectGroupPython] G4_Nd  # scripted group (container) (typed FeaturePython)
  Dunit = g/cm3
  Dvalue = 6.9
  Group = -> [Nd_element001]
  conduct = 2
  density = 1
  expand = 3
  formula = Nd
  name = G4_Nd
  specific = 4
FEATURE [App::DocumentObjectGroupPython] Pm_element001  label="Pm_element : 1"  # scripted group (container) (typed FeaturePython)
  n = 1
  ref = Pm_element
FEATURE [App::DocumentObjectGroupPython] G4_Pm  # scripted group (container) (typed FeaturePython)
  Dunit = g/cm3
  Dvalue = 7.22
  Group = -> [Pm_element001]
  conduct = 2
  density = 1
  expand = 3
  formula = Pm
  name = G4_Pm
  specific = 4
FEATURE [App::DocumentObjectGroupPython] Sm_element001  label="Sm_element : 1"  # scripted group (container) (typed FeaturePython)
  n = 1
  ref = Sm_element
FEATURE [App::DocumentObjectGroupPython] G4_Sm  # scripted group (container) (typed FeaturePython)
  Dunit = g/cm3
  Dvalue = 7.46
  Group = -> [Sm_element001]
  conduct = 2
  density = 1
  expand = 3
  formula = Sm
  name = G4_Sm
  specific = 4
FEATURE [App::DocumentObjectGroupPython] Eu_element001  label="Eu_element : 1"  # scripted group (container) (typed FeaturePython)
  n = 1
  ref = Eu_element
FEATURE [App::DocumentObjectGroupPython] G4_Eu  # scripted group (container) (typed FeaturePython)
  Dunit = g/cm3
  Dvalue = 5.243
  Group = -> [Eu_element001]
  conduct = 2
  density = 1
  expand = 3
  formula = Eu
  name = G4_Eu
  specific = 4
FEATURE [App::DocumentObjectGroupPython] Gd_element002  label="Gd_element : 1"  # scripted group (container) (typed FeaturePython)
  n = 1
  ref = Gd_element
FEATURE [App::DocumentObjectGroupPython] G4_Gd  # scripted group (container) (typed FeaturePython)
  Dunit = g/cm3
  Dvalue = 7.9004
  Group = -> [Gd_element002]
  conduct = 2
  density = 1
  expand = 3
  formula = Gd
  name = G4_Gd
  specific = 4
FEATURE [App::DocumentObjectGroupPython] Tb_element001  label="Tb_element : 1"  # scripted group (container) (typed FeaturePython)
  n = 1
  ref = Tb_element
FEATURE [App::DocumentObjectGroupPython] G4_Tb  # scripted group (container) (typed FeaturePython)
  Dunit = g/cm3
  Dvalue = 8.229
  Group = -> [Tb_element001]
  conduct = 2
  density = 1
  expand = 3
  formula = Tb
  name = G4_Tb
  specific = 4
FEATURE [App::DocumentObjectGroupPython] Dy_element001  label="Dy_element : 1"  # scripted group (container) (typed FeaturePython)
  n = 1
  ref = Dy_element
FEATURE [App::DocumentObjectGroupPython] G4_Dy  # scripted group (container) (typed FeaturePython)
  Dunit = g/cm3
  Dvalue = 8.55
  Group = -> [Dy_element001]
  conduct = 2
  density = 1
  expand = 3
  formula = Dy
  name = G4_Dy
  specific = 4
FEATURE [App::DocumentObjectGroupPython] Ho_element001  label="Ho_element : 1"  # scripted group (container) (typed FeaturePython)
  n = 1
  ref = Ho_element
FEATURE [App::DocumentObjectGroupPython] G4_Ho  # scripted group (container) (typed FeaturePython)
  Dunit = g/cm3
  Dvalue = 8.795
  Group = -> [Ho_element001]
  conduct = 2
  density = 1
  expand = 3
  formula = Ho
  name = G4_Ho
  specific = 4
FEATURE [App::DocumentObjectGroupPython] Er_element001  label="Er_element : 1"  # scripted group (container) (typed FeaturePython)
  n = 1
  ref = Er_element
FEATURE [App::DocumentObjectGroupPython] G4_Er  # scripted group (container) (typed FeaturePython)
  Dunit = g/cm3
  Dvalue = 9.066
  Group = -> [Er_element001]
  conduct = 2
  density = 1
  expand = 3
  formula = Er
  name = G4_Er
  specific = 4
FEATURE [App::DocumentObjectGroupPython] Tm_element001  label="Tm_element : 1"  # scripted group (container) (typed FeaturePython)
  n = 1
  ref = Tm_element
FEATURE [App::DocumentObjectGroupPython] G4_Tm  # scripted group (container) (typed FeaturePython)
  Dunit = g/cm3
  Dvalue = 9.321
  Group = -> [Tm_element001]
  conduct = 2
  density = 1
  expand = 3
  formula = Tm
  name = G4_Tm
  specific = 4
FEATURE [App::DocumentObjectGroupPython] Yb_element001  label="Yb_element : 1"  # scripted group (container) (typed FeaturePython)
  n = 1
  ref = Yb_element
FEATURE [App::DocumentObjectGroupPython] G4_Yb  # scripted group (container) (typed FeaturePython)
  Dunit = g/cm3
  Dvalue = 6.73
  Group = -> [Yb_element001]
  conduct = 2
  density = 1
  expand = 3
  formula = Yb
  name = G4_Yb
  specific = 4
FEATURE [App::DocumentObjectGroupPython] Lu_element001  label="Lu_element : 1"  # scripted group (container) (typed FeaturePython)
  n = 1
  ref = Lu_element
FEATURE [App::DocumentObjectGroupPython] G4_Lu  # scripted group (container) (typed FeaturePython)
  Dunit = g/cm3
  Dvalue = 9.84
  Group = -> [Lu_element001]
  conduct = 2
  density = 1
  expand = 3
  formula = Lu
  name = G4_Lu
  specific = 4
FEATURE [App::DocumentObjectGroupPython] Hf_element001  label="Hf_element : 1"  # scripted group (container) (typed FeaturePython)
  n = 1
  ref = Hf_element
FEATURE [App::DocumentObjectGroupPython] G4_Hf  # scripted group (container) (typed FeaturePython)
  Dunit = g/cm3
  Dvalue = 13.31
  Group = -> [Hf_element001]
  conduct = 2
  density = 1
  expand = 3
  formula = Hf
  name = G4_Hf
  specific = 4
FEATURE [App::DocumentObjectGroupPython] Ta_element001  label="Ta_element : 1"  # scripted group (container) (typed FeaturePython)
  n = 1
  ref = Ta_element
FEATURE [App::DocumentObjectGroupPython] G4_Ta  # scripted group (container) (typed FeaturePython)
  Dunit = g/cm3
  Dvalue = 16.654
  Group = -> [Ta_element001]
  conduct = 2
  density = 1
  expand = 3
  formula = Ta
  name = G4_Ta
  specific = 4
FEATURE [App::DocumentObjectGroupPython] W_element004  label="W_element : 004"  # scripted group (container) (typed FeaturePython)
  n = 1
  ref = W_element
FEATURE [App::DocumentObjectGroupPython] G4_W  # scripted group (container) (typed FeaturePython)
  Dunit = g/cm3
  Dvalue = 19.3
  Group = -> [W_element004]
  conduct = 2
  density = 1
  expand = 3
  formula = W
  name = G4_W
  specific = 4
FEATURE [App::DocumentObjectGroupPython] Re_element001  label="Re_element : 1"  # scripted group (container) (typed FeaturePython)
  n = 1
  ref = Re_element
FEATURE [App::DocumentObjectGroupPython] G4_Re  # scripted group (container) (typed FeaturePython)
  Dunit = g/cm3
  Dvalue = 21.02
  Group = -> [Re_element001]
  conduct = 2
  density = 1
  expand = 3
  formula = Re
  name = G4_Re
  specific = 4
FEATURE [App::DocumentObjectGroupPython] Os_element001  label="Os_element : 1"  # scripted group (container) (typed FeaturePython)
  n = 1
  ref = Os_element
FEATURE [App::DocumentObjectGroupPython] G4_Os  # scripted group (container) (typed FeaturePython)
  Dunit = g/cm3
  Dvalue = 22.57
  Group = -> [Os_element001]
  conduct = 2
  density = 1
  expand = 3
  formula = Os
  name = G4_Os
  specific = 4
FEATURE [App::DocumentObjectGroupPython] Ir_element001  label="Ir_element : 1"  # scripted group (container) (typed FeaturePython)
  n = 1
  ref = Ir_element
FEATURE [App::DocumentObjectGroupPython] G4_Ir  # scripted group (container) (typed FeaturePython)
  Dunit = g/cm3
  Dvalue = 22.42
  Group = -> [Ir_element001]
  conduct = 2
  density = 1
  expand = 3
  formula = Ir
  name = G4_Ir
  specific = 4
FEATURE [App::DocumentObjectGroupPython] Pt_element001  label="Pt_element : 1"  # scripted group (container) (typed FeaturePython)
  n = 1
  ref = Pt_element
FEATURE [App::DocumentObjectGroupPython] G4_Pt  # scripted group (container) (typed FeaturePython)
  Dunit = g/cm3
  Dvalue = 21.45
  Group = -> [Pt_element001]
  conduct = 2
  density = 1
  expand = 3
  formula = Pt
  name = G4_Pt
  specific = 4
FEATURE [App::DocumentObjectGroupPython] Au_element001  label="Au_element : 1"  # scripted group (container) (typed FeaturePython)
  n = 1
  ref = Au_element
FEATURE [App::DocumentObjectGroupPython] G4_Au  # scripted group (container) (typed FeaturePython)
  Dunit = g/cm3
  Dvalue = 19.32
  Group = -> [Au_element001]
  conduct = 2
  density = 1
  expand = 3
  formula = Au
  name = G4_Au
  specific = 4
FEATURE [App::DocumentObjectGroupPython] Hg_element002  label="Hg_element : 002"  # scripted group (container) (typed FeaturePython)
  n = 1
  ref = Hg_element
FEATURE [App::DocumentObjectGroupPython] G4_Hg  # scripted group (container) (typed FeaturePython)
  Dunit = g/cm3
  Dvalue = 13.546
  Group = -> [Hg_element002]
  conduct = 2
  density = 1
  expand = 3
  formula = Hg
  name = G4_Hg
  specific = 4
FEATURE [App::DocumentObjectGroupPython] Tl_element002  label="Tl_element : 002"  # scripted group (container) (typed FeaturePython)
  n = 1
  ref = Tl_element
FEATURE [App::DocumentObjectGroupPython] G4_Tl  # scripted group (container) (typed FeaturePython)
  Dunit = g/cm3
  Dvalue = 11.72
  Group = -> [Tl_element002]
  conduct = 2
  density = 1
  expand = 3
  formula = Tl
  name = G4_Tl
  specific = 4
FEATURE [App::DocumentObjectGroupPython] Pb_element003  label="Pb_element : 1"  # scripted group (container) (typed FeaturePython)
  n = 1
  ref = Pb_element
FEATURE [App::DocumentObjectGroupPython] G4_Pb  # scripted group (container) (typed FeaturePython)
  Dunit = g/cm3
  Dvalue = 11.35
  Group = -> [Pb_element003]
  conduct = 2
  density = 1
  expand = 3
  formula = Pb
  name = G4_Pb
  specific = 4
FEATURE [App::DocumentObjectGroupPython] Bi_element002  label="Bi_element : 1"  # scripted group (container) (typed FeaturePython)
  n = 1
  ref = Bi_element
FEATURE [App::DocumentObjectGroupPython] G4_Bi  # scripted group (container) (typed FeaturePython)
  Dunit = g/cm3
  Dvalue = 9.747
  Group = -> [Bi_element002]
  conduct = 2
  density = 1
  expand = 3
  formula = Bi
  name = G4_Bi
  specific = 4
FEATURE [App::DocumentObjectGroupPython] Po_element001  label="Po_element : 1"  # scripted group (container) (typed FeaturePython)
  n = 1
  ref = Po_element
FEATURE [App::DocumentObjectGroupPython] G4_Po  # scripted group (container) (typed FeaturePython)
  Dunit = g/cm3
  Dvalue = 9.32
  Group = -> [Po_element001]
  conduct = 2
  density = 1
  expand = 3
  formula = Po
  name = G4_Po
  specific = 4
FEATURE [App::DocumentObjectGroupPython] At_element001  label="At_element : 1"  # scripted group (container) (typed FeaturePython)
  n = 1
  ref = At_element
FEATURE [App::DocumentObjectGroupPython] G4_At  # scripted group (container) (typed FeaturePython)
  Dunit = g/cm3
  Dvalue = 9.32
  Group = -> [At_element001]
  conduct = 2
  density = 1
  expand = 3
  formula = At
  name = G4_At
  specific = 4
FEATURE [App::DocumentObjectGroupPython] Rn_element001  label="Rn_element : 1"  # scripted group (container) (typed FeaturePython)
  n = 1
  ref = Rn_element
FEATURE [App::DocumentObjectGroupPython] G4_Rn  # scripted group (container) (typed FeaturePython)
  Dunit = g/cm3
  Dvalue = 0.00900662
  Group = -> [Rn_element001]
  conduct = 2
  density = 1
  expand = 3
  formula = Rn
  name = G4_Rn
  specific = 4
FEATURE [App::DocumentObjectGroupPython] Fr_element001  label="Fr_element : 1"  # scripted group (container) (typed FeaturePython)
  n = 1
  ref = Fr_element
FEATURE [App::DocumentObjectGroupPython] G4_Fr  # scripted group (container) (typed FeaturePython)
  Dunit = g/cm3
  Dvalue = 1
  Group = -> [Fr_element001]
  conduct = 2
  density = 1
  expand = 3
  formula = Fr
  name = G4_Fr
  specific = 4
FEATURE [App::DocumentObjectGroupPython] Ra_element001  label="Ra_element : 1"  # scripted group (container) (typed FeaturePython)
  n = 1
  ref = Ra_element
FEATURE [App::DocumentObjectGroupPython] G4_Ra  # scripted group (container) (typed FeaturePython)
  Dunit = g/cm3
  Dvalue = 5
  Group = -> [Ra_element001]
  conduct = 2
  density = 1
  expand = 3
  formula = Ra
  name = G4_Ra
  specific = 4
FEATURE [App::DocumentObjectGroupPython] Ac_element001  label="Ac_element : 1"  # scripted group (container) (typed FeaturePython)
  n = 1
  ref = Ac_element
FEATURE [App::DocumentObjectGroupPython] G4_Ac  # scripted group (container) (typed FeaturePython)
  Dunit = g/cm3
  Dvalue = 10.07
  Group = -> [Ac_element001]
  conduct = 2
  density = 1
  expand = 3
  formula = Ac
  name = G4_Ac
  specific = 4
FEATURE [App::DocumentObjectGroupPython] Th_element001  label="Th_element : 1"  # scripted group (container) (typed FeaturePython)
  n = 1
  ref = Th_element
FEATURE [App::DocumentObjectGroupPython] G4_Th  # scripted group (container) (typed FeaturePython)
  Dunit = g/cm3
  Dvalue = 11.72
  Group = -> [Th_element001]
  conduct = 2
  density = 1
  expand = 3
  formula = Th
  name = G4_Th
  specific = 4
FEATURE [App::DocumentObjectGroupPython] Pa_element001  label="Pa_element : 1"  # scripted group (container) (typed FeaturePython)
  n = 1
  ref = Pa_element
FEATURE [App::DocumentObjectGroupPython] G4_Pa  # scripted group (container) (typed FeaturePython)
  Dunit = g/cm3
  Dvalue = 15.37
  Group = -> [Pa_element001]
  conduct = 2
  density = 1
  expand = 3
  formula = Pa
  name = G4_Pa
  specific = 4
FEATURE [App::DocumentObjectGroupPython] U_element004  label="U_element : 004"  # scripted group (container) (typed FeaturePython)
  n = 1
  ref = U_element
FEATURE [App::DocumentObjectGroupPython] G4_U  # scripted group (container) (typed FeaturePython)
  Dunit = g/cm3
  Dvalue = 18.95
  Group = -> [U_element004]
  conduct = 2
  density = 1
  expand = 3
  formula = U
  name = G4_U
  specific = 4
FEATURE [App::DocumentObjectGroupPython] Np_element001  label="Np_element : 1"  # scripted group (container) (typed FeaturePython)
  n = 1
  ref = Np_element
FEATURE [App::DocumentObjectGroupPython] G4_Np  # scripted group (container) (typed FeaturePython)
  Dunit = g/cm3
  Dvalue = 20.25
  Group = -> [Np_element001]
  conduct = 2
  density = 1
  expand = 3
  formula = Np
  name = G4_Np
  specific = 4
FEATURE [App::DocumentObjectGroupPython] Pu_element002  label="Pu_element : 002"  # scripted group (container) (typed FeaturePython)
  n = 1
  ref = Pu_element
FEATURE [App::DocumentObjectGroupPython] G4_Pu  # scripted group (container) (typed FeaturePython)
  Dunit = g/cm3
  Dvalue = 19.84
  Group = -> [Pu_element002]
  conduct = 2
  density = 1
  expand = 3
  formula = Pu
  name = G4_Pu
  specific = 4
FEATURE [App::DocumentObjectGroupPython] Am_element001  label="Am_element : 1"  # scripted group (container) (typed FeaturePython)
  n = 1
  ref = Am_element
FEATURE [App::DocumentObjectGroupPython] G4_Am  # scripted group (container) (typed FeaturePython)
  Dunit = g/cm3
  Dvalue = 13.67
  Group = -> [Am_element001]
  conduct = 2
  density = 1
  expand = 3
  formula = Am
  name = G4_Am
  specific = 4
FEATURE [App::DocumentObjectGroupPython] Cm_element001  label="Cm_element : 1"  # scripted group (container) (typed FeaturePython)
  n = 1
  ref = Cm_element
FEATURE [App::DocumentObjectGroupPython] G4_Cm  # scripted group (container) (typed FeaturePython)
  Dunit = g/cm3
  Dvalue = 13.51
  Group = -> [Cm_element001]
  conduct = 2
  density = 1
  expand = 3
  formula = Cm
  name = G4_Cm
  specific = 4
FEATURE [App::DocumentObjectGroupPython] Bk_element001  label="Bk_element : 1"  # scripted group (container) (typed FeaturePython)
  n = 1
  ref = Bk_element
FEATURE [App::DocumentObjectGroupPython] G4_Bk  # scripted group (container) (typed FeaturePython)
  Dunit = g/cm3
  Dvalue = 14
  Group = -> [Bk_element001]
  conduct = 2
  density = 1
  expand = 3
  formula = Bk
  name = G4_Bk
  specific = 4
FEATURE [App::DocumentObjectGroupPython] Cf_element001  label="Cf_element : 1"  # scripted group (container) (typed FeaturePython)
  n = 1
  ref = Cf_element
FEATURE [App::DocumentObjectGroupPython] G4_Cf  # scripted group (container) (typed FeaturePython)
  Dunit = g/cm3
  Dvalue = 10
  Group = -> [Cf_element001]
  conduct = 2
  density = 1
  expand = 3
  formula = Cf
  name = G4_Cf
  specific = 4
FEATURE [App::DocumentObjectGroupPython] Element  # scripted group (container) (typed FeaturePython)
  Group = -> [G4_H,G4_He,G4_Li,G4_Be,G4_B,G4_C,G4_N,G4_O,G4_F,G4_Ne,G4_Na,G4_Mg,G4_Al,G4_Si,G4_P,G4_S,G4_Cl,G4_Ar,G4_K,G4_Ca,G4_Sc,G4_Ti,G4_V,G4_Cr,G4_Mn,G4_Fe,G4_Co,G4_Ni,G4_Cu,G4_Zn,G4_Ga,G4_Ge,G4_As,G4_Se,G4_Br,G4_Kr,G4_Rb,G4_Sr,G4_Y,G4_Zr,G4_Nb,G4_Mo,G4_Tc,G4_Ru,G4_Rh,G4_Pd,G4_Ag,G4_Cd,G4_In,G4_Sn,G4_Sb,G4_Te,G4_I,G4_Xe,G4_Cs,G4_Ba,G4_La,G4_Ce,G4_Pr,G4_Nd,G4_Pm,G4_Sm,G4_Eu,G4_Gd,G4_Tb,G4_Dy,G4_Ho,G4_Er,+30 more]
FEATURE [App::DocumentObjectGroupPython] H_element114  label="H_element : 063"  # scripted group (container) (typed FeaturePython)
  n = 2
  ref = H_element
FEATURE [App::DocumentObjectGroupPython] G4_lH2  # scripted group (container) (typed FeaturePython)
  Dunit = g/cm3
  Dvalue = 0.0708
  Group = -> [H_element114]
  conduct = 2
  density = 1
  expand = 3
  formula = G4_lH2
  name = G4_lH2
  specific = 4
FEATURE [App::DocumentObjectGroupPython] N_element049  label="N_element : 022"  # scripted group (container) (typed FeaturePython)
  n = 2
  ref = N_element
FEATURE [App::DocumentObjectGroupPython] G4_lN2  # scripted group (container) (typed FeaturePython)
  Dunit = g/cm3
  Dvalue = 0.807
  Group = -> [N_element049]
  conduct = 2
  density = 1
  expand = 3
  formula = G4_lN2
  name = G4_lN2
  specific = 4
FEATURE [App::DocumentObjectGroupPython] O_element106  label="O_element : 060"  # scripted group (container) (typed FeaturePython)
  n = 2
  ref = O_element
FEATURE [App::DocumentObjectGroupPython] G4_lO2  # scripted group (container) (typed FeaturePython)
  Dunit = g/cm3
  Dvalue = 1.141
  Group = -> [O_element106]
  conduct = 2
  density = 1
  expand = 3
  formula = G4_lO2
  name = G4_lO2
  specific = 4
FEATURE [App::DocumentObjectGroupPython] Ar  label="Ar : 1"  # scripted group (container) (typed FeaturePython)
  n = 1
  ref = Ar
FEATURE [App::DocumentObjectGroupPython] G4_lAr  # scripted group (container) (typed FeaturePython)
  Dunit = g/cm3
  Dvalue = 1.396
  Group = -> [Ar]
  conduct = 2
  density = 1
  expand = 3
  formula = G4_lAr
  name = G4_lAr
  specific = 4
FEATURE [App::DocumentObjectGroupPython] Br  label="Br : 1"  # scripted group (container) (typed FeaturePython)
  n = 1
  ref = Br
FEATURE [App::DocumentObjectGroupPython] G4_lBr  # scripted group (container) (typed FeaturePython)
  Dunit = g/cm3
  Dvalue = 3.1028
  Group = -> [Br]
  conduct = 2
  density = 1
  expand = 3
  formula = G4_lBr
  name = G4_lBr
  specific = 4
FEATURE [App::DocumentObjectGroupPython] Kr  label="Kr : 1"  # scripted group (container) (typed FeaturePython)
  n = 1
  ref = Kr
FEATURE [App::DocumentObjectGroupPython] G4_lKr  # scripted group (container) (typed FeaturePython)
  Dunit = g/cm3
  Dvalue = 2.418
  Group = -> [Kr]
  conduct = 2
  density = 1
  expand = 3
  formula = G4_lKr
  name = G4_lKr
  specific = 4
FEATURE [App::DocumentObjectGroupPython] Xe  label="Xe : 1"  # scripted group (container) (typed FeaturePython)
  n = 1
  ref = Xe
FEATURE [App::DocumentObjectGroupPython] G4_lXe  # scripted group (container) (typed FeaturePython)
  Dunit = g/cm3
  Dvalue = 2.953
  Group = -> [Xe]
  conduct = 2
  density = 1
  expand = 3
  formula = G4_lXe
  name = G4_lXe
  specific = 4
FEATURE [App::DocumentObjectGroupPython] O_element107  label="O_element : 061"  # scripted group (container) (typed FeaturePython)
  n = 4
  ref = O_element
FEATURE [App::DocumentObjectGroupPython] Pb_element004  label="Pb_element : 002"  # scripted group (container) (typed FeaturePython)
  n = 1
  ref = Pb_element
FEATURE [App::DocumentObjectGroupPython] W_element005  label="W_element : 005"  # scripted group (container) (typed FeaturePython)
  n = 1
  ref = W_element
FEATURE [App::DocumentObjectGroupPython] G4_PbWO4  # scripted group (container) (typed FeaturePython)
  Dunit = g/cm3
  Dvalue = 8.28
  Group = -> [O_element107,Pb_element004,W_element005]
  conduct = 2
  density = 1
  expand = 3
  formula = G4_PbWO4
  name = G4_PbWO4
  specific = 4
FEATURE [App::DocumentObjectGroupPython] alactic  label="alactic : 1"  # scripted group (container) (typed FeaturePython)
  n = 1
  ref = alactic
FEATURE [App::DocumentObjectGroupPython] G4_Galactic  # scripted group (container) (typed FeaturePython)
  Dunit = g/cm3
  Dvalue = 0
  Group = -> [alactic]
  conduct = 2
  density = 1
  expand = 3
  formula = G4_Galactic
  name = G4_Galactic
  specific = 4
FEATURE [App::DocumentObjectGroupPython] RAPHITE_POROUS  label="RAPHITE_POROUS : 1"  # scripted group (container) (typed FeaturePython)
  n = 1
  ref = RAPHITE_POROUS
FEATURE [App::DocumentObjectGroupPython] G4_GRAPHITE_POROUS  # scripted group (container) (typed FeaturePython)
  Dunit = g/cm3
  Dvalue = 1.7
  Group = -> [RAPHITE_POROUS]
  conduct = 2
  density = 1
  expand = 3
  formula = G4_GRAPHITE_POROUS
  name = G4_GRAPHITE_POROUS
  specific = 4
FEATURE [App::DocumentObjectGroupPython] H_element115  label="H_element : 0.150"  # scripted group (container) (typed FeaturePython)
  n = 0.080538
FEATURE [App::DocumentObjectGroupPython] C_element125  label="C_element : 0.600"  # scripted group (container) (typed FeaturePython)
  n = 0.599848
FEATURE [App::DocumentObjectGroupPython] O_element108  label="O_element : 0.320"  # scripted group (container) (typed FeaturePython)
  n = 0.319614
FEATURE [App::DocumentObjectGroupPython] G4_LUCITE  # scripted group (container) (typed FeaturePython)
  Dunit = g/cm3
  Dvalue = 1.19
  Group = -> [H_element115,C_element125,O_element108]
  conduct = 2
  density = 1
  expand = 3
  formula = G4_LUCITE
  name = G4_LUCITE
  specific = 4
FEATURE [App::DocumentObjectGroupPython] Cu_element002  label="Cu_element : 62"  # scripted group (container) (typed FeaturePython)
  n = 62
  ref = Cu_element
FEATURE [App::DocumentObjectGroupPython] Zn_element002  label="Zn_element : 35"  # scripted group (container) (typed FeaturePython)
  n = 35
  ref = Zn_element
FEATURE [App::DocumentObjectGroupPython] Pb_element005  label="Pb_element : 3"  # scripted group (container) (typed FeaturePython)
  n = 3
  ref = Pb_element
FEATURE [App::DocumentObjectGroupPython] G4_BRASS  # scripted group (container) (typed FeaturePython)
  Dunit = g/cm3
  Dvalue = 8.52
  Group = -> [Cu_element002,Zn_element002,Pb_element005]
  conduct = 2
  density = 1
  expand = 3
  formula = G4_BRASS
  name = G4_BRASS
  specific = 4
FEATURE [App::DocumentObjectGroupPython] Cu_element003  label="Cu_element : 89"  # scripted group (container) (typed FeaturePython)
  n = 89
  ref = Cu_element
FEATURE [App::DocumentObjectGroupPython] Zn_element003  label="Zn_element : 9"  # scripted group (container) (typed FeaturePython)
  n = 9
  ref = Zn_element
FEATURE [App::DocumentObjectGroupPython] Pb_element006  label="Pb_element : 2"  # scripted group (container) (typed FeaturePython)
  n = 2
  ref = Pb_element
FEATURE [App::DocumentObjectGroupPython] G4_BRONZE  # scripted group (container) (typed FeaturePython)
  Dunit = g/cm3
  Dvalue = 8.82
  Group = -> [Cu_element003,Zn_element003,Pb_element006]
  conduct = 2
  density = 1
  expand = 3
  formula = G4_BRONZE
  name = G4_BRONZE
  specific = 4
FEATURE [App::DocumentObjectGroupPython] Fe_element008  label="Fe_element : 74"  # scripted group (container) (typed FeaturePython)
  n = 74
  ref = Fe_element
FEATURE [App::DocumentObjectGroupPython] Cr_element002  label="Cr_element : 18"  # scripted group (container) (typed FeaturePython)
  n = 18
  ref = Cr_element
FEATURE [App::DocumentObjectGroupPython] Ni_element002  label="Ni_element : 8"  # scripted group (container) (typed FeaturePython)
  n = 8
  ref = Ni_element
FEATURE [App::DocumentObjectGroupPython] G4_STAINLESS_STEEL  label="G4_STAINLESS-STEEL"  # scripted group (container) (typed FeaturePython)
  Dunit = g/cm3
  Dvalue = 8
  Group = -> [Fe_element008,Cr_element002,Ni_element002]
  conduct = 2
  density = 1
  expand = 3
  formula = G4_STAINLESS-STEEL
  name = G4_STAINLESS-STEEL
  specific = 4
FEATURE [App::DocumentObjectGroupPython] H_element116  label="H_element : 064"  # scripted group (container) (typed FeaturePython)
  n = 18
  ref = H_element
FEATURE [App::DocumentObjectGroupPython] C_element126  label="C_element : 071"  # scripted group (container) (typed FeaturePython)
  n = 12
  ref = C_element
FEATURE [App::DocumentObjectGroupPython] O_element109  label="O_element : 062"  # scripted group (container) (typed FeaturePython)
  n = 7
  ref = O_element
FEATURE [App::DocumentObjectGroupPython] G4_CR39  # scripted group (container) (typed FeaturePython)
  Dunit = g/cm3
  Dvalue = 1.32
  Group = -> [H_element116,C_element126,O_element109]
  conduct = 2
  density = 1
  expand = 3
  formula = G4_CR39
  name = G4_CR39
  specific = 4
FEATURE [App::DocumentObjectGroupPython] H_element117  label="H_element : 38"  # scripted group (container) (typed FeaturePython)
  n = 38
  ref = H_element
FEATURE [App::DocumentObjectGroupPython] C_element127  label="C_element : 072"  # scripted group (container) (typed FeaturePython)
  n = 18
  ref = C_element
FEATURE [App::DocumentObjectGroupPython] O_element110  label="O_element : 063"  # scripted group (container) (typed FeaturePython)
  n = 1
  ref = O_element
FEATURE [App::DocumentObjectGroupPython] G4_OCTADECANOL  # scripted group (container) (typed FeaturePython)
  Dunit = g/cm3
  Dvalue = 0.812
  Group = -> [H_element117,C_element127,O_element110]
  conduct = 2
  density = 1
  expand = 3
  formula = G4_OCTADECANOL
  name = G4_OCTADECANOL
  specific = 4
FEATURE [App::DocumentObjectGroupPython] HEP  # scripted group (container) (typed FeaturePython)
  Group = -> [G4_lH2,G4_lN2,G4_lO2,G4_lAr,G4_lBr,G4_lKr,G4_lXe,G4_PbWO4,G4_Galactic,G4_GRAPHITE_POROUS,G4_LUCITE,G4_BRASS,G4_BRONZE,G4_STAINLESS_STEEL,G4_CR39,G4_OCTADECANOL]
FEATURE [App::DocumentObjectGroupPython] C_element128  label="C_element : 073"  # scripted group (container) (typed FeaturePython)
  n = 14
  ref = C_element
FEATURE [App::DocumentObjectGroupPython] H_element118  label="H_element : 065"  # scripted group (container) (typed FeaturePython)
  n = 10
  ref = H_element
FEATURE [App::DocumentObjectGroupPython] O_element111  label="O_element : 064"  # scripted group (container) (typed FeaturePython)
  n = 2
  ref = O_element
FEATURE [App::DocumentObjectGroupPython] N_element050  label="N_element : 023"  # scripted group (container) (typed FeaturePython)
  n = 2
  ref = N_element
FEATURE [App::DocumentObjectGroupPython] G4_KEVLAR  # scripted group (container) (typed FeaturePython)
  Dunit = g/cm3
  Dvalue = 1.44
  Group = -> [C_element128,H_element118,O_element111,N_element050]
  conduct = 2
  density = 1
  expand = 3
  formula = G4_KEVLAR
  name = G4_KEVLAR
  specific = 4
FEATURE [App::DocumentObjectGroupPython] C_element129  label="C_element : 074"  # scripted group (container) (typed FeaturePython)
  n = 10
  ref = C_element
FEATURE [App::DocumentObjectGroupPython] H_element119  label="H_element : 066"  # scripted group (container) (typed FeaturePython)
  n = 8
  ref = H_element
FEATURE [App::DocumentObjectGroupPython] O_element112  label="O_element : 065"  # scripted group (container) (typed FeaturePython)
  n = 4
  ref = O_element
FEATURE [App::DocumentObjectGroupPython] G4_DACRON  # scripted group (container) (typed FeaturePython)
  Dunit = g/cm3
  Dvalue = 1.4
  Group = -> [C_element129,H_element119,O_element112]
  conduct = 2
  density = 1
  expand = 3
  formula = G4_DACRON
  name = G4_DACRON
  specific = 4
FEATURE [App::DocumentObjectGroupPython] C_element130  label="C_element : 075"  # scripted group (container) (typed FeaturePython)
  n = 4
  ref = C_element
FEATURE [App::DocumentObjectGroupPython] H_element120  label="H_element : 067"  # scripted group (container) (typed FeaturePython)
  n = 5
  ref = H_element
FEATURE [App::DocumentObjectGroupPython] Cl_element030  label="Cl_element : 016"  # scripted group (container) (typed FeaturePython)
  n = 1
  ref = Cl_element
FEATURE [App::DocumentObjectGroupPython] G4_NEOPRENE  # scripted group (container) (typed FeaturePython)
  Dunit = g/cm3
  Dvalue = 1.23
  Group = -> [C_element130,H_element120,Cl_element030]
  conduct = 2
  density = 1
  expand = 3
  formula = G4_NEOPRENE
  name = G4_NEOPRENE
  specific = 4
FEATURE [App::DocumentObjectGroupPython] Space  # scripted group (container) (typed FeaturePython)
  Group = -> [G4_KEVLAR,G4_DACRON,G4_NEOPRENE]
FEATURE [App::DocumentObjectGroupPython] H_element121  label="H_element : 068"  # scripted group (container) (typed FeaturePython)
  n = 5
  ref = H_element
FEATURE [App::DocumentObjectGroupPython] C_element131  label="C_element : 076"  # scripted group (container) (typed FeaturePython)
  n = 4
  ref = C_element
FEATURE [App::DocumentObjectGroupPython] N_element051  label="N_element : 3"  # scripted group (container) (typed FeaturePython)
  n = 3
  ref = N_element
FEATURE [App::DocumentObjectGroupPython] O_element113  label="O_element : 066"  # scripted group (container) (typed FeaturePython)
  n = 1
  ref = O_element
FEATURE [App::DocumentObjectGroupPython] G4_CYTOSINE  # scripted group (container) (typed FeaturePython)
  Dunit = g/cm3
  Dvalue = 1.55
  Group = -> [H_element121,C_element131,N_element051,O_element113]
  conduct = 2
  density = 1
  expand = 3
  formula = G4_CYTOSINE
  name = G4_CYTOSINE
  specific = 4
FEATURE [App::DocumentObjectGroupPython] H_element122  label="H_element : 069"  # scripted group (container) (typed FeaturePython)
  n = 6
  ref = H_element
FEATURE [App::DocumentObjectGroupPython] C_element132  label="C_element : 077"  # scripted group (container) (typed FeaturePython)
  n = 5
  ref = C_element
FEATURE [App::DocumentObjectGroupPython] N_element052  label="N_element : 024"  # scripted group (container) (typed FeaturePython)
  n = 2
  ref = N_element
FEATURE [App::DocumentObjectGroupPython] O_element114  label="O_element : 067"  # scripted group (container) (typed FeaturePython)
  n = 2
  ref = O_element
FEATURE [App::DocumentObjectGroupPython] G4_THYMINE  # scripted group (container) (typed FeaturePython)
  Dunit = g/cm3
  Dvalue = 1.23
  Group = -> [H_element122,C_element132,N_element052,O_element114]
  conduct = 2
  density = 1
  expand = 3
  formula = G4_THYMINE
  name = G4_THYMINE
  specific = 4
FEATURE [App::DocumentObjectGroupPython] H_element123  label="H_element : 070"  # scripted group (container) (typed FeaturePython)
  n = 4
  ref = H_element
FEATURE [App::DocumentObjectGroupPython] C_element133  label="C_element : 078"  # scripted group (container) (typed FeaturePython)
  n = 4
  ref = C_element
FEATURE [App::DocumentObjectGroupPython] N_element053  label="N_element : 025"  # scripted group (container) (typed FeaturePython)
  n = 2
  ref = N_element
FEATURE [App::DocumentObjectGroupPython] O_element115  label="O_element : 068"  # scripted group (container) (typed FeaturePython)
  n = 2
  ref = O_element
FEATURE [App::DocumentObjectGroupPython] G4_URACIL  # scripted group (container) (typed FeaturePython)
  Dunit = g/cm3
  Dvalue = 1.32
  Group = -> [H_element123,C_element133,N_element053,O_element115]
  conduct = 2
  density = 1
  expand = 3
  formula = G4_URACIL
  name = G4_URACIL
  specific = 4
FEATURE [App::DocumentObjectGroupPython] H_element124  label="H_element : 071"  # scripted group (container) (typed FeaturePython)
  n = 4
  ref = H_element
FEATURE [App::DocumentObjectGroupPython] C_element134  label="C_element : 079"  # scripted group (container) (typed FeaturePython)
  n = 5
  ref = C_element
FEATURE [App::DocumentObjectGroupPython] N_element054  label="N_element : 026"  # scripted group (container) (typed FeaturePython)
  n = 5
  ref = N_element
FEATURE [App::DocumentObjectGroupPython] G4_DNA_ADENINE  # scripted group (container) (typed FeaturePython)
  Dunit = g/cm3
  Dvalue = 1
  Group = -> [H_element124,C_element134,N_element054]
  conduct = 2
  density = 1
  expand = 3
  formula = G4_DNA_ADENINE
  name = G4_DNA_ADENINE
  specific = 4
FEATURE [App::DocumentObjectGroupPython] H_element125  label="H_element : 072"  # scripted group (container) (typed FeaturePython)
  n = 4
  ref = H_element
FEATURE [App::DocumentObjectGroupPython] C_element135  label="C_element : 080"  # scripted group (container) (typed FeaturePython)
  n = 5
  ref = C_element
FEATURE [App::DocumentObjectGroupPython] N_element055  label="N_element : 027"  # scripted group (container) (typed FeaturePython)
  n = 5
  ref = N_element
FEATURE [App::DocumentObjectGroupPython] O_element116  label="O_element : 069"  # scripted group (container) (typed FeaturePython)
  n = 1
  ref = O_element
FEATURE [App::DocumentObjectGroupPython] G4_DNA_GUANINE  # scripted group (container) (typed FeaturePython)
  Dunit = g/cm3
  Dvalue = 1
  Group = -> [H_element125,C_element135,N_element055,O_element116]
  conduct = 2
  density = 1
  expand = 3
  formula = G4_DNA_GUANINE
  name = G4_DNA_GUANINE
  specific = 4
FEATURE [App::DocumentObjectGroupPython] H_element126  label="H_element : 073"  # scripted group (container) (typed FeaturePython)
  n = 4
  ref = H_element
FEATURE [App::DocumentObjectGroupPython] C_element136  label="C_element : 081"  # scripted group (container) (typed FeaturePython)
  n = 4
  ref = C_element
FEATURE [App::DocumentObjectGroupPython] N_element056  label="N_element : 028"  # scripted group (container) (typed FeaturePython)
  n = 3
  ref = N_element
FEATURE [App::DocumentObjectGroupPython] O_element117  label="O_element : 070"  # scripted group (container) (typed FeaturePython)
  n = 1
  ref = O_element
FEATURE [App::DocumentObjectGroupPython] G4_DNA_CYTOSINE  # scripted group (container) (typed FeaturePython)
  Dunit = g/cm3
  Dvalue = 1
  Group = -> [H_element126,C_element136,N_element056,O_element117]
  conduct = 2
  density = 1
  expand = 3
  formula = G4_DNA_CYTOSINE
  name = G4_DNA_CYTOSINE
  specific = 4
FEATURE [App::DocumentObjectGroupPython] H_element127  label="H_element : 074"  # scripted group (container) (typed FeaturePython)
  n = 5
  ref = H_element
FEATURE [App::DocumentObjectGroupPython] C_element137  label="C_element : 082"  # scripted group (container) (typed FeaturePython)
  n = 5
  ref = C_element
FEATURE [App::DocumentObjectGroupPython] N_element057  label="N_element : 029"  # scripted group (container) (typed FeaturePython)
  n = 2
  ref = N_element
FEATURE [App::DocumentObjectGroupPython] O_element118  label="O_element : 071"  # scripted group (container) (typed FeaturePython)
  n = 2
  ref = O_element
FEATURE [App::DocumentObjectGroupPython] G4_DNA_THYMINE  # scripted group (container) (typed FeaturePython)
  Dunit = g/cm3
  Dvalue = 1
  Group = -> [H_element127,C_element137,N_element057,O_element118]
  conduct = 2
  density = 1
  expand = 3
  formula = G4_DNA_THYMINE
  name = G4_DNA_THYMINE
  specific = 4
FEATURE [App::DocumentObjectGroupPython] H_element128  label="H_element : 075"  # scripted group (container) (typed FeaturePython)
  n = 3
  ref = H_element
FEATURE [App::DocumentObjectGroupPython] C_element138  label="C_element : 083"  # scripted group (container) (typed FeaturePython)
  n = 4
  ref = C_element
FEATURE [App::DocumentObjectGroupPython] N_element058  label="N_element : 030"  # scripted group (container) (typed FeaturePython)
  n = 2
  ref = N_element
FEATURE [App::DocumentObjectGroupPython] O_element119  label="O_element : 072"  # scripted group (container) (typed FeaturePython)
  n = 2
  ref = O_element
FEATURE [App::DocumentObjectGroupPython] G4_DNA_URACIL  # scripted group (container) (typed FeaturePython)
  Dunit = g/cm3
  Dvalue = 1
  Group = -> [H_element128,C_element138,N_element058,O_element119]
  conduct = 2
  density = 1
  expand = 3
  formula = G4_DNA_URACIL
  name = G4_DNA_URACIL
  specific = 4
FEATURE [App::DocumentObjectGroupPython] H_element129  label="H_element : 076"  # scripted group (container) (typed FeaturePython)
  n = 10
  ref = H_element
FEATURE [App::DocumentObjectGroupPython] C_element139  label="C_element : 084"  # scripted group (container) (typed FeaturePython)
  n = 10
  ref = C_element
FEATURE [App::DocumentObjectGroupPython] N_element059  label="N_element : 031"  # scripted group (container) (typed FeaturePython)
  n = 5
  ref = N_element
FEATURE [App::DocumentObjectGroupPython] O_element120  label="O_element : 073"  # scripted group (container) (typed FeaturePython)
  n = 4
  ref = O_element
FEATURE [App::DocumentObjectGroupPython] G4_DNA_ADENOSINE  # scripted group (container) (typed FeaturePython)
  Dunit = g/cm3
  Dvalue = 1
  Group = -> [H_element129,C_element139,N_element059,O_element120]
  conduct = 2
  density = 1
  expand = 3
  formula = G4_DNA_ADENOSINE
  name = G4_DNA_ADENOSINE
  specific = 4
FEATURE [App::DocumentObjectGroupPython] H_element130  label="H_element : 077"  # scripted group (container) (typed FeaturePython)
  n = 10
  ref = H_element
FEATURE [App::DocumentObjectGroupPython] C_element140  label="C_element : 085"  # scripted group (container) (typed FeaturePython)
  n = 10
  ref = C_element
FEATURE [App::DocumentObjectGroupPython] N_element060  label="N_element : 032"  # scripted group (container) (typed FeaturePython)
  n = 5
  ref = N_element
FEATURE [App::DocumentObjectGroupPython] O_element121  label="O_element : 074"  # scripted group (container) (typed FeaturePython)
  n = 5
  ref = O_element
FEATURE [App::DocumentObjectGroupPython] G4_DNA_GUANOSINE  # scripted group (container) (typed FeaturePython)
  Dunit = g/cm3
  Dvalue = 1
  Group = -> [H_element130,C_element140,N_element060,O_element121]
  conduct = 2
  density = 1
  expand = 3
  formula = G4_DNA_GUANOSINE
  name = G4_DNA_GUANOSINE
  specific = 4
FEATURE [App::DocumentObjectGroupPython] H_element131  label="H_element : 078"  # scripted group (container) (typed FeaturePython)
  n = 10
  ref = H_element
FEATURE [App::DocumentObjectGroupPython] C_element141  label="C_element : 086"  # scripted group (container) (typed FeaturePython)
  n = 9
  ref = C_element
FEATURE [App::DocumentObjectGroupPython] N_element061  label="N_element : 033"  # scripted group (container) (typed FeaturePython)
  n = 3
  ref = N_element
FEATURE [App::DocumentObjectGroupPython] O_element122  label="O_element : 075"  # scripted group (container) (typed FeaturePython)
  n = 5
  ref = O_element
FEATURE [App::DocumentObjectGroupPython] G4_DNA_CYTIDINE  # scripted group (container) (typed FeaturePython)
  Dunit = g/cm3
  Dvalue = 1
  Group = -> [H_element131,C_element141,N_element061,O_element122]
  conduct = 2
  density = 1
  expand = 3
  formula = G4_DNA_CYTIDINE
  name = G4_DNA_CYTIDINE
  specific = 4
FEATURE [App::DocumentObjectGroupPython] H_element132  label="H_element : 079"  # scripted group (container) (typed FeaturePython)
  n = 9
  ref = H_element
FEATURE [App::DocumentObjectGroupPython] C_element142  label="C_element : 087"  # scripted group (container) (typed FeaturePython)
  n = 9
  ref = C_element
FEATURE [App::DocumentObjectGroupPython] N_element062  label="N_element : 034"  # scripted group (container) (typed FeaturePython)
  n = 2
  ref = N_element
FEATURE [App::DocumentObjectGroupPython] O_element123  label="O_element : 076"  # scripted group (container) (typed FeaturePython)
  n = 6
  ref = O_element
FEATURE [App::DocumentObjectGroupPython] G4_DNA_URIDINE  # scripted group (container) (typed FeaturePython)
  Dunit = g/cm3
  Dvalue = 1
  Group = -> [H_element132,C_element142,N_element062,O_element123]
  conduct = 2
  density = 1
  expand = 3
  formula = G4_DNA_URIDINE
  name = G4_DNA_URIDINE
  specific = 4
FEATURE [App::DocumentObjectGroupPython] H_element133  label="H_element : 080"  # scripted group (container) (typed FeaturePython)
  n = 11
  ref = H_element
FEATURE [App::DocumentObjectGroupPython] C_element143  label="C_element : 088"  # scripted group (container) (typed FeaturePython)
  n = 10
  ref = C_element
FEATURE [App::DocumentObjectGroupPython] N_element063  label="N_element : 035"  # scripted group (container) (typed FeaturePython)
  n = 2
  ref = N_element
FEATURE [App::DocumentObjectGroupPython] O_element124  label="O_element : 077"  # scripted group (container) (typed FeaturePython)
  n = 6
  ref = O_element
FEATURE [App::DocumentObjectGroupPython] G4_DNA_METHYLURIDINE  # scripted group (container) (typed FeaturePython)
  Dunit = g/cm3
  Dvalue = 1
  Group = -> [H_element133,C_element143,N_element063,O_element124]
  conduct = 2
  density = 1
  expand = 3
  formula = G4_DNA_METHYLURIDINE
  name = G4_DNA_METHYLURIDINE
  specific = 4
FEATURE [App::DocumentObjectGroupPython] P_element014  label="P_element : 003"  # scripted group (container) (typed FeaturePython)
  n = 1
  ref = P_element
FEATURE [App::DocumentObjectGroupPython] O_element125  label="O_element : 078"  # scripted group (container) (typed FeaturePython)
  n = 3
  ref = O_element
FEATURE [App::DocumentObjectGroupPython] G4_DNA_MONOPHOSPHATE  # scripted group (container) (typed FeaturePython)
  Dunit = g/cm3
  Dvalue = 1
  Group = -> [P_element014,O_element125]
  conduct = 2
  density = 1
  expand = 3
  formula = G4_DNA_MONOPHOSPHATE
  name = G4_DNA_MONOPHOSPHATE
  specific = 4
FEATURE [App::DocumentObjectGroupPython] H_element134  label="H_element : 081"  # scripted group (container) (typed FeaturePython)
  n = 10
  ref = H_element
FEATURE [App::DocumentObjectGroupPython] C_element144  label="C_element : 089"  # scripted group (container) (typed FeaturePython)
  n = 10
  ref = C_element
FEATURE [App::DocumentObjectGroupPython] N_element064  label="N_element : 036"  # scripted group (container) (typed FeaturePython)
  n = 5
  ref = N_element
FEATURE [App::DocumentObjectGroupPython] O_element126  label="O_element : 079"  # scripted group (container) (typed FeaturePython)
  n = 7
  ref = O_element
FEATURE [App::DocumentObjectGroupPython] P_element015  label="P_element : 004"  # scripted group (container) (typed FeaturePython)
  n = 1
  ref = P_element
FEATURE [App::DocumentObjectGroupPython] G4_DNA_A  # scripted group (container) (typed FeaturePython)
  Dunit = g/cm3
  Dvalue = 1
  Group = -> [H_element134,C_element144,N_element064,O_element126,P_element015]
  conduct = 2
  density = 1
  expand = 3
  formula = G4_DNA_A
  name = G4_DNA_A
  specific = 4
FEATURE [App::DocumentObjectGroupPython] H_element135  label="H_element : 082"  # scripted group (container) (typed FeaturePython)
  n = 10
  ref = H_element
FEATURE [App::DocumentObjectGroupPython] C_element145  label="C_element : 090"  # scripted group (container) (typed FeaturePython)
  n = 10
  ref = C_element
FEATURE [App::DocumentObjectGroupPython] N_element065  label="N_element : 037"  # scripted group (container) (typed FeaturePython)
  n = 5
  ref = N_element
FEATURE [App::DocumentObjectGroupPython] O_element127  label="O_element : 8"  # scripted group (container) (typed FeaturePython)
  n = 8
  ref = O_element
FEATURE [App::DocumentObjectGroupPython] P_element016  label="P_element : 005"  # scripted group (container) (typed FeaturePython)
  n = 1
  ref = P_element
FEATURE [App::DocumentObjectGroupPython] G4_DNA_G  # scripted group (container) (typed FeaturePython)
  Dunit = g/cm3
  Dvalue = 1
  Group = -> [H_element135,C_element145,N_element065,O_element127,P_element016]
  conduct = 2
  density = 1
  expand = 3
  formula = G4_DNA_G
  name = G4_DNA_G
  specific = 4
FEATURE [App::DocumentObjectGroupPython] H_element136  label="H_element : 083"  # scripted group (container) (typed FeaturePython)
  n = 10
  ref = H_element
FEATURE [App::DocumentObjectGroupPython] C_element146  label="C_element : 091"  # scripted group (container) (typed FeaturePython)
  n = 9
  ref = C_element
FEATURE [App::DocumentObjectGroupPython] N_element066  label="N_element : 038"  # scripted group (container) (typed FeaturePython)
  n = 3
  ref = N_element
FEATURE [App::DocumentObjectGroupPython] O_element128  label="O_element : 080"  # scripted group (container) (typed FeaturePython)
  n = 8
  ref = O_element
FEATURE [App::DocumentObjectGroupPython] P_element017  label="P_element : 006"  # scripted group (container) (typed FeaturePython)
  n = 1
  ref = P_element
FEATURE [App::DocumentObjectGroupPython] G4_DNA_C  # scripted group (container) (typed FeaturePython)
  Dunit = g/cm3
  Dvalue = 1
  Group = -> [H_element136,C_element146,N_element066,O_element128,P_element017]
  conduct = 2
  density = 1
  expand = 3
  formula = G4_DNA_C
  name = G4_DNA_C
  specific = 4
FEATURE [App::DocumentObjectGroupPython] H_element137  label="H_element : 084"  # scripted group (container) (typed FeaturePython)
  n = 9
  ref = H_element
FEATURE [App::DocumentObjectGroupPython] C_element147  label="C_element : 092"  # scripted group (container) (typed FeaturePython)
  n = 9
  ref = C_element
FEATURE [App::DocumentObjectGroupPython] N_element067  label="N_element : 039"  # scripted group (container) (typed FeaturePython)
  n = 2
  ref = N_element
FEATURE [App::DocumentObjectGroupPython] O_element129  label="O_element : 9"  # scripted group (container) (typed FeaturePython)
  n = 9
  ref = O_element
FEATURE [App::DocumentObjectGroupPython] P_element018  label="P_element : 007"  # scripted group (container) (typed FeaturePython)
  n = 1
  ref = P_element
FEATURE [App::DocumentObjectGroupPython] G4_DNA_U  # scripted group (container) (typed FeaturePython)
  Dunit = g/cm3
  Dvalue = 1
  Group = -> [H_element137,C_element147,N_element067,O_element129,P_element018]
  conduct = 2
  density = 1
  expand = 3
  formula = G4_DNA_U
  name = G4_DNA_U
  specific = 4
FEATURE [App::DocumentObjectGroupPython] H_element138  label="H_element : 085"  # scripted group (container) (typed FeaturePython)
  n = 11
  ref = H_element
FEATURE [App::DocumentObjectGroupPython] C_element148  label="C_element : 093"  # scripted group (container) (typed FeaturePython)
  n = 10
  ref = C_element
FEATURE [App::DocumentObjectGroupPython] N_element068  label="N_element : 040"  # scripted group (container) (typed FeaturePython)
  n = 2
  ref = N_element
FEATURE [App::DocumentObjectGroupPython] O_element130  label="O_element : 081"  # scripted group (container) (typed FeaturePython)
  n = 9
  ref = O_element
FEATURE [App::DocumentObjectGroupPython] P_element019  label="P_element : 008"  # scripted group (container) (typed FeaturePython)
  n = 1
  ref = P_element
FEATURE [App::DocumentObjectGroupPython] G4_DNA_MU  # scripted group (container) (typed FeaturePython)
  Dunit = g/cm3
  Dvalue = 1
  Group = -> [H_element138,C_element148,N_element068,O_element130,P_element019]
  conduct = 2
  density = 1
  expand = 3
  formula = G4_DNA_MU
  name = G4_DNA_MU
  specific = 4
FEATURE [App::DocumentObjectGroupPython] BioChemical  # scripted group (container) (typed FeaturePython)
  Group = -> [G4_CYTOSINE,G4_THYMINE,G4_URACIL,G4_DNA_ADENINE,G4_DNA_GUANINE,G4_DNA_CYTOSINE,G4_DNA_THYMINE,G4_DNA_URACIL,G4_DNA_ADENOSINE,G4_DNA_GUANOSINE,G4_DNA_CYTIDINE,G4_DNA_URIDINE,G4_DNA_METHYLURIDINE,G4_DNA_MONOPHOSPHATE,G4_DNA_A,G4_DNA_G,G4_DNA_C,G4_DNA_U,G4_DNA_MU]
FEATURE [App::DocumentObjectGroupPython] G4Materials  # scripted group (container) (typed FeaturePython)
  Group = -> [NIST,Element,HEP,Space,BioChemical]
  version = 1
FEATURE [App::DocumentObjectGroupPython] Geant4  # scripted group (container) (typed FeaturePython)
  Group = -> [G4Isotopes,G4Elements,G4Materials]
FEATURE [App::DocumentObjectGroupPython] Materials  # scripted group (container) (typed FeaturePython)
  Group = -> [Geant4]
FEATURE [Part::FeaturePython] GDMLBox_WorldBox  # WARN: FeaturePython — macro-defined, semantics opaque (R4)
  lunit = 2
  material = 5
  x = 273
  y = 273
  z = 130
FEATURE [Part::FeaturePython] GDMLBox_Box  # WARN: FeaturePython — macro-defined, semantics opaque (R4)
  Placement = pos=(20,0,0) rot=(0,0,1;0rad)
  lunit = 2
  material = 0
  x = 10
  y = 10
  z = 10
FEATURE [Part::FeaturePython] GDMLTube  # WARN: FeaturePython — macro-defined, semantics opaque (R4)
  Placement = pos=(17,-4,0) rot=(0,0,1;0rad)
  aunit = 1
  deltaphi = 90
  lunit = 2
  material = 0
  rmax = 7
  rmin = 5
  startphi = 0
  z = 7
FEATURE [App::Part] LV_Tube
  Group = -> [GDMLTube]
  Origin = -> Origin003
  SkinSurface = 0
FEATURE [App::Part] LV_Box
  Group = -> [GDMLBox_Box,LV_Tube]
  Origin = -> Origin002
FEATURE [Part::FeaturePython] Array  # Draft array (typed FeaturePython)
  AlwaysSyncPlacement = false
  Angle = 180
  ArrayType = 1
  Axis = (0,0,1)
  Base = -> LV_Box
  Center = (0,0,0)
  Count = 5
  ExpandArray = false
  Fuse = false
  IntervalAxis = (0,0,0)
  IntervalX = (100,0,0)
  IntervalY = (0,100,0)
  IntervalZ = (0,0,100)
  NumberCircles = 3
  NumberPolar = 5
  NumberX = 2
  NumberY = 2
  NumberZ = 1
  PlacementList = 5 placements: [(0,0,0),(0,0,0),(0,0,0),(0,0,0),(0,0,0)]
  RadialDistance = 50
  ScaleList = (5) [(1,1,1),(1,1,1),(1,1,1),(1,1,1),(1,1,1)]
  Symmetry = 1
  TangentialDistance = 25
FEATURE [App::Part] Part  label="experiment"
  Group = -> [LV_Box,Array]
  Origin = -> Origin001
FEATURE [Part::FeaturePython] Array001  # Draft array (typed FeaturePython)
  AlwaysSyncPlacement = false
  Angle = 360
  ArrayType = 0
  Axis = (0,0,1)
  Base = -> Part
  Center = (0,0,0)
  Count = 4
  ExpandArray = false
  Fuse = false
  IntervalAxis = (0,0,0)
  IntervalX = (100,0,0)
  IntervalY = (0,100,0)
  IntervalZ = (0,0,100)
  NumberCircles = 3
  NumberPolar = 5
  NumberX = 2
  NumberY = 2
  NumberZ = 1
  PlacementList = 4 placements: [(0,0,0),(0,100,0),(100,0,0),(100,100,0)]
  RadialDistance = 50
  ScaleList = (4) [(1,1,1),(1,1,1),(1,1,1),(1,1,1)]
  Symmetry = 1
  TangentialDistance = 25
FEATURE [App::Part] Part001
  Group = -> [Part,Array001]
  Origin = -> Origin004
FEATURE [App::Part] worldVOL
  Group = -> [GDMLBox_WorldBox,Part001]
  Origin = -> Origin
